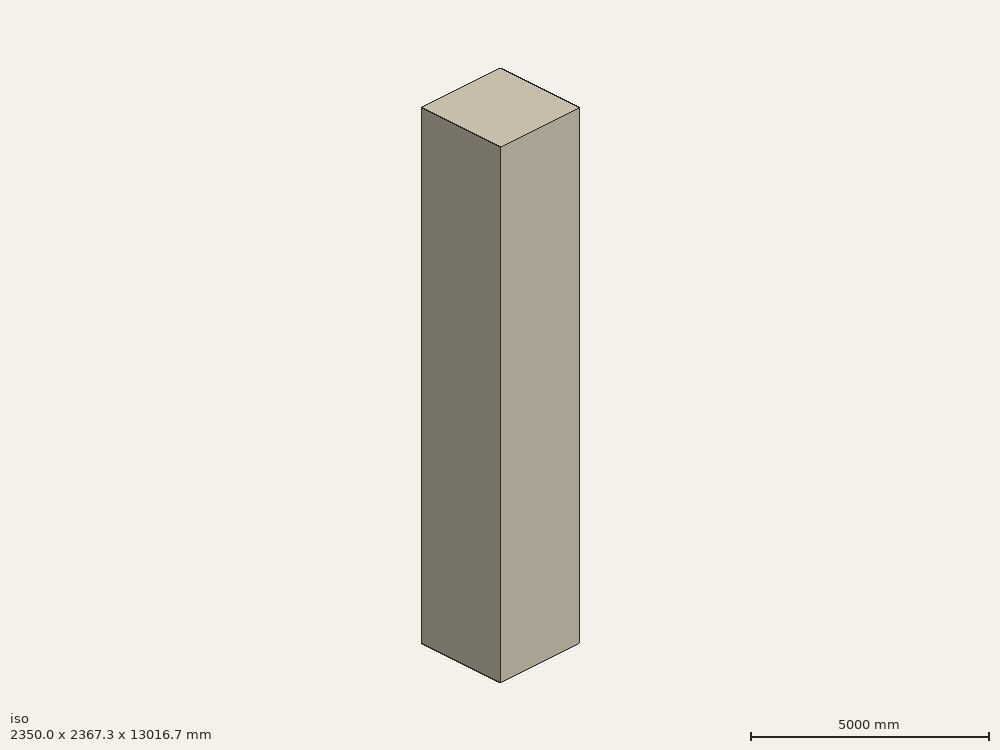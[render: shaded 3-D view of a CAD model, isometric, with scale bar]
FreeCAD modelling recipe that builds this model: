
FCSTD DOCUMENT  (FreeCAD 1.0R39109 (Git))
Label: revolveTester-7-a
License: All rights reserved
objects: App::DocumentObjectGroupPython×1252, Spreadsheet::Sheet×2, Part::FeaturePython×2, App::Part×2, Part::Cylinder×1, Sketcher::SketchObject×1, Part::Revolution×1, Part::Cut×1
note: 7 computed .brp shape members not serialized (recipe doc carries the construction recipe); baked Part::Feature solids carry a one-line shape summary decoded from their .brp

FEATURE [Spreadsheet::Sheet] defines
  cells = A1='constant; B1='HALFPI; C1(HALFPI)==pi / 2; A2='constant; B2='PI; C2(PI)==1 * pi; A3='constant; B3='TWOPI; C3(TWOPI)==2 * pi
FEATURE [Spreadsheet::Sheet] gdmlInfo
FEATURE [App::DocumentObjectGroupPython] Define  # scripted group (container) (typed FeaturePython)
  Group = -> [defines,gdmlInfo]
FEATURE [App::DocumentObjectGroupPython] HALFPI  # scripted group (container) (typed FeaturePython)
  name = HALFPI
  value = pi/2.
FEATURE [App::DocumentObjectGroupPython] PI  # scripted group (container) (typed FeaturePython)
  name = PI
  value = 1.*pi
FEATURE [App::DocumentObjectGroupPython] TWOPI  # scripted group (container) (typed FeaturePython)
  name = TWOPI
  value = 2.*pi
FEATURE [App::DocumentObjectGroupPython] Constants  # scripted group (container) (typed FeaturePython)
  Group = -> [HALFPI,PI,TWOPI]
FEATURE [App::DocumentObjectGroupPython] Quantities  # scripted group (container) (typed FeaturePython)
FEATURE [App::DocumentObjectGroupPython] Variables  # scripted group (container) (typed FeaturePython)
FEATURE [App::DocumentObjectGroupPython] Isotopes  # scripted group (container) (typed FeaturePython)
FEATURE [App::DocumentObjectGroupPython] Elements  # scripted group (container) (typed FeaturePython)
FEATURE [App::DocumentObjectGroupPython] Matrix  # scripted group (container) (typed FeaturePython)
FEATURE [App::DocumentObjectGroupPython] Surfaces  # scripted group (container) (typed FeaturePython)
FEATURE [App::DocumentObjectGroupPython] Opticals  # scripted group (container) (typed FeaturePython)
  Group = -> [Matrix,Surfaces]
FEATURE [App::DocumentObjectGroupPython] G4Isotopes  # scripted group (container) (typed FeaturePython)
FEATURE [App::DocumentObjectGroupPython] H_element  # scripted group (container) (typed FeaturePython)
  Z = 1
  atom_value = 1.008
  formula = H
  name = H_element
FEATURE [App::DocumentObjectGroupPython] He_element  # scripted group (container) (typed FeaturePython)
  Z = 2
  atom_value = 4.0026
  formula = He
  name = He_element
FEATURE [App::DocumentObjectGroupPython] Li_element  # scripted group (container) (typed FeaturePython)
  Z = 3
  atom_value = 6.94
  formula = Li
  name = Li_element
FEATURE [App::DocumentObjectGroupPython] Be_element  # scripted group (container) (typed FeaturePython)
  Z = 4
  atom_value = 9.01218
  formula = Be
  name = Be_element
FEATURE [App::DocumentObjectGroupPython] B_element  # scripted group (container) (typed FeaturePython)
  Z = 5
  atom_value = 10.81
  formula = B
  name = B_element
FEATURE [App::DocumentObjectGroupPython] C_element  # scripted group (container) (typed FeaturePython)
  Z = 6
  atom_value = 12.011
  formula = C
  name = C_element
FEATURE [App::DocumentObjectGroupPython] N_element  # scripted group (container) (typed FeaturePython)
  Z = 7
  atom_value = 14.007
  formula = N
  name = N_element
FEATURE [App::DocumentObjectGroupPython] O_element  # scripted group (container) (typed FeaturePython)
  Z = 8
  atom_value = 15.999
  formula = O
  name = O_element
FEATURE [App::DocumentObjectGroupPython] F_element  # scripted group (container) (typed FeaturePython)
  Z = 9
  atom_value = 18.9984
  formula = F
  name = F_element
FEATURE [App::DocumentObjectGroupPython] Ne_element  # scripted group (container) (typed FeaturePython)
  Z = 10
  atom_value = 20.1797
  formula = Ne
  name = Ne_element
FEATURE [App::DocumentObjectGroupPython] Na_element  # scripted group (container) (typed FeaturePython)
  Z = 11
  atom_value = 22.9898
  formula = Na
  name = Na_element
FEATURE [App::DocumentObjectGroupPython] Mg_element  # scripted group (container) (typed FeaturePython)
  Z = 12
  atom_value = 24.305
  formula = Mg
  name = Mg_element
FEATURE [App::DocumentObjectGroupPython] Al_element  # scripted group (container) (typed FeaturePython)
  Z = 13
  atom_value = 26.9815
  formula = Al
  name = Al_element
FEATURE [App::DocumentObjectGroupPython] Si_element  # scripted group (container) (typed FeaturePython)
  Z = 14
  atom_value = 28.085
  formula = Si
  name = Si_element
FEATURE [App::DocumentObjectGroupPython] P_element  # scripted group (container) (typed FeaturePython)
  Z = 15
  atom_value = 30.9738
  formula = P
  name = P_element
FEATURE [App::DocumentObjectGroupPython] S_element  # scripted group (container) (typed FeaturePython)
  Z = 16
  atom_value = 32.06
  formula = S
  name = S_element
FEATURE [App::DocumentObjectGroupPython] Cl_element  # scripted group (container) (typed FeaturePython)
  Z = 17
  atom_value = 35.45
  formula = Cl
  name = Cl_element
FEATURE [App::DocumentObjectGroupPython] Ar_element  # scripted group (container) (typed FeaturePython)
  Z = 18
  atom_value = 39.95
  formula = Ar
  name = Ar_element
FEATURE [App::DocumentObjectGroupPython] K_element  # scripted group (container) (typed FeaturePython)
  Z = 19
  atom_value = 39.0983
  formula = K
  name = K_element
FEATURE [App::DocumentObjectGroupPython] Ca_element  # scripted group (container) (typed FeaturePython)
  Z = 20
  atom_value = 40.078
  formula = Ca
  name = Ca_element
FEATURE [App::DocumentObjectGroupPython] Sc_element  # scripted group (container) (typed FeaturePython)
  Z = 21
  atom_value = 44.9559
  formula = Sc
  name = Sc_element
FEATURE [App::DocumentObjectGroupPython] Ti_element  # scripted group (container) (typed FeaturePython)
  Z = 22
  atom_value = 47.867
  formula = Ti
  name = Ti_element
FEATURE [App::DocumentObjectGroupPython] V_element  # scripted group (container) (typed FeaturePython)
  Z = 23
  atom_value = 50.9415
  formula = V
  name = V_element
FEATURE [App::DocumentObjectGroupPython] Cr_element  # scripted group (container) (typed FeaturePython)
  Z = 24
  atom_value = 51.9961
  formula = Cr
  name = Cr_element
FEATURE [App::DocumentObjectGroupPython] Mn_element  # scripted group (container) (typed FeaturePython)
  Z = 25
  atom_value = 54.938
  formula = Mn
  name = Mn_element
FEATURE [App::DocumentObjectGroupPython] Fe_element  # scripted group (container) (typed FeaturePython)
  Z = 26
  atom_value = 55.845
  formula = Fe
  name = Fe_element
FEATURE [App::DocumentObjectGroupPython] Co_element  # scripted group (container) (typed FeaturePython)
  Z = 27
  atom_value = 58.9332
  formula = Co
  name = Co_element
FEATURE [App::DocumentObjectGroupPython] Ni_element  # scripted group (container) (typed FeaturePython)
  Z = 28
  atom_value = 58.6934
  formula = Ni
  name = Ni_element
FEATURE [App::DocumentObjectGroupPython] Cu_element  # scripted group (container) (typed FeaturePython)
  Z = 29
  atom_value = 63.546
  formula = Cu
  name = Cu_element
FEATURE [App::DocumentObjectGroupPython] Zn_element  # scripted group (container) (typed FeaturePython)
  Z = 30
  atom_value = 65.38
  formula = Zn
  name = Zn_element
FEATURE [App::DocumentObjectGroupPython] Ga_element  # scripted group (container) (typed FeaturePython)
  Z = 31
  atom_value = 69.723
  formula = Ga
  name = Ga_element
FEATURE [App::DocumentObjectGroupPython] Ge_element  # scripted group (container) (typed FeaturePython)
  Z = 32
  atom_value = 72.63
  formula = Ge
  name = Ge_element
FEATURE [App::DocumentObjectGroupPython] As_element  # scripted group (container) (typed FeaturePython)
  Z = 33
  atom_value = 74.9216
  formula = As
  name = As_element
FEATURE [App::DocumentObjectGroupPython] Se_element  # scripted group (container) (typed FeaturePython)
  Z = 34
  atom_value = 78.971
  formula = Se
  name = Se_element
FEATURE [App::DocumentObjectGroupPython] Br_element  # scripted group (container) (typed FeaturePython)
  Z = 35
  atom_value = 79.904
  formula = Br
  name = Br_element
FEATURE [App::DocumentObjectGroupPython] Kr_element  # scripted group (container) (typed FeaturePython)
  Z = 36
  atom_value = 83.798
  formula = Kr
  name = Kr_element
FEATURE [App::DocumentObjectGroupPython] Rb_element  # scripted group (container) (typed FeaturePython)
  Z = 37
  atom_value = 85.4678
  formula = Rb
  name = Rb_element
FEATURE [App::DocumentObjectGroupPython] Sr_element  # scripted group (container) (typed FeaturePython)
  Z = 38
  atom_value = 87.62
  formula = Sr
  name = Sr_element
FEATURE [App::DocumentObjectGroupPython] Y_element  # scripted group (container) (typed FeaturePython)
  Z = 39
  atom_value = 88.9058
  formula = Y
  name = Y_element
FEATURE [App::DocumentObjectGroupPython] Zr_element  # scripted group (container) (typed FeaturePython)
  Z = 40
  atom_value = 91.224
  formula = Zr
  name = Zr_element
FEATURE [App::DocumentObjectGroupPython] Nb_element  # scripted group (container) (typed FeaturePython)
  Z = 41
  atom_value = 92.9064
  formula = Nb
  name = Nb_element
FEATURE [App::DocumentObjectGroupPython] Mo_element  # scripted group (container) (typed FeaturePython)
  Z = 42
  atom_value = 95.95
  formula = Mo
  name = Mo_element
FEATURE [App::DocumentObjectGroupPython] Tc_element  # scripted group (container) (typed FeaturePython)
  Z = 43
  atom_value = 97
  formula = Tc
  name = Tc_element
FEATURE [App::DocumentObjectGroupPython] Ru_element  # scripted group (container) (typed FeaturePython)
  Z = 44
  atom_value = 101.07
  formula = Ru
  name = Ru_element
FEATURE [App::DocumentObjectGroupPython] Rh_element  # scripted group (container) (typed FeaturePython)
  Z = 45
  atom_value = 102.905
  formula = Rh
  name = Rh_element
FEATURE [App::DocumentObjectGroupPython] Pd_element  # scripted group (container) (typed FeaturePython)
  Z = 46
  atom_value = 106.42
  formula = Pd
  name = Pd_element
FEATURE [App::DocumentObjectGroupPython] Ag_element  # scripted group (container) (typed FeaturePython)
  Z = 47
  atom_value = 107.868
  formula = Ag
  name = Ag_element
FEATURE [App::DocumentObjectGroupPython] Cd_element  # scripted group (container) (typed FeaturePython)
  Z = 48
  atom_value = 112.414
  formula = Cd
  name = Cd_element
FEATURE [App::DocumentObjectGroupPython] In_element  # scripted group (container) (typed FeaturePython)
  Z = 49
  atom_value = 114.818
  formula = In
  name = In_element
FEATURE [App::DocumentObjectGroupPython] Sn_element  # scripted group (container) (typed FeaturePython)
  Z = 50
  atom_value = 118.71
  formula = Sn
  name = Sn_element
FEATURE [App::DocumentObjectGroupPython] Sb_element  # scripted group (container) (typed FeaturePython)
  Z = 51
  atom_value = 121.76
  formula = Sb
  name = Sb_element
FEATURE [App::DocumentObjectGroupPython] Te_element  # scripted group (container) (typed FeaturePython)
  Z = 52
  atom_value = 127.6
  formula = Te
  name = Te_element
FEATURE [App::DocumentObjectGroupPython] I_element  # scripted group (container) (typed FeaturePython)
  Z = 53
  atom_value = 126.904
  formula = I
  name = I_element
FEATURE [App::DocumentObjectGroupPython] Xe_element  # scripted group (container) (typed FeaturePython)
  Z = 54
  atom_value = 131.293
  formula = Xe
  name = Xe_element
FEATURE [App::DocumentObjectGroupPython] Cs_element  # scripted group (container) (typed FeaturePython)
  Z = 55
  atom_value = 132.905
  formula = Cs
  name = Cs_element
FEATURE [App::DocumentObjectGroupPython] Ba_element  # scripted group (container) (typed FeaturePython)
  Z = 56
  atom_value = 137.327
  formula = Ba
  name = Ba_element
FEATURE [App::DocumentObjectGroupPython] La_element  # scripted group (container) (typed FeaturePython)
  Z = 57
  atom_value = 138.905
  formula = La
  name = La_element
FEATURE [App::DocumentObjectGroupPython] Ce_element  # scripted group (container) (typed FeaturePython)
  Z = 58
  atom_value = 140.116
  formula = Ce
  name = Ce_element
FEATURE [App::DocumentObjectGroupPython] Pr_element  # scripted group (container) (typed FeaturePython)
  Z = 59
  atom_value = 140.908
  formula = Pr
  name = Pr_element
FEATURE [App::DocumentObjectGroupPython] Nd_element  # scripted group (container) (typed FeaturePython)
  Z = 60
  atom_value = 144.242
  formula = Nd
  name = Nd_element
FEATURE [App::DocumentObjectGroupPython] Pm_element  # scripted group (container) (typed FeaturePython)
  Z = 61
  atom_value = 145
  formula = Pm
  name = Pm_element
FEATURE [App::DocumentObjectGroupPython] Sm_element  # scripted group (container) (typed FeaturePython)
  Z = 62
  atom_value = 150.36
  formula = Sm
  name = Sm_element
FEATURE [App::DocumentObjectGroupPython] Eu_element  # scripted group (container) (typed FeaturePython)
  Z = 63
  atom_value = 151.964
  formula = Eu
  name = Eu_element
FEATURE [App::DocumentObjectGroupPython] Gd_element  # scripted group (container) (typed FeaturePython)
  Z = 64
  atom_value = 157.25
  formula = Gd
  name = Gd_element
FEATURE [App::DocumentObjectGroupPython] Tb_element  # scripted group (container) (typed FeaturePython)
  Z = 65
  atom_value = 158.925
  formula = Tb
  name = Tb_element
FEATURE [App::DocumentObjectGroupPython] Dy_element  # scripted group (container) (typed FeaturePython)
  Z = 66
  atom_value = 162.5
  formula = Dy
  name = Dy_element
FEATURE [App::DocumentObjectGroupPython] Ho_element  # scripted group (container) (typed FeaturePython)
  Z = 67
  atom_value = 164.93
  formula = Ho
  name = Ho_element
FEATURE [App::DocumentObjectGroupPython] Er_element  # scripted group (container) (typed FeaturePython)
  Z = 68
  atom_value = 167.259
  formula = Er
  name = Er_element
FEATURE [App::DocumentObjectGroupPython] Tm_element  # scripted group (container) (typed FeaturePython)
  Z = 69
  atom_value = 168.934
  formula = Tm
  name = Tm_element
FEATURE [App::DocumentObjectGroupPython] Yb_element  # scripted group (container) (typed FeaturePython)
  Z = 70
  atom_value = 173.045
  formula = Yb
  name = Yb_element
FEATURE [App::DocumentObjectGroupPython] Lu_element  # scripted group (container) (typed FeaturePython)
  Z = 71
  atom_value = 174.967
  formula = Lu
  name = Lu_element
FEATURE [App::DocumentObjectGroupPython] Hf_element  # scripted group (container) (typed FeaturePython)
  Z = 72
  atom_value = 178.49
  formula = Hf
  name = Hf_element
FEATURE [App::DocumentObjectGroupPython] Ta_element  # scripted group (container) (typed FeaturePython)
  Z = 73
  atom_value = 180.948
  formula = Ta
  name = Ta_element
FEATURE [App::DocumentObjectGroupPython] W_element  # scripted group (container) (typed FeaturePython)
  Z = 74
  atom_value = 183.84
  formula = W
  name = W_element
FEATURE [App::DocumentObjectGroupPython] Re_element  # scripted group (container) (typed FeaturePython)
  Z = 75
  atom_value = 186.207
  formula = Re
  name = Re_element
FEATURE [App::DocumentObjectGroupPython] Os_element  # scripted group (container) (typed FeaturePython)
  Z = 76
  atom_value = 190.23
  formula = Os
  name = Os_element
FEATURE [App::DocumentObjectGroupPython] Ir_element  # scripted group (container) (typed FeaturePython)
  Z = 77
  atom_value = 192.217
  formula = Ir
  name = Ir_element
FEATURE [App::DocumentObjectGroupPython] Pt_element  # scripted group (container) (typed FeaturePython)
  Z = 78
  atom_value = 195.084
  formula = Pt
  name = Pt_element
FEATURE [App::DocumentObjectGroupPython] Au_element  # scripted group (container) (typed FeaturePython)
  Z = 79
  atom_value = 196.967
  formula = Au
  name = Au_element
FEATURE [App::DocumentObjectGroupPython] Hg_element  # scripted group (container) (typed FeaturePython)
  Z = 80
  atom_value = 200.592
  formula = Hg
  name = Hg_element
FEATURE [App::DocumentObjectGroupPython] Tl_element  # scripted group (container) (typed FeaturePython)
  Z = 81
  atom_value = 204.38
  formula = Tl
  name = Tl_element
FEATURE [App::DocumentObjectGroupPython] Pb_element  # scripted group (container) (typed FeaturePython)
  Z = 82
  atom_value = 207.2
  formula = Pb
  name = Pb_element
FEATURE [App::DocumentObjectGroupPython] Bi_element  # scripted group (container) (typed FeaturePython)
  Z = 83
  atom_value = 208.98
  formula = Bi
  name = Bi_element
FEATURE [App::DocumentObjectGroupPython] Po_element  # scripted group (container) (typed FeaturePython)
  Z = 84
  atom_value = 209
  formula = Po
  name = Po_element
FEATURE [App::DocumentObjectGroupPython] At_element  # scripted group (container) (typed FeaturePython)
  Z = 85
  atom_value = 210
  formula = At
  name = At_element
FEATURE [App::DocumentObjectGroupPython] Rn_element  # scripted group (container) (typed FeaturePython)
  Z = 86
  atom_value = 222
  formula = Rn
  name = Rn_element
FEATURE [App::DocumentObjectGroupPython] Fr_element  # scripted group (container) (typed FeaturePython)
  Z = 87
  atom_value = 223
  formula = Fr
  name = Fr_element
FEATURE [App::DocumentObjectGroupPython] Ra_element  # scripted group (container) (typed FeaturePython)
  Z = 88
  atom_value = 226
  formula = Ra
  name = Ra_element
FEATURE [App::DocumentObjectGroupPython] Ac_element  # scripted group (container) (typed FeaturePython)
  Z = 89
  atom_value = 227
  formula = Ac
  name = Ac_element
FEATURE [App::DocumentObjectGroupPython] Th_element  # scripted group (container) (typed FeaturePython)
  Z = 90
  atom_value = 232.038
  formula = Th
  name = Th_element
FEATURE [App::DocumentObjectGroupPython] Pa_element  # scripted group (container) (typed FeaturePython)
  Z = 91
  atom_value = 231.036
  formula = Pa
  name = Pa_element
FEATURE [App::DocumentObjectGroupPython] U_element  # scripted group (container) (typed FeaturePython)
  Z = 92
  atom_value = 238.029
  formula = U
  name = U_element
FEATURE [App::DocumentObjectGroupPython] Np_element  # scripted group (container) (typed FeaturePython)
  Z = 93
  atom_value = 237
  formula = Np
  name = Np_element
FEATURE [App::DocumentObjectGroupPython] Pu_element  # scripted group (container) (typed FeaturePython)
  Z = 94
  atom_value = 244
  formula = Pu
  name = Pu_element
FEATURE [App::DocumentObjectGroupPython] Am_element  # scripted group (container) (typed FeaturePython)
  Z = 95
  atom_value = 243
  formula = Am
  name = Am_element
FEATURE [App::DocumentObjectGroupPython] Cm_element  # scripted group (container) (typed FeaturePython)
  Z = 96
  atom_value = 247
  formula = Cm
  name = Cm_element
FEATURE [App::DocumentObjectGroupPython] Bk_element  # scripted group (container) (typed FeaturePython)
  Z = 97
  atom_value = 247
  formula = Bk
  name = Bk_element
FEATURE [App::DocumentObjectGroupPython] Cf_element  # scripted group (container) (typed FeaturePython)
  Z = 98
  atom_value = 251
  formula = Cf
  name = Cf_element
FEATURE [App::DocumentObjectGroupPython] G4Elements  # scripted group (container) (typed FeaturePython)
  Group = -> [H_element,He_element,Li_element,Be_element,B_element,C_element,N_element,O_element,F_element,Ne_element,Na_element,Mg_element,Al_element,Si_element,P_element,S_element,Cl_element,Ar_element,K_element,Ca_element,Sc_element,Ti_element,V_element,Cr_element,Mn_element,Fe_element,Co_element,Ni_element,Cu_element,Zn_element,Ga_element,Ge_element,As_element,Se_element,Br_element,Kr_element,Rb_element,+61 more]
FEATURE [App::DocumentObjectGroupPython] H_element001  label="H_element : 0.101"  # scripted group (container) (typed FeaturePython)
  n = 0.101327
FEATURE [App::DocumentObjectGroupPython] C_element001  label="C_element : 0.775"  # scripted group (container) (typed FeaturePython)
  n = 0.7755
FEATURE [App::DocumentObjectGroupPython] N_element001  label="N_element : 0.035"  # scripted group (container) (typed FeaturePython)
  n = 0.035057
FEATURE [App::DocumentObjectGroupPython] O_element001  label="O_element : 0.052"  # scripted group (container) (typed FeaturePython)
  n = 0.0523159
FEATURE [App::DocumentObjectGroupPython] F_element001  label="F_element : 0.017"  # scripted group (container) (typed FeaturePython)
  n = 0.017422
FEATURE [App::DocumentObjectGroupPython] Ca_element001  label="Ca_element : 0.018"  # scripted group (container) (typed FeaturePython)
  n = 0.018378
FEATURE [App::DocumentObjectGroupPython] G4_A_150_TISSUE  label="G4_A-150_TISSUE"  # scripted group (container) (typed FeaturePython)
  Dunit = g/cm3
  Dvalue = 1.127
  Group = -> [H_element001,C_element001,N_element001,O_element001,F_element001,Ca_element001]
  conduct = 2
  density = 1
  expand = 3
  formula = G4_A-150_TISSUE
  name = G4_A-150_TISSUE
  specific = 4
FEATURE [App::DocumentObjectGroupPython] C_element002  label="C_element : 3"  # scripted group (container) (typed FeaturePython)
  n = 3
  ref = C_element
FEATURE [App::DocumentObjectGroupPython] H_element002  label="H_element : 6"  # scripted group (container) (typed FeaturePython)
  n = 6
  ref = H_element
FEATURE [App::DocumentObjectGroupPython] O_element002  label="O_element : 1"  # scripted group (container) (typed FeaturePython)
  n = 1
  ref = O_element
FEATURE [App::DocumentObjectGroupPython] G4_ACETONE  # scripted group (container) (typed FeaturePython)
  Dunit = g/cm3
  Dvalue = 0.7899
  Group = -> [C_element002,H_element002,O_element002]
  conduct = 2
  density = 1
  expand = 3
  formula = G4_ACETONE
  name = G4_ACETONE
  specific = 4
FEATURE [App::DocumentObjectGroupPython] C_element003  label="C_element : 2"  # scripted group (container) (typed FeaturePython)
  n = 2
  ref = C_element
FEATURE [App::DocumentObjectGroupPython] H_element003  label="H_element : 2"  # scripted group (container) (typed FeaturePython)
  n = 2
  ref = H_element
FEATURE [App::DocumentObjectGroupPython] G4_ACETYLENE  # scripted group (container) (typed FeaturePython)
  Dunit = g/cm3
  Dvalue = 0.0010967
  Group = -> [C_element003,H_element003]
  conduct = 2
  density = 1
  expand = 3
  formula = G4_ACETYLENE
  name = G4_ACETYLENE
  specific = 4
FEATURE [App::DocumentObjectGroupPython] C_element004  label="C_element : 5"  # scripted group (container) (typed FeaturePython)
  n = 5
  ref = C_element
FEATURE [App::DocumentObjectGroupPython] H_element004  label="H_element : 5"  # scripted group (container) (typed FeaturePython)
  n = 5
  ref = H_element
FEATURE [App::DocumentObjectGroupPython] N_element002  label="N_element : 5"  # scripted group (container) (typed FeaturePython)
  n = 5
  ref = N_element
FEATURE [App::DocumentObjectGroupPython] G4_ADENINE  # scripted group (container) (typed FeaturePython)
  Dunit = g/cm3
  Dvalue = 1.6
  Group = -> [C_element004,H_element004,N_element002]
  conduct = 2
  density = 1
  expand = 3
  formula = G4_ADENINE
  name = G4_ADENINE
  specific = 4
FEATURE [App::DocumentObjectGroupPython] H_element005  label="H_element : 0.114"  # scripted group (container) (typed FeaturePython)
  n = 0.114
FEATURE [App::DocumentObjectGroupPython] C_element005  label="C_element : 0.598"  # scripted group (container) (typed FeaturePython)
  n = 0.598
FEATURE [App::DocumentObjectGroupPython] N_element003  label="N_element : 0.007"  # scripted group (container) (typed FeaturePython)
  n = 0.007
FEATURE [App::DocumentObjectGroupPython] O_element003  label="O_element : 0.278"  # scripted group (container) (typed FeaturePython)
  n = 0.278
FEATURE [App::DocumentObjectGroupPython] Na_element001  label="Na_element : 0.001"  # scripted group (container) (typed FeaturePython)
  n = 0.001
FEATURE [App::DocumentObjectGroupPython] S_element001  label="S_element : 0.001"  # scripted group (container) (typed FeaturePython)
  n = 0.001
FEATURE [App::DocumentObjectGroupPython] Cl_element001  label="Cl_element : 0.001"  # scripted group (container) (typed FeaturePython)
  n = 0.001
FEATURE [App::DocumentObjectGroupPython] G4_ADIPOSE_TISSUE_ICRP  # scripted group (container) (typed FeaturePython)
  Dunit = g/cm3
  Dvalue = 0.95
  Group = -> [H_element005,C_element005,N_element003,O_element003,Na_element001,S_element001,Cl_element001]
  conduct = 2
  density = 1
  expand = 3
  formula = G4_ADIPOSE_TISSUE_ICRP
  name = G4_ADIPOSE_TISSUE_ICRP
  specific = 4
FEATURE [App::DocumentObjectGroupPython] C_element006  label="C_element : 0.000"  # scripted group (container) (typed FeaturePython)
  n = 0.000124
FEATURE [App::DocumentObjectGroupPython] N_element004  label="N_element : 0.755"  # scripted group (container) (typed FeaturePython)
  n = 0.755268
FEATURE [App::DocumentObjectGroupPython] O_element004  label="O_element : 0.232"  # scripted group (container) (typed FeaturePython)
  n = 0.231781
FEATURE [App::DocumentObjectGroupPython] Ar_element001  label="Ar_element : 0.013"  # scripted group (container) (typed FeaturePython)
  n = 0.012827
FEATURE [App::DocumentObjectGroupPython] G4_AIR  # scripted group (container) (typed FeaturePython)
  Dunit = g/cm3
  Dvalue = 0.00120479
  Group = -> [C_element006,N_element004,O_element004,Ar_element001]
  conduct = 2
  density = 1
  expand = 3
  formula = G4_AIR
  name = G4_AIR
  specific = 4
FEATURE [App::DocumentObjectGroupPython] C_element007  label="C_element : 006"  # scripted group (container) (typed FeaturePython)
  n = 3
  ref = C_element
FEATURE [App::DocumentObjectGroupPython] H_element006  label="H_element : 7"  # scripted group (container) (typed FeaturePython)
  n = 7
  ref = H_element
FEATURE [App::DocumentObjectGroupPython] N_element005  label="N_element : 1"  # scripted group (container) (typed FeaturePython)
  n = 1
  ref = N_element
FEATURE [App::DocumentObjectGroupPython] O_element005  label="O_element : 2"  # scripted group (container) (typed FeaturePython)
  n = 2
  ref = O_element
FEATURE [App::DocumentObjectGroupPython] G4_ALANINE  # scripted group (container) (typed FeaturePython)
  Dunit = g/cm3
  Dvalue = 1.42
  Group = -> [C_element007,H_element006,N_element005,O_element005]
  conduct = 2
  density = 1
  expand = 3
  formula = G4_ALANINE
  name = G4_ALANINE
  specific = 4
FEATURE [App::DocumentObjectGroupPython] Al_element001  label="Al_element : 2"  # scripted group (container) (typed FeaturePython)
  n = 2
  ref = Al_element
FEATURE [App::DocumentObjectGroupPython] O_element006  label="O_element : 3"  # scripted group (container) (typed FeaturePython)
  n = 3
  ref = O_element
FEATURE [App::DocumentObjectGroupPython] G4_ALUMINUM_OXIDE  # scripted group (container) (typed FeaturePython)
  Dunit = g/cm3
  Dvalue = 3.97
  Group = -> [Al_element001,O_element006]
  conduct = 2
  density = 1
  expand = 3
  formula = G4_ALUMINUM_OXIDE
  name = G4_ALUMINUM_OXIDE
  specific = 4
FEATURE [App::DocumentObjectGroupPython] H_element007  label="H_element : 0.106"  # scripted group (container) (typed FeaturePython)
  n = 0.10593
FEATURE [App::DocumentObjectGroupPython] C_element008  label="C_element : 0.789"  # scripted group (container) (typed FeaturePython)
  n = 0.788974
FEATURE [App::DocumentObjectGroupPython] O_element007  label="O_element : 0.105"  # scripted group (container) (typed FeaturePython)
  n = 0.105096
FEATURE [App::DocumentObjectGroupPython] G4_AMBER  # scripted group (container) (typed FeaturePython)
  Dunit = g/cm3
  Dvalue = 1.1
  Group = -> [H_element007,C_element008,O_element007]
  conduct = 2
  density = 1
  expand = 3
  formula = G4_AMBER
  name = G4_AMBER
  specific = 4
FEATURE [App::DocumentObjectGroupPython] N_element006  label="N_element : 006"  # scripted group (container) (typed FeaturePython)
  n = 1
  ref = N_element
FEATURE [App::DocumentObjectGroupPython] H_element008  label="H_element : 3"  # scripted group (container) (typed FeaturePython)
  n = 3
  ref = H_element
FEATURE [App::DocumentObjectGroupPython] G4_AMMONIA  # scripted group (container) (typed FeaturePython)
  Dunit = g/cm3
  Dvalue = 0.000826019
  Group = -> [N_element006,H_element008]
  conduct = 2
  density = 1
  expand = 3
  formula = G4_AMMONIA
  name = G4_AMMONIA
  specific = 4
FEATURE [App::DocumentObjectGroupPython] C_element009  label="C_element : 6"  # scripted group (container) (typed FeaturePython)
  n = 6
  ref = C_element
FEATURE [App::DocumentObjectGroupPython] H_element009  label="H_element : 008"  # scripted group (container) (typed FeaturePython)
  n = 7
  ref = H_element
FEATURE [App::DocumentObjectGroupPython] N_element007  label="N_element : 007"  # scripted group (container) (typed FeaturePython)
  n = 1
  ref = N_element
FEATURE [App::DocumentObjectGroupPython] G4_ANILINE  # scripted group (container) (typed FeaturePython)
  Dunit = g/cm3
  Dvalue = 1.0235
  Group = -> [C_element009,H_element009,N_element007]
  conduct = 2
  density = 1
  expand = 3
  formula = G4_ANILINE
  name = G4_ANILINE
  specific = 4
FEATURE [App::DocumentObjectGroupPython] C_element010  label="C_element : 14"  # scripted group (container) (typed FeaturePython)
  n = 14
  ref = C_element
FEATURE [App::DocumentObjectGroupPython] H_element010  label="H_element : 10"  # scripted group (container) (typed FeaturePython)
  n = 10
  ref = H_element
FEATURE [App::DocumentObjectGroupPython] G4_ANTHRACENE  # scripted group (container) (typed FeaturePython)
  Dunit = g/cm3
  Dvalue = 1.283
  Group = -> [C_element010,H_element010]
  conduct = 2
  density = 1
  expand = 3
  formula = G4_ANTHRACENE
  name = G4_ANTHRACENE
  specific = 4
FEATURE [App::DocumentObjectGroupPython] H_element011  label="H_element : 0.065"  # scripted group (container) (typed FeaturePython)
  n = 0.0654709
FEATURE [App::DocumentObjectGroupPython] C_element011  label="C_element : 0.537"  # scripted group (container) (typed FeaturePython)
  n = 0.536944
FEATURE [App::DocumentObjectGroupPython] N_element008  label="N_element : 0.021"  # scripted group (container) (typed FeaturePython)
  n = 0.0215
FEATURE [App::DocumentObjectGroupPython] O_element008  label="O_element : 0.032"  # scripted group (container) (typed FeaturePython)
  n = 0.032085
FEATURE [App::DocumentObjectGroupPython] F_element002  label="F_element : 0.167"  # scripted group (container) (typed FeaturePython)
  n = 0.167411
FEATURE [App::DocumentObjectGroupPython] Ca_element002  label="Ca_element : 0.177"  # scripted group (container) (typed FeaturePython)
  n = 0.176589
FEATURE [App::DocumentObjectGroupPython] G4_B_100_BONE  label="G4_B-100_BONE"  # scripted group (container) (typed FeaturePython)
  Dunit = g/cm3
  Dvalue = 1.45
  Group = -> [H_element011,C_element011,N_element008,O_element008,F_element002,Ca_element002]
  conduct = 2
  density = 1
  expand = 3
  formula = G4_B-100_BONE
  name = G4_B-100_BONE
  specific = 4
FEATURE [App::DocumentObjectGroupPython] H_element012  label="H_element : 0.057"  # scripted group (container) (typed FeaturePython)
  n = 0.057441
FEATURE [App::DocumentObjectGroupPython] C_element012  label="C_element : 0.790"  # scripted group (container) (typed FeaturePython)
  n = 0.774591
FEATURE [App::DocumentObjectGroupPython] O_element009  label="O_element : 0.168"  # scripted group (container) (typed FeaturePython)
  n = 0.167968
FEATURE [App::DocumentObjectGroupPython] G4_BAKELITE  # scripted group (container) (typed FeaturePython)
  Dunit = g/cm3
  Dvalue = 1.25
  Group = -> [H_element012,C_element012,O_element009]
  conduct = 2
  density = 1
  expand = 3
  formula = G4_BAKELITE
  name = G4_BAKELITE
  specific = 4
FEATURE [App::DocumentObjectGroupPython] Ba_element001  label="Ba_element : 1"  # scripted group (container) (typed FeaturePython)
  n = 1
  ref = Ba_element
FEATURE [App::DocumentObjectGroupPython] F_element003  label="F_element : 2"  # scripted group (container) (typed FeaturePython)
  n = 2
  ref = F_element
FEATURE [App::DocumentObjectGroupPython] G4_BARIUM_FLUORIDE  # scripted group (container) (typed FeaturePython)
  Dunit = g/cm3
  Dvalue = 4.89
  Group = -> [Ba_element001,F_element003]
  conduct = 2
  density = 1
  expand = 3
  formula = G4_BARIUM_FLUORIDE
  name = G4_BARIUM_FLUORIDE
  specific = 4
FEATURE [App::DocumentObjectGroupPython] Ba_element002  label="Ba_element : 002"  # scripted group (container) (typed FeaturePython)
  n = 1
  ref = Ba_element
FEATURE [App::DocumentObjectGroupPython] S_element002  label="S_element : 1"  # scripted group (container) (typed FeaturePython)
  n = 1
  ref = S_element
FEATURE [App::DocumentObjectGroupPython] O_element010  label="O_element : 4"  # scripted group (container) (typed FeaturePython)
  n = 4
  ref = O_element
FEATURE [App::DocumentObjectGroupPython] G4_BARIUM_SULFATE  # scripted group (container) (typed FeaturePython)
  Dunit = g/cm3
  Dvalue = 4.5
  Group = -> [Ba_element002,S_element002,O_element010]
  conduct = 2
  density = 1
  expand = 3
  formula = G4_BARIUM_SULFATE
  name = G4_BARIUM_SULFATE
  specific = 4
FEATURE [App::DocumentObjectGroupPython] C_element013  label="C_element : 007"  # scripted group (container) (typed FeaturePython)
  n = 6
  ref = C_element
FEATURE [App::DocumentObjectGroupPython] H_element013  label="H_element : 009"  # scripted group (container) (typed FeaturePython)
  n = 6
  ref = H_element
FEATURE [App::DocumentObjectGroupPython] G4_BENZENE  # scripted group (container) (typed FeaturePython)
  Dunit = g/cm3
  Dvalue = 0.87865
  Group = -> [C_element013,H_element013]
  conduct = 2
  density = 1
  expand = 3
  formula = G4_BENZENE
  name = G4_BENZENE
  specific = 4
FEATURE [App::DocumentObjectGroupPython] Be_element001  label="Be_element : 1"  # scripted group (container) (typed FeaturePython)
  n = 1
  ref = Be_element
FEATURE [App::DocumentObjectGroupPython] O_element011  label="O_element : 005"  # scripted group (container) (typed FeaturePython)
  n = 1
  ref = O_element
FEATURE [App::DocumentObjectGroupPython] G4_BERYLLIUM_OXIDE  # scripted group (container) (typed FeaturePython)
  Dunit = g/cm3
  Dvalue = 3.01
  Group = -> [Be_element001,O_element011]
  conduct = 2
  density = 1
  expand = 3
  formula = G4_BERYLLIUM_OXIDE
  name = G4_BERYLLIUM_OXIDE
  specific = 4
FEATURE [App::DocumentObjectGroupPython] Bi_element001  label="Bi_element : 4"  # scripted group (container) (typed FeaturePython)
  n = 4
  ref = Bi_element
FEATURE [App::DocumentObjectGroupPython] Ge_element001  label="Ge_element : 3"  # scripted group (container) (typed FeaturePython)
  n = 3
  ref = Ge_element
FEATURE [App::DocumentObjectGroupPython] O_element012  label="O_element : 12"  # scripted group (container) (typed FeaturePython)
  n = 12
  ref = O_element
FEATURE [App::DocumentObjectGroupPython] G4_BGO  # scripted group (container) (typed FeaturePython)
  Dunit = g/cm3
  Dvalue = 7.13
  Group = -> [Bi_element001,Ge_element001,O_element012]
  conduct = 2
  density = 1
  expand = 3
  formula = G4_BGO
  name = G4_BGO
  specific = 4
FEATURE [App::DocumentObjectGroupPython] H_element014  label="H_element : 0.102"  # scripted group (container) (typed FeaturePython)
  n = 0.102
FEATURE [App::DocumentObjectGroupPython] C_element014  label="C_element : 0.110"  # scripted group (container) (typed FeaturePython)
  n = 0.11
FEATURE [App::DocumentObjectGroupPython] N_element009  label="N_element : 0.033"  # scripted group (container) (typed FeaturePython)
  n = 0.033
FEATURE [App::DocumentObjectGroupPython] O_element013  label="O_element : 0.745"  # scripted group (container) (typed FeaturePython)
  n = 0.745
FEATURE [App::DocumentObjectGroupPython] Na_element002  label="Na_element : 0.002"  # scripted group (container) (typed FeaturePython)
  n = 0.001
FEATURE [App::DocumentObjectGroupPython] P_element001  label="P_element : 0.001"  # scripted group (container) (typed FeaturePython)
  n = 0.001
FEATURE [App::DocumentObjectGroupPython] S_element003  label="S_element : 0.002"  # scripted group (container) (typed FeaturePython)
  n = 0.002
FEATURE [App::DocumentObjectGroupPython] Cl_element002  label="Cl_element : 0.003"  # scripted group (container) (typed FeaturePython)
  n = 0.003
FEATURE [App::DocumentObjectGroupPython] K_element001  label="K_element : 0.002"  # scripted group (container) (typed FeaturePython)
  n = 0.002
FEATURE [App::DocumentObjectGroupPython] Fe_element001  label="Fe_element : 0.001"  # scripted group (container) (typed FeaturePython)
  n = 0.001
FEATURE [App::DocumentObjectGroupPython] G4_BLOOD_ICRP  # scripted group (container) (typed FeaturePython)
  Dunit = g/cm3
  Dvalue = 1.06
  Group = -> [H_element014,C_element014,N_element009,O_element013,Na_element002,P_element001,S_element003,Cl_element002,K_element001,Fe_element001]
  conduct = 2
  density = 1
  expand = 3
  formula = G4_BLOOD_ICRP
  name = G4_BLOOD_ICRP
  specific = 4
FEATURE [App::DocumentObjectGroupPython] H_element015  label="H_element : 0.064"  # scripted group (container) (typed FeaturePython)
  n = 0.064
FEATURE [App::DocumentObjectGroupPython] C_element015  label="C_element : 0.278"  # scripted group (container) (typed FeaturePython)
  n = 0.278
FEATURE [App::DocumentObjectGroupPython] N_element010  label="N_element : 0.027"  # scripted group (container) (typed FeaturePython)
  n = 0.027
FEATURE [App::DocumentObjectGroupPython] O_element014  label="O_element : 0.410"  # scripted group (container) (typed FeaturePython)
  n = 0.41
FEATURE [App::DocumentObjectGroupPython] Mg_element001  label="Mg_element : 0.002"  # scripted group (container) (typed FeaturePython)
  n = 0.002
FEATURE [App::DocumentObjectGroupPython] P_element002  label="P_element : 0.070"  # scripted group (container) (typed FeaturePython)
  n = 0.07
FEATURE [App::DocumentObjectGroupPython] S_element004  label="S_element : 0.003"  # scripted group (container) (typed FeaturePython)
  n = 0.002
FEATURE [App::DocumentObjectGroupPython] Ca_element003  label="Ca_element : 0.147"  # scripted group (container) (typed FeaturePython)
  n = 0.147
FEATURE [App::DocumentObjectGroupPython] G4_BONE_COMPACT_ICRU  # scripted group (container) (typed FeaturePython)
  Dunit = g/cm3
  Dvalue = 1.85
  Group = -> [H_element015,C_element015,N_element010,O_element014,Mg_element001,P_element002,S_element004,Ca_element003]
  conduct = 2
  density = 1
  expand = 3
  formula = G4_BONE_COMPACT_ICRU
  name = G4_BONE_COMPACT_ICRU
  specific = 4
FEATURE [App::DocumentObjectGroupPython] H_element016  label="H_element : 0.034"  # scripted group (container) (typed FeaturePython)
  n = 0.034
FEATURE [App::DocumentObjectGroupPython] C_element016  label="C_element : 0.155"  # scripted group (container) (typed FeaturePython)
  n = 0.155
FEATURE [App::DocumentObjectGroupPython] N_element011  label="N_element : 0.042"  # scripted group (container) (typed FeaturePython)
  n = 0.042
FEATURE [App::DocumentObjectGroupPython] O_element015  label="O_element : 0.435"  # scripted group (container) (typed FeaturePython)
  n = 0.435
FEATURE [App::DocumentObjectGroupPython] Na_element003  label="Na_element : 0.003"  # scripted group (container) (typed FeaturePython)
  n = 0.001
FEATURE [App::DocumentObjectGroupPython] Mg_element002  label="Mg_element : 0.003"  # scripted group (container) (typed FeaturePython)
  n = 0.002
FEATURE [App::DocumentObjectGroupPython] P_element003  label="P_element : 0.103"  # scripted group (container) (typed FeaturePython)
  n = 0.103
FEATURE [App::DocumentObjectGroupPython] S_element005  label="S_element : 0.004"  # scripted group (container) (typed FeaturePython)
  n = 0.003
FEATURE [App::DocumentObjectGroupPython] Ca_element004  label="Ca_element : 0.225"  # scripted group (container) (typed FeaturePython)
  n = 0.225
FEATURE [App::DocumentObjectGroupPython] G4_BONE_CORTICAL_ICRP  # scripted group (container) (typed FeaturePython)
  Dunit = g/cm3
  Dvalue = 1.92
  Group = -> [H_element016,C_element016,N_element011,O_element015,Na_element003,Mg_element002,P_element003,S_element005,Ca_element004]
  conduct = 2
  density = 1
  expand = 3
  formula = G4_BONE_CORTICAL_ICRP
  name = G4_BONE_CORTICAL_ICRP
  specific = 4
FEATURE [App::DocumentObjectGroupPython] B_element001  label="B_element : 4"  # scripted group (container) (typed FeaturePython)
  n = 4
  ref = B_element
FEATURE [App::DocumentObjectGroupPython] C_element017  label="C_element : 1"  # scripted group (container) (typed FeaturePython)
  n = 1
  ref = C_element
FEATURE [App::DocumentObjectGroupPython] G4_BORON_CARBIDE  # scripted group (container) (typed FeaturePython)
  Dunit = g/cm3
  Dvalue = 2.52
  Group = -> [B_element001,C_element017]
  conduct = 2
  density = 1
  expand = 3
  formula = G4_BORON_CARBIDE
  name = G4_BORON_CARBIDE
  specific = 4
FEATURE [App::DocumentObjectGroupPython] B_element002  label="B_element : 2"  # scripted group (container) (typed FeaturePython)
  n = 2
  ref = B_element
FEATURE [App::DocumentObjectGroupPython] O_element016  label="O_element : 006"  # scripted group (container) (typed FeaturePython)
  n = 3
  ref = O_element
FEATURE [App::DocumentObjectGroupPython] G4_BORON_OXIDE  # scripted group (container) (typed FeaturePython)
  Dunit = g/cm3
  Dvalue = 1.812
  Group = -> [B_element002,O_element016]
  conduct = 2
  density = 1
  expand = 3
  formula = G4_BORON_OXIDE
  name = G4_BORON_OXIDE
  specific = 4
FEATURE [App::DocumentObjectGroupPython] H_element017  label="H_element : 0.107"  # scripted group (container) (typed FeaturePython)
  n = 0.107
FEATURE [App::DocumentObjectGroupPython] C_element018  label="C_element : 0.145"  # scripted group (container) (typed FeaturePython)
  n = 0.145
FEATURE [App::DocumentObjectGroupPython] N_element012  label="N_element : 0.022"  # scripted group (container) (typed FeaturePython)
  n = 0.022
FEATURE [App::DocumentObjectGroupPython] O_element017  label="O_element : 0.712"  # scripted group (container) (typed FeaturePython)
  n = 0.712
FEATURE [App::DocumentObjectGroupPython] Na_element004  label="Na_element : 0.004"  # scripted group (container) (typed FeaturePython)
  n = 0.002
FEATURE [App::DocumentObjectGroupPython] P_element004  label="P_element : 0.004"  # scripted group (container) (typed FeaturePython)
  n = 0.004
FEATURE [App::DocumentObjectGroupPython] S_element006  label="S_element : 0.005"  # scripted group (container) (typed FeaturePython)
  n = 0.002
FEATURE [App::DocumentObjectGroupPython] Cl_element003  label="Cl_element : 0.004"  # scripted group (container) (typed FeaturePython)
  n = 0.003
FEATURE [App::DocumentObjectGroupPython] K_element002  label="K_element : 0.003"  # scripted group (container) (typed FeaturePython)
  n = 0.003
FEATURE [App::DocumentObjectGroupPython] G4_BRAIN_ICRP  # scripted group (container) (typed FeaturePython)
  Dunit = g/cm3
  Dvalue = 1.04
  Group = -> [H_element017,C_element018,N_element012,O_element017,Na_element004,P_element004,S_element006,Cl_element003,K_element002]
  conduct = 2
  density = 1
  expand = 3
  formula = G4_BRAIN_ICRP
  name = G4_BRAIN_ICRP
  specific = 4
FEATURE [App::DocumentObjectGroupPython] C_element019  label="C_element : 4"  # scripted group (container) (typed FeaturePython)
  n = 4
  ref = C_element
FEATURE [App::DocumentObjectGroupPython] H_element018  label="H_element : 010"  # scripted group (container) (typed FeaturePython)
  n = 10
  ref = H_element
FEATURE [App::DocumentObjectGroupPython] G4_BUTANE  # scripted group (container) (typed FeaturePython)
  Dunit = g/cm3
  Dvalue = 0.00249343
  Group = -> [C_element019,H_element018]
  conduct = 2
  density = 1
  expand = 3
  formula = G4_BUTANE
  name = G4_BUTANE
  specific = 4
FEATURE [App::DocumentObjectGroupPython] C_element020  label="C_element : 008"  # scripted group (container) (typed FeaturePython)
  n = 4
  ref = C_element
FEATURE [App::DocumentObjectGroupPython] H_element019  label="H_element : 011"  # scripted group (container) (typed FeaturePython)
  n = 10
  ref = H_element
FEATURE [App::DocumentObjectGroupPython] O_element018  label="O_element : 007"  # scripted group (container) (typed FeaturePython)
  n = 1
  ref = O_element
FEATURE [App::DocumentObjectGroupPython] G4_N_BUTYL_ALCOHOL  label="G4_N-BUTYL_ALCOHOL"  # scripted group (container) (typed FeaturePython)
  Dunit = g/cm3
  Dvalue = 0.8098
  Group = -> [C_element020,H_element019,O_element018]
  conduct = 2
  density = 1
  expand = 3
  formula = G4_N-BUTYL_ALCOHOL
  name = G4_N-BUTYL_ALCOHOL
  specific = 4
FEATURE [App::DocumentObjectGroupPython] H_element020  label="H_element : 0.025"  # scripted group (container) (typed FeaturePython)
  n = 0.02468
FEATURE [App::DocumentObjectGroupPython] C_element021  label="C_element : 0.502"  # scripted group (container) (typed FeaturePython)
  n = 0.501611
FEATURE [App::DocumentObjectGroupPython] O_element019  label="O_element : 0.005"  # scripted group (container) (typed FeaturePython)
  n = 0.004527
FEATURE [App::DocumentObjectGroupPython] F_element004  label="F_element : 0.465"  # scripted group (container) (typed FeaturePython)
  n = 0.465209
FEATURE [App::DocumentObjectGroupPython] Si_element001  label="Si_element : 0.004"  # scripted group (container) (typed FeaturePython)
  n = 0.003973
FEATURE [App::DocumentObjectGroupPython] G4_C_552  label="G4_C-552"  # scripted group (container) (typed FeaturePython)
  Dunit = g/cm3
  Dvalue = 1.76
  Group = -> [H_element020,C_element021,O_element019,F_element004,Si_element001]
  conduct = 2
  density = 1
  expand = 3
  formula = G4_C-552
  name = G4_C-552
  specific = 4
FEATURE [App::DocumentObjectGroupPython] Cd_element001  label="Cd_element : 1"  # scripted group (container) (typed FeaturePython)
  n = 1
  ref = Cd_element
FEATURE [App::DocumentObjectGroupPython] Te_element001  label="Te_element : 1"  # scripted group (container) (typed FeaturePython)
  n = 1
  ref = Te_element
FEATURE [App::DocumentObjectGroupPython] G4_CADMIUM_TELLURIDE  # scripted group (container) (typed FeaturePython)
  Dunit = g/cm3
  Dvalue = 6.2
  Group = -> [Cd_element001,Te_element001]
  conduct = 2
  density = 1
  expand = 3
  formula = G4_CADMIUM_TELLURIDE
  name = G4_CADMIUM_TELLURIDE
  specific = 4
FEATURE [App::DocumentObjectGroupPython] Cd_element002  label="Cd_element : 002"  # scripted group (container) (typed FeaturePython)
  n = 1
  ref = Cd_element
FEATURE [App::DocumentObjectGroupPython] W_element001  label="W_element : 1"  # scripted group (container) (typed FeaturePython)
  n = 1
  ref = W_element
FEATURE [App::DocumentObjectGroupPython] O_element020  label="O_element : 008"  # scripted group (container) (typed FeaturePython)
  n = 4
  ref = O_element
FEATURE [App::DocumentObjectGroupPython] G4_CADMIUM_TUNGSTATE  # scripted group (container) (typed FeaturePython)
  Dunit = g/cm3
  Dvalue = 7.9
  Group = -> [Cd_element002,W_element001,O_element020]
  conduct = 2
  density = 1
  expand = 3
  formula = G4_CADMIUM_TUNGSTATE
  name = G4_CADMIUM_TUNGSTATE
  specific = 4
FEATURE [App::DocumentObjectGroupPython] Ca_element005  label="Ca_element : 1"  # scripted group (container) (typed FeaturePython)
  n = 1
  ref = Ca_element
FEATURE [App::DocumentObjectGroupPython] C_element022  label="C_element : 009"  # scripted group (container) (typed FeaturePython)
  n = 1
  ref = C_element
FEATURE [App::DocumentObjectGroupPython] O_element021  label="O_element : 009"  # scripted group (container) (typed FeaturePython)
  n = 3
  ref = O_element
FEATURE [App::DocumentObjectGroupPython] G4_CALCIUM_CARBONATE  # scripted group (container) (typed FeaturePython)
  Dunit = g/cm3
  Dvalue = 2.8
  Group = -> [Ca_element005,C_element022,O_element021]
  conduct = 2
  density = 1
  expand = 3
  formula = G4_CALCIUM_CARBONATE
  name = G4_CALCIUM_CARBONATE
  specific = 4
FEATURE [App::DocumentObjectGroupPython] Ca_element006  label="Ca_element : 002"  # scripted group (container) (typed FeaturePython)
  n = 1
  ref = Ca_element
FEATURE [App::DocumentObjectGroupPython] F_element005  label="F_element : 003"  # scripted group (container) (typed FeaturePython)
  n = 2
  ref = F_element
FEATURE [App::DocumentObjectGroupPython] G4_CALCIUM_FLUORIDE  # scripted group (container) (typed FeaturePython)
  Dunit = g/cm3
  Dvalue = 3.18
  Group = -> [Ca_element006,F_element005]
  conduct = 2
  density = 1
  expand = 3
  formula = G4_CALCIUM_FLUORIDE
  name = G4_CALCIUM_FLUORIDE
  specific = 4
FEATURE [App::DocumentObjectGroupPython] Ca_element007  label="Ca_element : 003"  # scripted group (container) (typed FeaturePython)
  n = 1
  ref = Ca_element
FEATURE [App::DocumentObjectGroupPython] O_element022  label="O_element : 010"  # scripted group (container) (typed FeaturePython)
  n = 1
  ref = O_element
FEATURE [App::DocumentObjectGroupPython] G4_CALCIUM_OXIDE  # scripted group (container) (typed FeaturePython)
  Dunit = g/cm3
  Dvalue = 3.3
  Group = -> [Ca_element007,O_element022]
  conduct = 2
  density = 1
  expand = 3
  formula = G4_CALCIUM_OXIDE
  name = G4_CALCIUM_OXIDE
  specific = 4
FEATURE [App::DocumentObjectGroupPython] Ca_element008  label="Ca_element : 004"  # scripted group (container) (typed FeaturePython)
  n = 1
  ref = Ca_element
FEATURE [App::DocumentObjectGroupPython] S_element007  label="S_element : 002"  # scripted group (container) (typed FeaturePython)
  n = 1
  ref = S_element
FEATURE [App::DocumentObjectGroupPython] O_element023  label="O_element : 011"  # scripted group (container) (typed FeaturePython)
  n = 4
  ref = O_element
FEATURE [App::DocumentObjectGroupPython] G4_CALCIUM_SULFATE  # scripted group (container) (typed FeaturePython)
  Dunit = g/cm3
  Dvalue = 2.96
  Group = -> [Ca_element008,S_element007,O_element023]
  conduct = 2
  density = 1
  expand = 3
  formula = G4_CALCIUM_SULFATE
  name = G4_CALCIUM_SULFATE
  specific = 4
FEATURE [App::DocumentObjectGroupPython] Ca_element009  label="Ca_element : 005"  # scripted group (container) (typed FeaturePython)
  n = 1
  ref = Ca_element
FEATURE [App::DocumentObjectGroupPython] W_element002  label="W_element : 002"  # scripted group (container) (typed FeaturePython)
  n = 1
  ref = W_element
FEATURE [App::DocumentObjectGroupPython] O_element024  label="O_element : 012"  # scripted group (container) (typed FeaturePython)
  n = 4
  ref = O_element
FEATURE [App::DocumentObjectGroupPython] G4_CALCIUM_TUNGSTATE  # scripted group (container) (typed FeaturePython)
  Dunit = g/cm3
  Dvalue = 6.062
  Group = -> [Ca_element009,W_element002,O_element024]
  conduct = 2
  density = 1
  expand = 3
  formula = G4_CALCIUM_TUNGSTATE
  name = G4_CALCIUM_TUNGSTATE
  specific = 4
FEATURE [App::DocumentObjectGroupPython] C_element023  label="C_element : 010"  # scripted group (container) (typed FeaturePython)
  n = 1
  ref = C_element
FEATURE [App::DocumentObjectGroupPython] O_element025  label="O_element : 013"  # scripted group (container) (typed FeaturePython)
  n = 2
  ref = O_element
FEATURE [App::DocumentObjectGroupPython] G4_CARBON_DIOXIDE  # scripted group (container) (typed FeaturePython)
  Dunit = g/cm3
  Dvalue = 0.00184212
  Group = -> [C_element023,O_element025]
  conduct = 2
  density = 1
  expand = 3
  formula = G4_CARBON_DIOXIDE
  name = G4_CARBON_DIOXIDE
  specific = 4
FEATURE [App::DocumentObjectGroupPython] C_element024  label="C_element : 011"  # scripted group (container) (typed FeaturePython)
  n = 1
  ref = C_element
FEATURE [App::DocumentObjectGroupPython] Cl_element004  label="Cl_element : 4"  # scripted group (container) (typed FeaturePython)
  n = 4
  ref = Cl_element
FEATURE [App::DocumentObjectGroupPython] G4_CARBON_TETRACHLORIDE  # scripted group (container) (typed FeaturePython)
  Dunit = g/cm3
  Dvalue = 1.594
  Group = -> [C_element024,Cl_element004]
  conduct = 2
  density = 1
  expand = 3
  formula = G4_CARBON_TETRACHLORIDE
  name = G4_CARBON_TETRACHLORIDE
  specific = 4
FEATURE [App::DocumentObjectGroupPython] C_element025  label="C_element : 012"  # scripted group (container) (typed FeaturePython)
  n = 6
  ref = C_element
FEATURE [App::DocumentObjectGroupPython] H_element021  label="H_element : 012"  # scripted group (container) (typed FeaturePython)
  n = 10
  ref = H_element
FEATURE [App::DocumentObjectGroupPython] O_element026  label="O_element : 5"  # scripted group (container) (typed FeaturePython)
  n = 5
  ref = O_element
FEATURE [App::DocumentObjectGroupPython] G4_CELLULOSE_CELLOPHANE  # scripted group (container) (typed FeaturePython)
  Dunit = g/cm3
  Dvalue = 1.42
  Group = -> [C_element025,H_element021,O_element026]
  conduct = 2
  density = 1
  expand = 3
  formula = G4_CELLULOSE_CELLOPHANE
  name = G4_CELLULOSE_CELLOPHANE
  specific = 4
FEATURE [App::DocumentObjectGroupPython] H_element022  label="H_element : 0.067"  # scripted group (container) (typed FeaturePython)
  n = 0.067125
FEATURE [App::DocumentObjectGroupPython] C_element026  label="C_element : 0.545"  # scripted group (container) (typed FeaturePython)
  n = 0.545403
FEATURE [App::DocumentObjectGroupPython] O_element027  label="O_element : 0.387"  # scripted group (container) (typed FeaturePython)
  n = 0.387472
FEATURE [App::DocumentObjectGroupPython] G4_CELLULOSE_BUTYRATE  # scripted group (container) (typed FeaturePython)
  Dunit = g/cm3
  Dvalue = 1.2
  Group = -> [H_element022,C_element026,O_element027]
  conduct = 2
  density = 1
  expand = 3
  formula = G4_CELLULOSE_BUTYRATE
  name = G4_CELLULOSE_BUTYRATE
  specific = 4
FEATURE [App::DocumentObjectGroupPython] H_element023  label="H_element : 0.029"  # scripted group (container) (typed FeaturePython)
  n = 0.029216
FEATURE [App::DocumentObjectGroupPython] C_element027  label="C_element : 0.271"  # scripted group (container) (typed FeaturePython)
  n = 0.271296
FEATURE [App::DocumentObjectGroupPython] N_element013  label="N_element : 0.121"  # scripted group (container) (typed FeaturePython)
  n = 0.121276
FEATURE [App::DocumentObjectGroupPython] O_element028  label="O_element : 0.578"  # scripted group (container) (typed FeaturePython)
  n = 0.578212
FEATURE [App::DocumentObjectGroupPython] G4_CELLULOSE_NITRATE  # scripted group (container) (typed FeaturePython)
  Dunit = g/cm3
  Dvalue = 1.49
  Group = -> [H_element023,C_element027,N_element013,O_element028]
  conduct = 2
  density = 1
  expand = 3
  formula = G4_CELLULOSE_NITRATE
  name = G4_CELLULOSE_NITRATE
  specific = 4
FEATURE [App::DocumentObjectGroupPython] H_element024  label="H_element : 0.108"  # scripted group (container) (typed FeaturePython)
  n = 0.107596
FEATURE [App::DocumentObjectGroupPython] N_element014  label="N_element : 0.001"  # scripted group (container) (typed FeaturePython)
  n = 0.0008
FEATURE [App::DocumentObjectGroupPython] O_element029  label="O_element : 0.875"  # scripted group (container) (typed FeaturePython)
  n = 0.874976
FEATURE [App::DocumentObjectGroupPython] S_element008  label="S_element : 0.015"  # scripted group (container) (typed FeaturePython)
  n = 0.014627
FEATURE [App::DocumentObjectGroupPython] Ce_element001  label="Ce_element : 0.002"  # scripted group (container) (typed FeaturePython)
  n = 0.002001
FEATURE [App::DocumentObjectGroupPython] G4_CERIC_SULFATE  # scripted group (container) (typed FeaturePython)
  Dunit = g/cm3
  Dvalue = 1.03
  Group = -> [H_element024,N_element014,O_element029,S_element008,Ce_element001]
  conduct = 2
  density = 1
  expand = 3
  formula = G4_CERIC_SULFATE
  name = G4_CERIC_SULFATE
  specific = 4
FEATURE [App::DocumentObjectGroupPython] Cs_element001  label="Cs_element : 1"  # scripted group (container) (typed FeaturePython)
  n = 1
  ref = Cs_element
FEATURE [App::DocumentObjectGroupPython] F_element006  label="F_element : 1"  # scripted group (container) (typed FeaturePython)
  n = 1
  ref = F_element
FEATURE [App::DocumentObjectGroupPython] G4_CESIUM_FLUORIDE  # scripted group (container) (typed FeaturePython)
  Dunit = g/cm3
  Dvalue = 4.115
  Group = -> [Cs_element001,F_element006]
  conduct = 2
  density = 1
  expand = 3
  formula = G4_CESIUM_FLUORIDE
  name = G4_CESIUM_FLUORIDE
  specific = 4
FEATURE [App::DocumentObjectGroupPython] Cs_element002  label="Cs_element : 002"  # scripted group (container) (typed FeaturePython)
  n = 1
  ref = Cs_element
FEATURE [App::DocumentObjectGroupPython] I_element001  label="I_element : 1"  # scripted group (container) (typed FeaturePython)
  n = 1
  ref = I_element
FEATURE [App::DocumentObjectGroupPython] G4_CESIUM_IODIDE  # scripted group (container) (typed FeaturePython)
  Dunit = g/cm3
  Dvalue = 4.51
  Group = -> [Cs_element002,I_element001]
  conduct = 2
  density = 1
  expand = 3
  formula = G4_CESIUM_IODIDE
  name = G4_CESIUM_IODIDE
  specific = 4
FEATURE [App::DocumentObjectGroupPython] C_element028  label="C_element : 013"  # scripted group (container) (typed FeaturePython)
  n = 6
  ref = C_element
FEATURE [App::DocumentObjectGroupPython] H_element025  label="H_element : 013"  # scripted group (container) (typed FeaturePython)
  n = 5
  ref = H_element
FEATURE [App::DocumentObjectGroupPython] Cl_element005  label="Cl_element : 1"  # scripted group (container) (typed FeaturePython)
  n = 1
  ref = Cl_element
FEATURE [App::DocumentObjectGroupPython] G4_CHLOROBENZENE  # scripted group (container) (typed FeaturePython)
  Dunit = g/cm3
  Dvalue = 1.1058
  Group = -> [C_element028,H_element025,Cl_element005]
  conduct = 2
  density = 1
  expand = 3
  formula = G4_CHLOROBENZENE
  name = G4_CHLOROBENZENE
  specific = 4
FEATURE [App::DocumentObjectGroupPython] C_element029  label="C_element : 014"  # scripted group (container) (typed FeaturePython)
  n = 1
  ref = C_element
FEATURE [App::DocumentObjectGroupPython] H_element026  label="H_element : 1"  # scripted group (container) (typed FeaturePython)
  n = 1
  ref = H_element
FEATURE [App::DocumentObjectGroupPython] Cl_element006  label="Cl_element : 3"  # scripted group (container) (typed FeaturePython)
  n = 3
  ref = Cl_element
FEATURE [App::DocumentObjectGroupPython] G4_CHLOROFORM  # scripted group (container) (typed FeaturePython)
  Dunit = g/cm3
  Dvalue = 1.4832
  Group = -> [C_element029,H_element026,Cl_element006]
  conduct = 2
  density = 1
  expand = 3
  formula = G4_CHLOROFORM
  name = G4_CHLOROFORM
  specific = 4
FEATURE [App::DocumentObjectGroupPython] H_element027  label="H_element : 0.010"  # scripted group (container) (typed FeaturePython)
  n = 0.01
FEATURE [App::DocumentObjectGroupPython] C_element030  label="C_element : 0.001"  # scripted group (container) (typed FeaturePython)
  n = 0.001
FEATURE [App::DocumentObjectGroupPython] O_element030  label="O_element : 0.529"  # scripted group (container) (typed FeaturePython)
  n = 0.529107
FEATURE [App::DocumentObjectGroupPython] Na_element005  label="Na_element : 0.016"  # scripted group (container) (typed FeaturePython)
  n = 0.016
FEATURE [App::DocumentObjectGroupPython] Mg_element003  label="Mg_element : 0.004"  # scripted group (container) (typed FeaturePython)
  n = 0.002
FEATURE [App::DocumentObjectGroupPython] Al_element002  label="Al_element : 0.034"  # scripted group (container) (typed FeaturePython)
  n = 0.033872
FEATURE [App::DocumentObjectGroupPython] Si_element002  label="Si_element : 0.337"  # scripted group (container) (typed FeaturePython)
  n = 0.337021
FEATURE [App::DocumentObjectGroupPython] K_element003  label="K_element : 0.013"  # scripted group (container) (typed FeaturePython)
  n = 0.013
FEATURE [App::DocumentObjectGroupPython] Ca_element010  label="Ca_element : 0.044"  # scripted group (container) (typed FeaturePython)
  n = 0.044
FEATURE [App::DocumentObjectGroupPython] Fe_element002  label="Fe_element : 0.014"  # scripted group (container) (typed FeaturePython)
  n = 0.014
FEATURE [App::DocumentObjectGroupPython] G4_CONCRETE  # scripted group (container) (typed FeaturePython)
  Dunit = g/cm3
  Dvalue = 2.3
  Group = -> [H_element027,C_element030,O_element030,Na_element005,Mg_element003,Al_element002,Si_element002,K_element003,Ca_element010,Fe_element002]
  conduct = 2
  density = 1
  expand = 3
  formula = G4_CONCRETE
  name = G4_CONCRETE
  specific = 4
FEATURE [App::DocumentObjectGroupPython] C_element031  label="C_element : 015"  # scripted group (container) (typed FeaturePython)
  n = 6
  ref = C_element
FEATURE [App::DocumentObjectGroupPython] H_element028  label="H_element : 12"  # scripted group (container) (typed FeaturePython)
  n = 12
  ref = H_element
FEATURE [App::DocumentObjectGroupPython] G4_CYCLOHEXANE  # scripted group (container) (typed FeaturePython)
  Dunit = g/cm3
  Dvalue = 0.779
  Group = -> [C_element031,H_element028]
  conduct = 2
  density = 1
  expand = 3
  formula = G4_CYCLOHEXANE
  name = G4_CYCLOHEXANE
  specific = 4
FEATURE [App::DocumentObjectGroupPython] C_element032  label="C_element : 016"  # scripted group (container) (typed FeaturePython)
  n = 6
  ref = C_element
FEATURE [App::DocumentObjectGroupPython] H_element029  label="H_element : 4"  # scripted group (container) (typed FeaturePython)
  n = 4
  ref = H_element
FEATURE [App::DocumentObjectGroupPython] Cl_element007  label="Cl_element : 2"  # scripted group (container) (typed FeaturePython)
  n = 2
  ref = Cl_element
FEATURE [App::DocumentObjectGroupPython] G4_1_2_DICHLOROBENZENE  label="G4_1.2-DICHLOROBENZENE"  # scripted group (container) (typed FeaturePython)
  Dunit = g/cm3
  Dvalue = 1.3048
  Group = -> [C_element032,H_element029,Cl_element007]
  conduct = 2
  density = 1
  expand = 3
  formula = G4_1.2-DICHLOROBENZENE
  name = G4_1.2-DICHLOROBENZENE
  specific = 4
FEATURE [App::DocumentObjectGroupPython] C_element033  label="C_element : 017"  # scripted group (container) (typed FeaturePython)
  n = 4
  ref = C_element
FEATURE [App::DocumentObjectGroupPython] H_element030  label="H_element : 8"  # scripted group (container) (typed FeaturePython)
  n = 8
  ref = H_element
FEATURE [App::DocumentObjectGroupPython] O_element031  label="O_element : 014"  # scripted group (container) (typed FeaturePython)
  n = 1
  ref = O_element
FEATURE [App::DocumentObjectGroupPython] Cl_element008  label="Cl_element : 005"  # scripted group (container) (typed FeaturePython)
  n = 2
  ref = Cl_element
FEATURE [App::DocumentObjectGroupPython] G4_DICHLORODIETHYL_ETHER  # scripted group (container) (typed FeaturePython)
  Dunit = g/cm3
  Dvalue = 1.2199
  Group = -> [C_element033,H_element030,O_element031,Cl_element008]
  conduct = 2
  density = 1
  expand = 3
  formula = G4_DICHLORODIETHYL_ETHER
  name = G4_DICHLORODIETHYL_ETHER
  specific = 4
FEATURE [App::DocumentObjectGroupPython] C_element034  label="C_element : 018"  # scripted group (container) (typed FeaturePython)
  n = 2
  ref = C_element
FEATURE [App::DocumentObjectGroupPython] H_element031  label="H_element : 014"  # scripted group (container) (typed FeaturePython)
  n = 4
  ref = H_element
FEATURE [App::DocumentObjectGroupPython] Cl_element009  label="Cl_element : 006"  # scripted group (container) (typed FeaturePython)
  n = 2
  ref = Cl_element
FEATURE [App::DocumentObjectGroupPython] G4_1_2_DICHLOROETHANE  label="G4_1.2-DICHLOROETHANE"  # scripted group (container) (typed FeaturePython)
  Dunit = g/cm3
  Dvalue = 1.2351
  Group = -> [C_element034,H_element031,Cl_element009]
  conduct = 2
  density = 1
  expand = 3
  formula = G4_1.2-DICHLOROETHANE
  name = G4_1.2-DICHLOROETHANE
  specific = 4
FEATURE [App::DocumentObjectGroupPython] C_element035  label="C_element : 019"  # scripted group (container) (typed FeaturePython)
  n = 4
  ref = C_element
FEATURE [App::DocumentObjectGroupPython] H_element032  label="H_element : 015"  # scripted group (container) (typed FeaturePython)
  n = 10
  ref = H_element
FEATURE [App::DocumentObjectGroupPython] O_element032  label="O_element : 015"  # scripted group (container) (typed FeaturePython)
  n = 1
  ref = O_element
FEATURE [App::DocumentObjectGroupPython] G4_DIETHYL_ETHER  # scripted group (container) (typed FeaturePython)
  Dunit = g/cm3
  Dvalue = 0.71378
  Group = -> [C_element035,H_element032,O_element032]
  conduct = 2
  density = 1
  expand = 3
  formula = G4_DIETHYL_ETHER
  name = G4_DIETHYL_ETHER
  specific = 4
FEATURE [App::DocumentObjectGroupPython] C_element036  label="C_element : 020"  # scripted group (container) (typed FeaturePython)
  n = 3
  ref = C_element
FEATURE [App::DocumentObjectGroupPython] H_element033  label="H_element : 016"  # scripted group (container) (typed FeaturePython)
  n = 7
  ref = H_element
FEATURE [App::DocumentObjectGroupPython] N_element015  label="N_element : 008"  # scripted group (container) (typed FeaturePython)
  n = 1
  ref = N_element
FEATURE [App::DocumentObjectGroupPython] O_element033  label="O_element : 016"  # scripted group (container) (typed FeaturePython)
  n = 1
  ref = O_element
FEATURE [App::DocumentObjectGroupPython] G4_N_N_DIMETHYL_FORMAMIDE  label="G4_N.N-DIMETHYL_FORMAMIDE"  # scripted group (container) (typed FeaturePython)
  Dunit = g/cm3
  Dvalue = 0.9487
  Group = -> [C_element036,H_element033,N_element015,O_element033]
  conduct = 2
  density = 1
  expand = 3
  formula = G4_N.N-DIMETHYL_FORMAMIDE
  name = G4_N.N-DIMETHYL_FORMAMIDE
  specific = 4
FEATURE [App::DocumentObjectGroupPython] C_element037  label="C_element : 021"  # scripted group (container) (typed FeaturePython)
  n = 2
  ref = C_element
FEATURE [App::DocumentObjectGroupPython] H_element034  label="H_element : 017"  # scripted group (container) (typed FeaturePython)
  n = 6
  ref = H_element
FEATURE [App::DocumentObjectGroupPython] O_element034  label="O_element : 017"  # scripted group (container) (typed FeaturePython)
  n = 1
  ref = O_element
FEATURE [App::DocumentObjectGroupPython] S_element009  label="S_element : 003"  # scripted group (container) (typed FeaturePython)
  n = 1
  ref = S_element
FEATURE [App::DocumentObjectGroupPython] G4_DIMETHYL_SULFOXIDE  # scripted group (container) (typed FeaturePython)
  Dunit = g/cm3
  Dvalue = 1.1014
  Group = -> [C_element037,H_element034,O_element034,S_element009]
  conduct = 2
  density = 1
  expand = 3
  formula = G4_DIMETHYL_SULFOXIDE
  name = G4_DIMETHYL_SULFOXIDE
  specific = 4
FEATURE [App::DocumentObjectGroupPython] C_element038  label="C_element : 022"  # scripted group (container) (typed FeaturePython)
  n = 2
  ref = C_element
FEATURE [App::DocumentObjectGroupPython] H_element035  label="H_element : 018"  # scripted group (container) (typed FeaturePython)
  n = 6
  ref = H_element
FEATURE [App::DocumentObjectGroupPython] G4_ETHANE  # scripted group (container) (typed FeaturePython)
  Dunit = g/cm3
  Dvalue = 0.00125324
  Group = -> [C_element038,H_element035]
  conduct = 2
  density = 1
  expand = 3
  formula = G4_ETHANE
  name = G4_ETHANE
  specific = 4
FEATURE [App::DocumentObjectGroupPython] C_element039  label="C_element : 023"  # scripted group (container) (typed FeaturePython)
  n = 2
  ref = C_element
FEATURE [App::DocumentObjectGroupPython] H_element036  label="H_element : 019"  # scripted group (container) (typed FeaturePython)
  n = 6
  ref = H_element
FEATURE [App::DocumentObjectGroupPython] O_element035  label="O_element : 018"  # scripted group (container) (typed FeaturePython)
  n = 1
  ref = O_element
FEATURE [App::DocumentObjectGroupPython] G4_ETHYL_ALCOHOL  # scripted group (container) (typed FeaturePython)
  Dunit = g/cm3
  Dvalue = 0.7893
  Group = -> [C_element039,H_element036,O_element035]
  conduct = 2
  density = 1
  expand = 3
  formula = G4_ETHYL_ALCOHOL
  name = G4_ETHYL_ALCOHOL
  specific = 4
FEATURE [App::DocumentObjectGroupPython] H_element037  label="H_element : 0.090"  # scripted group (container) (typed FeaturePython)
  n = 0.090027
FEATURE [App::DocumentObjectGroupPython] C_element040  label="C_element : 0.585"  # scripted group (container) (typed FeaturePython)
  n = 0.585182
FEATURE [App::DocumentObjectGroupPython] O_element036  label="O_element : 0.325"  # scripted group (container) (typed FeaturePython)
  n = 0.324791
FEATURE [App::DocumentObjectGroupPython] G4_ETHYL_CELLULOSE  # scripted group (container) (typed FeaturePython)
  Dunit = g/cm3
  Dvalue = 1.13
  Group = -> [H_element037,C_element040,O_element036]
  conduct = 2
  density = 1
  expand = 3
  formula = G4_ETHYL_CELLULOSE
  name = G4_ETHYL_CELLULOSE
  specific = 4
FEATURE [App::DocumentObjectGroupPython] C_element041  label="C_element : 024"  # scripted group (container) (typed FeaturePython)
  n = 2
  ref = C_element
FEATURE [App::DocumentObjectGroupPython] H_element038  label="H_element : 020"  # scripted group (container) (typed FeaturePython)
  n = 4
  ref = H_element
FEATURE [App::DocumentObjectGroupPython] G4_ETHYLENE  # scripted group (container) (typed FeaturePython)
  Dunit = g/cm3
  Dvalue = 0.00117497
  Group = -> [C_element041,H_element038]
  conduct = 2
  density = 1
  expand = 3
  formula = G4_ETHYLENE
  name = G4_ETHYLENE
  specific = 4
FEATURE [App::DocumentObjectGroupPython] H_element039  label="H_element : 0.096"  # scripted group (container) (typed FeaturePython)
  n = 0.096
FEATURE [App::DocumentObjectGroupPython] C_element042  label="C_element : 0.195"  # scripted group (container) (typed FeaturePython)
  n = 0.195
FEATURE [App::DocumentObjectGroupPython] N_element016  label="N_element : 0.057"  # scripted group (container) (typed FeaturePython)
  n = 0.057
FEATURE [App::DocumentObjectGroupPython] O_element037  label="O_element : 0.646"  # scripted group (container) (typed FeaturePython)
  n = 0.646
FEATURE [App::DocumentObjectGroupPython] Na_element006  label="Na_element : 0.017"  # scripted group (container) (typed FeaturePython)
  n = 0.001
FEATURE [App::DocumentObjectGroupPython] P_element005  label="P_element : 0.104"  # scripted group (container) (typed FeaturePython)
  n = 0.001
FEATURE [App::DocumentObjectGroupPython] S_element010  label="S_element : 0.016"  # scripted group (container) (typed FeaturePython)
  n = 0.003
FEATURE [App::DocumentObjectGroupPython] Cl_element010  label="Cl_element : 0.005"  # scripted group (container) (typed FeaturePython)
  n = 0.001
FEATURE [App::DocumentObjectGroupPython] G4_EYE_LENS_ICRP  # scripted group (container) (typed FeaturePython)
  Dunit = g/cm3
  Dvalue = 1.07
  Group = -> [H_element039,C_element042,N_element016,O_element037,Na_element006,P_element005,S_element010,Cl_element010]
  conduct = 2
  density = 1
  expand = 3
  formula = G4_EYE_LENS_ICRP
  name = G4_EYE_LENS_ICRP
  specific = 4
FEATURE [App::DocumentObjectGroupPython] Fe_element003  label="Fe_element : 2"  # scripted group (container) (typed FeaturePython)
  n = 2
  ref = Fe_element
FEATURE [App::DocumentObjectGroupPython] O_element038  label="O_element : 019"  # scripted group (container) (typed FeaturePython)
  n = 3
  ref = O_element
FEATURE [App::DocumentObjectGroupPython] G4_FERRIC_OXIDE  # scripted group (container) (typed FeaturePython)
  Dunit = g/cm3
  Dvalue = 5.2
  Group = -> [Fe_element003,O_element038]
  conduct = 2
  density = 1
  expand = 3
  formula = G4_FERRIC_OXIDE
  name = G4_FERRIC_OXIDE
  specific = 4
FEATURE [App::DocumentObjectGroupPython] Fe_element004  label="Fe_element : 1"  # scripted group (container) (typed FeaturePython)
  n = 1
  ref = Fe_element
FEATURE [App::DocumentObjectGroupPython] B_element003  label="B_element : 1"  # scripted group (container) (typed FeaturePython)
  n = 1
  ref = B_element
FEATURE [App::DocumentObjectGroupPython] G4_FERROBORIDE  # scripted group (container) (typed FeaturePython)
  Dunit = g/cm3
  Dvalue = 7.15
  Group = -> [Fe_element004,B_element003]
  conduct = 2
  density = 1
  expand = 3
  formula = G4_FERROBORIDE
  name = G4_FERROBORIDE
  specific = 4
FEATURE [App::DocumentObjectGroupPython] Fe_element005  label="Fe_element : 003"  # scripted group (container) (typed FeaturePython)
  n = 1
  ref = Fe_element
FEATURE [App::DocumentObjectGroupPython] O_element039  label="O_element : 020"  # scripted group (container) (typed FeaturePython)
  n = 1
  ref = O_element
FEATURE [App::DocumentObjectGroupPython] G4_FERROUS_OXIDE  # scripted group (container) (typed FeaturePython)
  Dunit = g/cm3
  Dvalue = 5.7
  Group = -> [Fe_element005,O_element039]
  conduct = 2
  density = 1
  expand = 3
  formula = G4_FERROUS_OXIDE
  name = G4_FERROUS_OXIDE
  specific = 4
FEATURE [App::DocumentObjectGroupPython] H_element040  label="H_element : 0.115"  # scripted group (container) (typed FeaturePython)
  n = 0.108259
FEATURE [App::DocumentObjectGroupPython] N_element017  label="N_element : 0.000"  # scripted group (container) (typed FeaturePython)
  n = 2.7e-05
FEATURE [App::DocumentObjectGroupPython] O_element040  label="O_element : 0.879"  # scripted group (container) (typed FeaturePython)
  n = 0.878636
FEATURE [App::DocumentObjectGroupPython] Na_element007  label="Na_element : 0.000"  # scripted group (container) (typed FeaturePython)
  n = 2.2e-05
FEATURE [App::DocumentObjectGroupPython] S_element011  label="S_element : 0.013"  # scripted group (container) (typed FeaturePython)
  n = 0.012968
FEATURE [App::DocumentObjectGroupPython] Cl_element011  label="Cl_element : 0.000"  # scripted group (container) (typed FeaturePython)
  n = 3.4e-05
FEATURE [App::DocumentObjectGroupPython] Fe_element006  label="Fe_element : 0.000"  # scripted group (container) (typed FeaturePython)
  n = 5.4e-05
FEATURE [App::DocumentObjectGroupPython] G4_FERROUS_SULFATE  # scripted group (container) (typed FeaturePython)
  Dunit = g/cm3
  Dvalue = 1.024
  Group = -> [H_element040,N_element017,O_element040,Na_element007,S_element011,Cl_element011,Fe_element006]
  conduct = 2
  density = 1
  expand = 3
  formula = G4_FERROUS_SULFATE
  name = G4_FERROUS_SULFATE
  specific = 4
FEATURE [App::DocumentObjectGroupPython] C_element043  label="C_element : 0.099"  # scripted group (container) (typed FeaturePython)
  n = 0.099335
FEATURE [App::DocumentObjectGroupPython] F_element007  label="F_element : 0.314"  # scripted group (container) (typed FeaturePython)
  n = 0.314247
FEATURE [App::DocumentObjectGroupPython] Cl_element012  label="Cl_element : 0.586"  # scripted group (container) (typed FeaturePython)
  n = 0.586418
FEATURE [App::DocumentObjectGroupPython] G4_FREON_12  label="G4_FREON-12"  # scripted group (container) (typed FeaturePython)
  Dunit = g/cm3
  Dvalue = 1.12
  Group = -> [C_element043,F_element007,Cl_element012]
  conduct = 2
  density = 1
  expand = 3
  formula = G4_FREON-12
  name = G4_FREON-12
  specific = 4
FEATURE [App::DocumentObjectGroupPython] C_element044  label="C_element : 0.057"  # scripted group (container) (typed FeaturePython)
  n = 0.057245
FEATURE [App::DocumentObjectGroupPython] F_element008  label="F_element : 0.181"  # scripted group (container) (typed FeaturePython)
  n = 0.181096
FEATURE [App::DocumentObjectGroupPython] Br_element001  label="Br_element : 0.762"  # scripted group (container) (typed FeaturePython)
  n = 0.761659
FEATURE [App::DocumentObjectGroupPython] G4_FREON_12B2  label="G4_FREON-12B2"  # scripted group (container) (typed FeaturePython)
  Dunit = g/cm3
  Dvalue = 1.8
  Group = -> [C_element044,F_element008,Br_element001]
  conduct = 2
  density = 1
  expand = 3
  formula = G4_FREON-12B2
  name = G4_FREON-12B2
  specific = 4
FEATURE [App::DocumentObjectGroupPython] C_element045  label="C_element : 0.115"  # scripted group (container) (typed FeaturePython)
  n = 0.114983
FEATURE [App::DocumentObjectGroupPython] F_element009  label="F_element : 0.546"  # scripted group (container) (typed FeaturePython)
  n = 0.545621
FEATURE [App::DocumentObjectGroupPython] Cl_element013  label="Cl_element : 0.339"  # scripted group (container) (typed FeaturePython)
  n = 0.339396
FEATURE [App::DocumentObjectGroupPython] G4_FREON_13  label="G4_FREON-13"  # scripted group (container) (typed FeaturePython)
  Dunit = g/cm3
  Dvalue = 0.95
  Group = -> [C_element045,F_element009,Cl_element013]
  conduct = 2
  density = 1
  expand = 3
  formula = G4_FREON-13
  name = G4_FREON-13
  specific = 4
FEATURE [App::DocumentObjectGroupPython] C_element046  label="C_element : 025"  # scripted group (container) (typed FeaturePython)
  n = 1
  ref = C_element
FEATURE [App::DocumentObjectGroupPython] F_element010  label="F_element : 3"  # scripted group (container) (typed FeaturePython)
  n = 3
  ref = F_element
FEATURE [App::DocumentObjectGroupPython] Br_element002  label="Br_element : 1"  # scripted group (container) (typed FeaturePython)
  n = 1
  ref = Br_element
FEATURE [App::DocumentObjectGroupPython] G4_FREON_13B1  label="G4_FREON-13B1"  # scripted group (container) (typed FeaturePython)
  Dunit = g/cm3
  Dvalue = 1.5
  Group = -> [C_element046,F_element010,Br_element002]
  conduct = 2
  density = 1
  expand = 3
  formula = G4_FREON-13B1
  name = G4_FREON-13B1
  specific = 4
FEATURE [App::DocumentObjectGroupPython] C_element047  label="C_element : 0.061"  # scripted group (container) (typed FeaturePython)
  n = 0.061309
FEATURE [App::DocumentObjectGroupPython] F_element011  label="F_element : 0.291"  # scripted group (container) (typed FeaturePython)
  n = 0.290924
FEATURE [App::DocumentObjectGroupPython] I_element002  label="I_element : 0.648"  # scripted group (container) (typed FeaturePython)
  n = 0.647767
FEATURE [App::DocumentObjectGroupPython] G4_FREON_13I1  label="G4_FREON-13I1"  # scripted group (container) (typed FeaturePython)
  Dunit = g/cm3
  Dvalue = 1.8
  Group = -> [C_element047,F_element011,I_element002]
  conduct = 2
  density = 1
  expand = 3
  formula = G4_FREON-13I1
  name = G4_FREON-13I1
  specific = 4
FEATURE [App::DocumentObjectGroupPython] Gd_element001  label="Gd_element : 2"  # scripted group (container) (typed FeaturePython)
  n = 2
  ref = Gd_element
FEATURE [App::DocumentObjectGroupPython] O_element041  label="O_element : 021"  # scripted group (container) (typed FeaturePython)
  n = 2
  ref = O_element
FEATURE [App::DocumentObjectGroupPython] S_element012  label="S_element : 004"  # scripted group (container) (typed FeaturePython)
  n = 1
  ref = S_element
FEATURE [App::DocumentObjectGroupPython] G4_GADOLINIUM_OXYSULFIDE  # scripted group (container) (typed FeaturePython)
  Dunit = g/cm3
  Dvalue = 7.44
  Group = -> [Gd_element001,O_element041,S_element012]
  conduct = 2
  density = 1
  expand = 3
  formula = G4_GADOLINIUM_OXYSULFIDE
  name = G4_GADOLINIUM_OXYSULFIDE
  specific = 4
FEATURE [App::DocumentObjectGroupPython] Ga_element001  label="Ga_element : 1"  # scripted group (container) (typed FeaturePython)
  n = 1
  ref = Ga_element
FEATURE [App::DocumentObjectGroupPython] As_element001  label="As_element : 1"  # scripted group (container) (typed FeaturePython)
  n = 1
  ref = As_element
FEATURE [App::DocumentObjectGroupPython] G4_GALLIUM_ARSENIDE  # scripted group (container) (typed FeaturePython)
  Dunit = g/cm3
  Dvalue = 5.31
  Group = -> [Ga_element001,As_element001]
  conduct = 2
  density = 1
  expand = 3
  formula = G4_GALLIUM_ARSENIDE
  name = G4_GALLIUM_ARSENIDE
  specific = 4
FEATURE [App::DocumentObjectGroupPython] H_element041  label="H_element : 0.081"  # scripted group (container) (typed FeaturePython)
  n = 0.08118
FEATURE [App::DocumentObjectGroupPython] C_element048  label="C_element : 0.416"  # scripted group (container) (typed FeaturePython)
  n = 0.41606
FEATURE [App::DocumentObjectGroupPython] N_element018  label="N_element : 0.111"  # scripted group (container) (typed FeaturePython)
  n = 0.11124
FEATURE [App::DocumentObjectGroupPython] O_element042  label="O_element : 0.381"  # scripted group (container) (typed FeaturePython)
  n = 0.38064
FEATURE [App::DocumentObjectGroupPython] S_element013  label="S_element : 0.011"  # scripted group (container) (typed FeaturePython)
  n = 0.01088
FEATURE [App::DocumentObjectGroupPython] G4_GEL_PHOTO_EMULSION  # scripted group (container) (typed FeaturePython)
  Dunit = g/cm3
  Dvalue = 1.2914
  Group = -> [H_element041,C_element048,N_element018,O_element042,S_element013]
  conduct = 2
  density = 1
  expand = 3
  formula = G4_GEL_PHOTO_EMULSION
  name = G4_GEL_PHOTO_EMULSION
  specific = 4
FEATURE [App::DocumentObjectGroupPython] B_element004  label="B_element : 0.040"  # scripted group (container) (typed FeaturePython)
  n = 0.0400639
FEATURE [App::DocumentObjectGroupPython] O_element043  label="O_element : 0.540"  # scripted group (container) (typed FeaturePython)
  n = 0.539561
FEATURE [App::DocumentObjectGroupPython] Na_element008  label="Na_element : 0.028"  # scripted group (container) (typed FeaturePython)
  n = 0.0281909
FEATURE [App::DocumentObjectGroupPython] Al_element003  label="Al_element : 0.012"  # scripted group (container) (typed FeaturePython)
  n = 0.011644
FEATURE [App::DocumentObjectGroupPython] Si_element003  label="Si_element : 0.377"  # scripted group (container) (typed FeaturePython)
  n = 0.377219
FEATURE [App::DocumentObjectGroupPython] K_element004  label="K_element : 0.014"  # scripted group (container) (typed FeaturePython)
  n = 0.00332099
FEATURE [App::DocumentObjectGroupPython] G4_Pyrex_Glass  # scripted group (container) (typed FeaturePython)
  Dunit = g/cm3
  Dvalue = 2.23
  Group = -> [B_element004,O_element043,Na_element008,Al_element003,Si_element003,K_element004]
  conduct = 2
  density = 1
  expand = 3
  formula = G4_Pyrex_Glass
  name = G4_Pyrex_Glass
  specific = 4
FEATURE [App::DocumentObjectGroupPython] O_element044  label="O_element : 0.156"  # scripted group (container) (typed FeaturePython)
  n = 0.156453
FEATURE [App::DocumentObjectGroupPython] Si_element004  label="Si_element : 0.081"  # scripted group (container) (typed FeaturePython)
  n = 0.080866
FEATURE [App::DocumentObjectGroupPython] Ti_element001  label="Ti_element : 0.008"  # scripted group (container) (typed FeaturePython)
  n = 0.008092
FEATURE [App::DocumentObjectGroupPython] As_element002  label="As_element : 0.003"  # scripted group (container) (typed FeaturePython)
  n = 0.002651
FEATURE [App::DocumentObjectGroupPython] Pb_element001  label="Pb_element : 0.752"  # scripted group (container) (typed FeaturePython)
  n = 0.751938
FEATURE [App::DocumentObjectGroupPython] G4_GLASS_LEAD  # scripted group (container) (typed FeaturePython)
  Dunit = g/cm3
  Dvalue = 6.22
  Group = -> [O_element044,Si_element004,Ti_element001,As_element002,Pb_element001]
  conduct = 2
  density = 1
  expand = 3
  formula = G4_GLASS_LEAD
  name = G4_GLASS_LEAD
  specific = 4
FEATURE [App::DocumentObjectGroupPython] O_element045  label="O_element : 0.460"  # scripted group (container) (typed FeaturePython)
  n = 0.4598
FEATURE [App::DocumentObjectGroupPython] Na_element009  label="Na_element : 0.096"  # scripted group (container) (typed FeaturePython)
  n = 0.0964411
FEATURE [App::DocumentObjectGroupPython] Si_element005  label="Si_element : 0.378"  # scripted group (container) (typed FeaturePython)
  n = 0.336553
FEATURE [App::DocumentObjectGroupPython] Ca_element011  label="Ca_element : 0.107"  # scripted group (container) (typed FeaturePython)
  n = 0.107205
FEATURE [App::DocumentObjectGroupPython] G4_GLASS_PLATE  # scripted group (container) (typed FeaturePython)
  Dunit = g/cm3
  Dvalue = 2.4
  Group = -> [O_element045,Na_element009,Si_element005,Ca_element011]
  conduct = 2
  density = 1
  expand = 3
  formula = G4_GLASS_PLATE
  name = G4_GLASS_PLATE
  specific = 4
FEATURE [App::DocumentObjectGroupPython] C_element049  label="C_element : 026"  # scripted group (container) (typed FeaturePython)
  n = 5
  ref = C_element
FEATURE [App::DocumentObjectGroupPython] H_element042  label="H_element : 021"  # scripted group (container) (typed FeaturePython)
  n = 10
  ref = H_element
FEATURE [App::DocumentObjectGroupPython] N_element019  label="N_element : 2"  # scripted group (container) (typed FeaturePython)
  n = 2
  ref = N_element
FEATURE [App::DocumentObjectGroupPython] O_element046  label="O_element : 022"  # scripted group (container) (typed FeaturePython)
  n = 3
  ref = O_element
FEATURE [App::DocumentObjectGroupPython] G4_GLUTAMINE  # scripted group (container) (typed FeaturePython)
  Dunit = g/cm3
  Dvalue = 1.46
  Group = -> [C_element049,H_element042,N_element019,O_element046]
  conduct = 2
  density = 1
  expand = 3
  formula = G4_GLUTAMINE
  name = G4_GLUTAMINE
  specific = 4
FEATURE [App::DocumentObjectGroupPython] C_element050  label="C_element : 027"  # scripted group (container) (typed FeaturePython)
  n = 3
  ref = C_element
FEATURE [App::DocumentObjectGroupPython] H_element043  label="H_element : 022"  # scripted group (container) (typed FeaturePython)
  n = 8
  ref = H_element
FEATURE [App::DocumentObjectGroupPython] O_element047  label="O_element : 023"  # scripted group (container) (typed FeaturePython)
  n = 3
  ref = O_element
FEATURE [App::DocumentObjectGroupPython] G4_GLYCEROL  # scripted group (container) (typed FeaturePython)
  Dunit = g/cm3
  Dvalue = 1.2613
  Group = -> [C_element050,H_element043,O_element047]
  conduct = 2
  density = 1
  expand = 3
  formula = G4_GLYCEROL
  name = G4_GLYCEROL
  specific = 4
FEATURE [App::DocumentObjectGroupPython] C_element051  label="C_element : 028"  # scripted group (container) (typed FeaturePython)
  n = 5
  ref = C_element
FEATURE [App::DocumentObjectGroupPython] H_element044  label="H_element : 023"  # scripted group (container) (typed FeaturePython)
  n = 5
  ref = H_element
FEATURE [App::DocumentObjectGroupPython] N_element020  label="N_element : 009"  # scripted group (container) (typed FeaturePython)
  n = 5
  ref = N_element
FEATURE [App::DocumentObjectGroupPython] O_element048  label="O_element : 024"  # scripted group (container) (typed FeaturePython)
  n = 1
  ref = O_element
FEATURE [App::DocumentObjectGroupPython] G4_GUANINE  # scripted group (container) (typed FeaturePython)
  Dunit = g/cm3
  Dvalue = 2.2
  Group = -> [C_element051,H_element044,N_element020,O_element048]
  conduct = 2
  density = 1
  expand = 3
  formula = G4_GUANINE
  name = G4_GUANINE
  specific = 4
FEATURE [App::DocumentObjectGroupPython] Ca_element012  label="Ca_element : 006"  # scripted group (container) (typed FeaturePython)
  n = 1
  ref = Ca_element
FEATURE [App::DocumentObjectGroupPython] S_element014  label="S_element : 005"  # scripted group (container) (typed FeaturePython)
  n = 1
  ref = S_element
FEATURE [App::DocumentObjectGroupPython] O_element049  label="O_element : 6"  # scripted group (container) (typed FeaturePython)
  n = 6
  ref = O_element
FEATURE [App::DocumentObjectGroupPython] H_element045  label="H_element : 024"  # scripted group (container) (typed FeaturePython)
  n = 4
  ref = H_element
FEATURE [App::DocumentObjectGroupPython] G4_GYPSUM  # scripted group (container) (typed FeaturePython)
  Dunit = g/cm3
  Dvalue = 2.32
  Group = -> [Ca_element012,S_element014,O_element049,H_element045]
  conduct = 2
  density = 1
  expand = 3
  formula = G4_GYPSUM
  name = G4_GYPSUM
  specific = 4
FEATURE [App::DocumentObjectGroupPython] C_element052  label="C_element : 7"  # scripted group (container) (typed FeaturePython)
  n = 7
  ref = C_element
FEATURE [App::DocumentObjectGroupPython] H_element046  label="H_element : 16"  # scripted group (container) (typed FeaturePython)
  n = 16
  ref = H_element
FEATURE [App::DocumentObjectGroupPython] G4_N_HEPTANE  label="G4_N-HEPTANE"  # scripted group (container) (typed FeaturePython)
  Dunit = g/cm3
  Dvalue = 0.68376
  Group = -> [C_element052,H_element046]
  conduct = 2
  density = 1
  expand = 3
  formula = G4_N-HEPTANE
  name = G4_N-HEPTANE
  specific = 4
FEATURE [App::DocumentObjectGroupPython] C_element053  label="C_element : 029"  # scripted group (container) (typed FeaturePython)
  n = 6
  ref = C_element
FEATURE [App::DocumentObjectGroupPython] H_element047  label="H_element : 14"  # scripted group (container) (typed FeaturePython)
  n = 14
  ref = H_element
FEATURE [App::DocumentObjectGroupPython] G4_N_HEXANE  label="G4_N-HEXANE"  # scripted group (container) (typed FeaturePython)
  Dunit = g/cm3
  Dvalue = 0.6603
  Group = -> [C_element053,H_element047]
  conduct = 2
  density = 1
  expand = 3
  formula = G4_N-HEXANE
  name = G4_N-HEXANE
  specific = 4
FEATURE [App::DocumentObjectGroupPython] C_element054  label="C_element : 22"  # scripted group (container) (typed FeaturePython)
  n = 22
  ref = C_element
FEATURE [App::DocumentObjectGroupPython] H_element048  label="H_element : 025"  # scripted group (container) (typed FeaturePython)
  n = 10
  ref = H_element
FEATURE [App::DocumentObjectGroupPython] N_element021  label="N_element : 010"  # scripted group (container) (typed FeaturePython)
  n = 2
  ref = N_element
FEATURE [App::DocumentObjectGroupPython] O_element050  label="O_element : 025"  # scripted group (container) (typed FeaturePython)
  n = 5
  ref = O_element
FEATURE [App::DocumentObjectGroupPython] G4_KAPTON  # scripted group (container) (typed FeaturePython)
  Dunit = g/cm3
  Dvalue = 1.42
  Group = -> [C_element054,H_element048,N_element021,O_element050]
  conduct = 2
  density = 1
  expand = 3
  formula = G4_KAPTON
  name = G4_KAPTON
  specific = 4
FEATURE [App::DocumentObjectGroupPython] La_element001  label="La_element : 1"  # scripted group (container) (typed FeaturePython)
  n = 1
  ref = La_element
FEATURE [App::DocumentObjectGroupPython] Br_element003  label="Br_element : 002"  # scripted group (container) (typed FeaturePython)
  n = 1
  ref = Br_element
FEATURE [App::DocumentObjectGroupPython] O_element051  label="O_element : 026"  # scripted group (container) (typed FeaturePython)
  n = 1
  ref = O_element
FEATURE [App::DocumentObjectGroupPython] G4_LANTHANUM_OXYBROMIDE  # scripted group (container) (typed FeaturePython)
  Dunit = g/cm3
  Dvalue = 6.28
  Group = -> [La_element001,Br_element003,O_element051]
  conduct = 2
  density = 1
  expand = 3
  formula = G4_LANTHANUM_OXYBROMIDE
  name = G4_LANTHANUM_OXYBROMIDE
  specific = 4
FEATURE [App::DocumentObjectGroupPython] La_element002  label="La_element : 2"  # scripted group (container) (typed FeaturePython)
  n = 2
  ref = La_element
FEATURE [App::DocumentObjectGroupPython] O_element052  label="O_element : 027"  # scripted group (container) (typed FeaturePython)
  n = 2
  ref = O_element
FEATURE [App::DocumentObjectGroupPython] S_element015  label="S_element : 006"  # scripted group (container) (typed FeaturePython)
  n = 1
  ref = S_element
FEATURE [App::DocumentObjectGroupPython] G4_LANTHANUM_OXYSULFIDE  # scripted group (container) (typed FeaturePython)
  Dunit = g/cm3
  Dvalue = 5.86
  Group = -> [La_element002,O_element052,S_element015]
  conduct = 2
  density = 1
  expand = 3
  formula = G4_LANTHANUM_OXYSULFIDE
  name = G4_LANTHANUM_OXYSULFIDE
  specific = 4
FEATURE [App::DocumentObjectGroupPython] O_element053  label="O_element : 0.072"  # scripted group (container) (typed FeaturePython)
  n = 0.071682
FEATURE [App::DocumentObjectGroupPython] Pb_element002  label="Pb_element : 0.928"  # scripted group (container) (typed FeaturePython)
  n = 0.928318
FEATURE [App::DocumentObjectGroupPython] G4_LEAD_OXIDE  # scripted group (container) (typed FeaturePython)
  Dunit = g/cm3
  Dvalue = 9.53
  Group = -> [O_element053,Pb_element002]
  conduct = 2
  density = 1
  expand = 3
  formula = G4_LEAD_OXIDE
  name = G4_LEAD_OXIDE
  specific = 4
FEATURE [App::DocumentObjectGroupPython] Li_element001  label="Li_element : 1"  # scripted group (container) (typed FeaturePython)
  n = 1
  ref = Li_element
FEATURE [App::DocumentObjectGroupPython] N_element022  label="N_element : 011"  # scripted group (container) (typed FeaturePython)
  n = 1
  ref = N_element
FEATURE [App::DocumentObjectGroupPython] H_element049  label="H_element : 026"  # scripted group (container) (typed FeaturePython)
  n = 2
  ref = H_element
FEATURE [App::DocumentObjectGroupPython] G4_LITHIUM_AMIDE  # scripted group (container) (typed FeaturePython)
  Dunit = g/cm3
  Dvalue = 1.178
  Group = -> [Li_element001,N_element022,H_element049]
  conduct = 2
  density = 1
  expand = 3
  formula = G4_LITHIUM_AMIDE
  name = G4_LITHIUM_AMIDE
  specific = 4
FEATURE [App::DocumentObjectGroupPython] Li_element002  label="Li_element : 2"  # scripted group (container) (typed FeaturePython)
  n = 2
  ref = Li_element
FEATURE [App::DocumentObjectGroupPython] C_element055  label="C_element : 030"  # scripted group (container) (typed FeaturePython)
  n = 1
  ref = C_element
FEATURE [App::DocumentObjectGroupPython] O_element054  label="O_element : 028"  # scripted group (container) (typed FeaturePython)
  n = 3
  ref = O_element
FEATURE [App::DocumentObjectGroupPython] G4_LITHIUM_CARBONATE  # scripted group (container) (typed FeaturePython)
  Dunit = g/cm3
  Dvalue = 2.11
  Group = -> [Li_element002,C_element055,O_element054]
  conduct = 2
  density = 1
  expand = 3
  formula = G4_LITHIUM_CARBONATE
  name = G4_LITHIUM_CARBONATE
  specific = 4
FEATURE [App::DocumentObjectGroupPython] Li_element003  label="Li_element : 003"  # scripted group (container) (typed FeaturePython)
  n = 1
  ref = Li_element
FEATURE [App::DocumentObjectGroupPython] F_element012  label="F_element : 004"  # scripted group (container) (typed FeaturePython)
  n = 1
  ref = F_element
FEATURE [App::DocumentObjectGroupPython] G4_LITHIUM_FLUORIDE  # scripted group (container) (typed FeaturePython)
  Dunit = g/cm3
  Dvalue = 2.635
  Group = -> [Li_element003,F_element012]
  conduct = 2
  density = 1
  expand = 3
  formula = G4_LITHIUM_FLUORIDE
  name = G4_LITHIUM_FLUORIDE
  specific = 4
FEATURE [App::DocumentObjectGroupPython] Li_element004  label="Li_element : 004"  # scripted group (container) (typed FeaturePython)
  n = 1
  ref = Li_element
FEATURE [App::DocumentObjectGroupPython] H_element050  label="H_element : 027"  # scripted group (container) (typed FeaturePython)
  n = 1
  ref = H_element
FEATURE [App::DocumentObjectGroupPython] G4_LITHIUM_HYDRIDE  # scripted group (container) (typed FeaturePython)
  Dunit = g/cm3
  Dvalue = 0.82
  Group = -> [Li_element004,H_element050]
  conduct = 2
  density = 1
  expand = 3
  formula = G4_LITHIUM_HYDRIDE
  name = G4_LITHIUM_HYDRIDE
  specific = 4
FEATURE [App::DocumentObjectGroupPython] Li_element005  label="Li_element : 005"  # scripted group (container) (typed FeaturePython)
  n = 1
  ref = Li_element
FEATURE [App::DocumentObjectGroupPython] I_element003  label="I_element : 002"  # scripted group (container) (typed FeaturePython)
  n = 1
  ref = I_element
FEATURE [App::DocumentObjectGroupPython] G4_LITHIUM_IODIDE  # scripted group (container) (typed FeaturePython)
  Dunit = g/cm3
  Dvalue = 3.494
  Group = -> [Li_element005,I_element003]
  conduct = 2
  density = 1
  expand = 3
  formula = G4_LITHIUM_IODIDE
  name = G4_LITHIUM_IODIDE
  specific = 4
FEATURE [App::DocumentObjectGroupPython] Li_element006  label="Li_element : 006"  # scripted group (container) (typed FeaturePython)
  n = 2
  ref = Li_element
FEATURE [App::DocumentObjectGroupPython] O_element055  label="O_element : 029"  # scripted group (container) (typed FeaturePython)
  n = 1
  ref = O_element
FEATURE [App::DocumentObjectGroupPython] G4_LITHIUM_OXIDE  # scripted group (container) (typed FeaturePython)
  Dunit = g/cm3
  Dvalue = 2.013
  Group = -> [Li_element006,O_element055]
  conduct = 2
  density = 1
  expand = 3
  formula = G4_LITHIUM_OXIDE
  name = G4_LITHIUM_OXIDE
  specific = 4
FEATURE [App::DocumentObjectGroupPython] Li_element007  label="Li_element : 007"  # scripted group (container) (typed FeaturePython)
  n = 2
  ref = Li_element
FEATURE [App::DocumentObjectGroupPython] B_element005  label="B_element : 005"  # scripted group (container) (typed FeaturePython)
  n = 4
  ref = B_element
FEATURE [App::DocumentObjectGroupPython] O_element056  label="O_element : 7"  # scripted group (container) (typed FeaturePython)
  n = 7
  ref = O_element
FEATURE [App::DocumentObjectGroupPython] G4_LITHIUM_TETRABORATE  # scripted group (container) (typed FeaturePython)
  Dunit = g/cm3
  Dvalue = 2.44
  Group = -> [Li_element007,B_element005,O_element056]
  conduct = 2
  density = 1
  expand = 3
  formula = G4_LITHIUM_TETRABORATE
  name = G4_LITHIUM_TETRABORATE
  specific = 4
FEATURE [App::DocumentObjectGroupPython] H_element051  label="H_element : 0.105"  # scripted group (container) (typed FeaturePython)
  n = 0.105
FEATURE [App::DocumentObjectGroupPython] C_element056  label="C_element : 0.083"  # scripted group (container) (typed FeaturePython)
  n = 0.083
FEATURE [App::DocumentObjectGroupPython] N_element023  label="N_element : 0.023"  # scripted group (container) (typed FeaturePython)
  n = 0.023
FEATURE [App::DocumentObjectGroupPython] O_element057  label="O_element : 0.779"  # scripted group (container) (typed FeaturePython)
  n = 0.779
FEATURE [App::DocumentObjectGroupPython] Na_element010  label="Na_element : 0.097"  # scripted group (container) (typed FeaturePython)
  n = 0.002
FEATURE [App::DocumentObjectGroupPython] P_element006  label="P_element : 0.105"  # scripted group (container) (typed FeaturePython)
  n = 0.001
FEATURE [App::DocumentObjectGroupPython] S_element016  label="S_element : 0.017"  # scripted group (container) (typed FeaturePython)
  n = 0.002
FEATURE [App::DocumentObjectGroupPython] Cl_element014  label="Cl_element : 0.587"  # scripted group (container) (typed FeaturePython)
  n = 0.003
FEATURE [App::DocumentObjectGroupPython] K_element005  label="K_element : 0.015"  # scripted group (container) (typed FeaturePython)
  n = 0.002
FEATURE [App::DocumentObjectGroupPython] G4_LUNG_ICRP  # scripted group (container) (typed FeaturePython)
  Dunit = g/cm3
  Dvalue = 1.04
  Group = -> [H_element051,C_element056,N_element023,O_element057,Na_element010,P_element006,S_element016,Cl_element014,K_element005]
  conduct = 2
  density = 1
  expand = 3
  formula = G4_LUNG_ICRP
  name = G4_LUNG_ICRP
  specific = 4
FEATURE [App::DocumentObjectGroupPython] H_element052  label="H_element : 0.116"  # scripted group (container) (typed FeaturePython)
  n = 0.114318
FEATURE [App::DocumentObjectGroupPython] C_element057  label="C_element : 0.656"  # scripted group (container) (typed FeaturePython)
  n = 0.655824
FEATURE [App::DocumentObjectGroupPython] O_element058  label="O_element : 0.092"  # scripted group (container) (typed FeaturePython)
  n = 0.0921831
FEATURE [App::DocumentObjectGroupPython] Mg_element004  label="Mg_element : 0.135"  # scripted group (container) (typed FeaturePython)
  n = 0.134792
FEATURE [App::DocumentObjectGroupPython] Ca_element013  label="Ca_element : 0.003"  # scripted group (container) (typed FeaturePython)
  n = 0.002883
FEATURE [App::DocumentObjectGroupPython] G4_M3_WAX  # scripted group (container) (typed FeaturePython)
  Dunit = g/cm3
  Dvalue = 1.05
  Group = -> [H_element052,C_element057,O_element058,Mg_element004,Ca_element013]
  conduct = 2
  density = 1
  expand = 3
  formula = G4_M3_WAX
  name = G4_M3_WAX
  specific = 4
FEATURE [App::DocumentObjectGroupPython] Mg_element005  label="Mg_element : 1"  # scripted group (container) (typed FeaturePython)
  n = 1
  ref = Mg_element
FEATURE [App::DocumentObjectGroupPython] C_element058  label="C_element : 031"  # scripted group (container) (typed FeaturePython)
  n = 1
  ref = C_element
FEATURE [App::DocumentObjectGroupPython] O_element059  label="O_element : 030"  # scripted group (container) (typed FeaturePython)
  n = 3
  ref = O_element
FEATURE [App::DocumentObjectGroupPython] G4_MAGNESIUM_CARBONATE  # scripted group (container) (typed FeaturePython)
  Dunit = g/cm3
  Dvalue = 2.958
  Group = -> [Mg_element005,C_element058,O_element059]
  conduct = 2
  density = 1
  expand = 3
  formula = G4_MAGNESIUM_CARBONATE
  name = G4_MAGNESIUM_CARBONATE
  specific = 4
FEATURE [App::DocumentObjectGroupPython] Mg_element006  label="Mg_element : 002"  # scripted group (container) (typed FeaturePython)
  n = 1
  ref = Mg_element
FEATURE [App::DocumentObjectGroupPython] F_element013  label="F_element : 005"  # scripted group (container) (typed FeaturePython)
  n = 2
  ref = F_element
FEATURE [App::DocumentObjectGroupPython] G4_MAGNESIUM_FLUORIDE  # scripted group (container) (typed FeaturePython)
  Dunit = g/cm3
  Dvalue = 3
  Group = -> [Mg_element006,F_element013]
  conduct = 2
  density = 1
  expand = 3
  formula = G4_MAGNESIUM_FLUORIDE
  name = G4_MAGNESIUM_FLUORIDE
  specific = 4
FEATURE [App::DocumentObjectGroupPython] Mg_element007  label="Mg_element : 003"  # scripted group (container) (typed FeaturePython)
  n = 1
  ref = Mg_element
FEATURE [App::DocumentObjectGroupPython] O_element060  label="O_element : 031"  # scripted group (container) (typed FeaturePython)
  n = 1
  ref = O_element
FEATURE [App::DocumentObjectGroupPython] G4_MAGNESIUM_OXIDE  # scripted group (container) (typed FeaturePython)
  Dunit = g/cm3
  Dvalue = 3.58
  Group = -> [Mg_element007,O_element060]
  conduct = 2
  density = 1
  expand = 3
  formula = G4_MAGNESIUM_OXIDE
  name = G4_MAGNESIUM_OXIDE
  specific = 4
FEATURE [App::DocumentObjectGroupPython] Mg_element008  label="Mg_element : 004"  # scripted group (container) (typed FeaturePython)
  n = 1
  ref = Mg_element
FEATURE [App::DocumentObjectGroupPython] B_element006  label="B_element : 006"  # scripted group (container) (typed FeaturePython)
  n = 4
  ref = B_element
FEATURE [App::DocumentObjectGroupPython] O_element061  label="O_element : 032"  # scripted group (container) (typed FeaturePython)
  n = 7
  ref = O_element
FEATURE [App::DocumentObjectGroupPython] G4_MAGNESIUM_TETRABORATE  # scripted group (container) (typed FeaturePython)
  Dunit = g/cm3
  Dvalue = 2.53
  Group = -> [Mg_element008,B_element006,O_element061]
  conduct = 2
  density = 1
  expand = 3
  formula = G4_MAGNESIUM_TETRABORATE
  name = G4_MAGNESIUM_TETRABORATE
  specific = 4
FEATURE [App::DocumentObjectGroupPython] Hg_element001  label="Hg_element : 1"  # scripted group (container) (typed FeaturePython)
  n = 1
  ref = Hg_element
FEATURE [App::DocumentObjectGroupPython] I_element004  label="I_element : 2"  # scripted group (container) (typed FeaturePython)
  n = 2
  ref = I_element
FEATURE [App::DocumentObjectGroupPython] G4_MERCURIC_IODIDE  # scripted group (container) (typed FeaturePython)
  Dunit = g/cm3
  Dvalue = 6.36
  Group = -> [Hg_element001,I_element004]
  conduct = 2
  density = 1
  expand = 3
  formula = G4_MERCURIC_IODIDE
  name = G4_MERCURIC_IODIDE
  specific = 4
FEATURE [App::DocumentObjectGroupPython] C_element059  label="C_element : 032"  # scripted group (container) (typed FeaturePython)
  n = 1
  ref = C_element
FEATURE [App::DocumentObjectGroupPython] H_element053  label="H_element : 028"  # scripted group (container) (typed FeaturePython)
  n = 4
  ref = H_element
FEATURE [App::DocumentObjectGroupPython] G4_METHANE  # scripted group (container) (typed FeaturePython)
  Dunit = g/cm3
  Dvalue = 0.000667151
  Group = -> [C_element059,H_element053]
  conduct = 2
  density = 1
  expand = 3
  formula = G4_METHANE
  name = G4_METHANE
  specific = 4
FEATURE [App::DocumentObjectGroupPython] C_element060  label="C_element : 033"  # scripted group (container) (typed FeaturePython)
  n = 1
  ref = C_element
FEATURE [App::DocumentObjectGroupPython] H_element054  label="H_element : 029"  # scripted group (container) (typed FeaturePython)
  n = 4
  ref = H_element
FEATURE [App::DocumentObjectGroupPython] O_element062  label="O_element : 033"  # scripted group (container) (typed FeaturePython)
  n = 1
  ref = O_element
FEATURE [App::DocumentObjectGroupPython] G4_METHANOL  # scripted group (container) (typed FeaturePython)
  Dunit = g/cm3
  Dvalue = 0.7914
  Group = -> [C_element060,H_element054,O_element062]
  conduct = 2
  density = 1
  expand = 3
  formula = G4_METHANOL
  name = G4_METHANOL
  specific = 4
FEATURE [App::DocumentObjectGroupPython] H_element055  label="H_element : 0.134"  # scripted group (container) (typed FeaturePython)
  n = 0.13404
FEATURE [App::DocumentObjectGroupPython] C_element061  label="C_element : 0.778"  # scripted group (container) (typed FeaturePython)
  n = 0.77796
FEATURE [App::DocumentObjectGroupPython] O_element063  label="O_element : 0.035"  # scripted group (container) (typed FeaturePython)
  n = 0.03502
FEATURE [App::DocumentObjectGroupPython] Mg_element009  label="Mg_element : 0.039"  # scripted group (container) (typed FeaturePython)
  n = 0.038594
FEATURE [App::DocumentObjectGroupPython] Ti_element002  label="Ti_element : 0.014"  # scripted group (container) (typed FeaturePython)
  n = 0.014386
FEATURE [App::DocumentObjectGroupPython] G4_MIX_D_WAX  # scripted group (container) (typed FeaturePython)
  Dunit = g/cm3
  Dvalue = 0.99
  Group = -> [H_element055,C_element061,O_element063,Mg_element009,Ti_element002]
  conduct = 2
  density = 1
  expand = 3
  formula = G4_MIX_D_WAX
  name = G4_MIX_D_WAX
  specific = 4
FEATURE [App::DocumentObjectGroupPython] H_element056  label="H_element : 0.135"  # scripted group (container) (typed FeaturePython)
  n = 0.081192
FEATURE [App::DocumentObjectGroupPython] C_element062  label="C_element : 0.583"  # scripted group (container) (typed FeaturePython)
  n = 0.583442
FEATURE [App::DocumentObjectGroupPython] N_element024  label="N_element : 0.018"  # scripted group (container) (typed FeaturePython)
  n = 0.017798
FEATURE [App::DocumentObjectGroupPython] O_element064  label="O_element : 0.186"  # scripted group (container) (typed FeaturePython)
  n = 0.186381
FEATURE [App::DocumentObjectGroupPython] Mg_element010  label="Mg_element : 0.130"  # scripted group (container) (typed FeaturePython)
  n = 0.130287
FEATURE [App::DocumentObjectGroupPython] Cl_element015  label="Cl_element : 0.588"  # scripted group (container) (typed FeaturePython)
  n = 0.0009
FEATURE [App::DocumentObjectGroupPython] G4_MS20_TISSUE  # scripted group (container) (typed FeaturePython)
  Dunit = g/cm3
  Dvalue = 1
  Group = -> [H_element056,C_element062,N_element024,O_element064,Mg_element010,Cl_element015]
  conduct = 2
  density = 1
  expand = 3
  formula = G4_MS20_TISSUE
  name = G4_MS20_TISSUE
  specific = 4
FEATURE [App::DocumentObjectGroupPython] H_element057  label="H_element : 0.136"  # scripted group (container) (typed FeaturePython)
  n = 0.102
FEATURE [App::DocumentObjectGroupPython] C_element063  label="C_element : 0.143"  # scripted group (container) (typed FeaturePython)
  n = 0.143
FEATURE [App::DocumentObjectGroupPython] N_element025  label="N_element : 0.034"  # scripted group (container) (typed FeaturePython)
  n = 0.034
FEATURE [App::DocumentObjectGroupPython] O_element065  label="O_element : 0.710"  # scripted group (container) (typed FeaturePython)
  n = 0.71
FEATURE [App::DocumentObjectGroupPython] Na_element011  label="Na_element : 0.098"  # scripted group (container) (typed FeaturePython)
  n = 0.001
FEATURE [App::DocumentObjectGroupPython] P_element007  label="P_element : 0.002"  # scripted group (container) (typed FeaturePython)
  n = 0.002
FEATURE [App::DocumentObjectGroupPython] S_element017  label="S_element : 0.018"  # scripted group (container) (typed FeaturePython)
  n = 0.003
FEATURE [App::DocumentObjectGroupPython] Cl_element016  label="Cl_element : 0.589"  # scripted group (container) (typed FeaturePython)
  n = 0.001
FEATURE [App::DocumentObjectGroupPython] K_element006  label="K_element : 0.004"  # scripted group (container) (typed FeaturePython)
  n = 0.004
FEATURE [App::DocumentObjectGroupPython] G4_MUSCLE_SKELETAL_ICRP  # scripted group (container) (typed FeaturePython)
  Dunit = g/cm3
  Dvalue = 1.05
  Group = -> [H_element057,C_element063,N_element025,O_element065,Na_element011,P_element007,S_element017,Cl_element016,K_element006]
  conduct = 2
  density = 1
  expand = 3
  formula = G4_MUSCLE_SKELETAL_ICRP
  name = G4_MUSCLE_SKELETAL_ICRP
  specific = 4
FEATURE [App::DocumentObjectGroupPython] H_element058  label="H_element : 0.137"  # scripted group (container) (typed FeaturePython)
  n = 0.102102
FEATURE [App::DocumentObjectGroupPython] C_element064  label="C_element : 0.123"  # scripted group (container) (typed FeaturePython)
  n = 0.123123
FEATURE [App::DocumentObjectGroupPython] N_element026  label="N_element : 0.756"  # scripted group (container) (typed FeaturePython)
  n = 0.035035
FEATURE [App::DocumentObjectGroupPython] O_element066  label="O_element : 0.730"  # scripted group (container) (typed FeaturePython)
  n = 0.72973
FEATURE [App::DocumentObjectGroupPython] Na_element012  label="Na_element : 0.099"  # scripted group (container) (typed FeaturePython)
  n = 0.001001
FEATURE [App::DocumentObjectGroupPython] P_element008  label="P_element : 0.106"  # scripted group (container) (typed FeaturePython)
  n = 0.002002
FEATURE [App::DocumentObjectGroupPython] S_element018  label="S_element : 0.019"  # scripted group (container) (typed FeaturePython)
  n = 0.004004
FEATURE [App::DocumentObjectGroupPython] K_element007  label="K_element : 0.016"  # scripted group (container) (typed FeaturePython)
  n = 0.003003
FEATURE [App::DocumentObjectGroupPython] G4_MUSCLE_STRIATED_ICRU  # scripted group (container) (typed FeaturePython)
  Dunit = g/cm3
  Dvalue = 1.04
  Group = -> [H_element058,C_element064,N_element026,O_element066,Na_element012,P_element008,S_element018,K_element007]
  conduct = 2
  density = 1
  expand = 3
  formula = G4_MUSCLE_STRIATED_ICRU
  name = G4_MUSCLE_STRIATED_ICRU
  specific = 4
FEATURE [App::DocumentObjectGroupPython] H_element059  label="H_element : 0.098"  # scripted group (container) (typed FeaturePython)
  n = 0.0982341
FEATURE [App::DocumentObjectGroupPython] C_element065  label="C_element : 0.156"  # scripted group (container) (typed FeaturePython)
  n = 0.156214
FEATURE [App::DocumentObjectGroupPython] N_element027  label="N_element : 0.757"  # scripted group (container) (typed FeaturePython)
  n = 0.035451
FEATURE [App::DocumentObjectGroupPython] O_element067  label="O_element : 0.880"  # scripted group (container) (typed FeaturePython)
  n = 0.710101
FEATURE [App::DocumentObjectGroupPython] G4_MUSCLE_WITH_SUCROSE  # scripted group (container) (typed FeaturePython)
  Dunit = g/cm3
  Dvalue = 1.11
  Group = -> [H_element059,C_element065,N_element027,O_element067]
  conduct = 2
  density = 1
  expand = 3
  formula = G4_MUSCLE_WITH_SUCROSE
  name = G4_MUSCLE_WITH_SUCROSE
  specific = 4
FEATURE [App::DocumentObjectGroupPython] H_element060  label="H_element : 0.138"  # scripted group (container) (typed FeaturePython)
  n = 0.101969
FEATURE [App::DocumentObjectGroupPython] C_element066  label="C_element : 0.120"  # scripted group (container) (typed FeaturePython)
  n = 0.120058
FEATURE [App::DocumentObjectGroupPython] N_element028  label="N_element : 0.758"  # scripted group (container) (typed FeaturePython)
  n = 0.035451
FEATURE [App::DocumentObjectGroupPython] O_element068  label="O_element : 0.743"  # scripted group (container) (typed FeaturePython)
  n = 0.742522
FEATURE [App::DocumentObjectGroupPython] G4_MUSCLE_WITHOUT_SUCROSE  # scripted group (container) (typed FeaturePython)
  Dunit = g/cm3
  Dvalue = 1.07
  Group = -> [H_element060,C_element066,N_element028,O_element068]
  conduct = 2
  density = 1
  expand = 3
  formula = G4_MUSCLE_WITHOUT_SUCROSE
  name = G4_MUSCLE_WITHOUT_SUCROSE
  specific = 4
FEATURE [App::DocumentObjectGroupPython] C_element067  label="C_element : 10"  # scripted group (container) (typed FeaturePython)
  n = 10
  ref = C_element
FEATURE [App::DocumentObjectGroupPython] H_element061  label="H_element : 030"  # scripted group (container) (typed FeaturePython)
  n = 8
  ref = H_element
FEATURE [App::DocumentObjectGroupPython] G4_NAPHTHALENE  # scripted group (container) (typed FeaturePython)
  Dunit = g/cm3
  Dvalue = 1.145
  Group = -> [C_element067,H_element061]
  conduct = 2
  density = 1
  expand = 3
  formula = G4_NAPHTHALENE
  name = G4_NAPHTHALENE
  specific = 4
FEATURE [App::DocumentObjectGroupPython] C_element068  label="C_element : 034"  # scripted group (container) (typed FeaturePython)
  n = 6
  ref = C_element
FEATURE [App::DocumentObjectGroupPython] H_element062  label="H_element : 031"  # scripted group (container) (typed FeaturePython)
  n = 5
  ref = H_element
FEATURE [App::DocumentObjectGroupPython] N_element029  label="N_element : 012"  # scripted group (container) (typed FeaturePython)
  n = 1
  ref = N_element
FEATURE [App::DocumentObjectGroupPython] O_element069  label="O_element : 034"  # scripted group (container) (typed FeaturePython)
  n = 2
  ref = O_element
FEATURE [App::DocumentObjectGroupPython] G4_NITROBENZENE  # scripted group (container) (typed FeaturePython)
  Dunit = g/cm3
  Dvalue = 1.19867
  Group = -> [C_element068,H_element062,N_element029,O_element069]
  conduct = 2
  density = 1
  expand = 3
  formula = G4_NITROBENZENE
  name = G4_NITROBENZENE
  specific = 4
FEATURE [App::DocumentObjectGroupPython] N_element030  label="N_element : 013"  # scripted group (container) (typed FeaturePython)
  n = 2
  ref = N_element
FEATURE [App::DocumentObjectGroupPython] O_element070  label="O_element : 035"  # scripted group (container) (typed FeaturePython)
  n = 1
  ref = O_element
FEATURE [App::DocumentObjectGroupPython] G4_NITROUS_OXIDE  # scripted group (container) (typed FeaturePython)
  Dunit = g/cm3
  Dvalue = 0.00183094
  Group = -> [N_element030,O_element070]
  conduct = 2
  density = 1
  expand = 3
  formula = G4_NITROUS_OXIDE
  name = G4_NITROUS_OXIDE
  specific = 4
FEATURE [App::DocumentObjectGroupPython] H_element063  label="H_element : 0.104"  # scripted group (container) (typed FeaturePython)
  n = 0.103509
FEATURE [App::DocumentObjectGroupPython] C_element069  label="C_element : 0.648"  # scripted group (container) (typed FeaturePython)
  n = 0.648416
FEATURE [App::DocumentObjectGroupPython] N_element031  label="N_element : 0.100"  # scripted group (container) (typed FeaturePython)
  n = 0.0995361
FEATURE [App::DocumentObjectGroupPython] O_element071  label="O_element : 0.149"  # scripted group (container) (typed FeaturePython)
  n = 0.148539
FEATURE [App::DocumentObjectGroupPython] G4_NYLON_8062  label="G4_NYLON-8062"  # scripted group (container) (typed FeaturePython)
  Dunit = g/cm3
  Dvalue = 1.08
  Group = -> [H_element063,C_element069,N_element031,O_element071]
  conduct = 2
  density = 1
  expand = 3
  formula = G4_NYLON-8062
  name = G4_NYLON-8062
  specific = 4
FEATURE [App::DocumentObjectGroupPython] C_element070  label="C_element : 035"  # scripted group (container) (typed FeaturePython)
  n = 6
  ref = C_element
FEATURE [App::DocumentObjectGroupPython] H_element064  label="H_element : 11"  # scripted group (container) (typed FeaturePython)
  n = 11
  ref = H_element
FEATURE [App::DocumentObjectGroupPython] N_element032  label="N_element : 014"  # scripted group (container) (typed FeaturePython)
  n = 1
  ref = N_element
FEATURE [App::DocumentObjectGroupPython] O_element072  label="O_element : 036"  # scripted group (container) (typed FeaturePython)
  n = 1
  ref = O_element
FEATURE [App::DocumentObjectGroupPython] G4_NYLON_6_6  label="G4_NYLON-6-6"  # scripted group (container) (typed FeaturePython)
  Dunit = g/cm3
  Dvalue = 1.14
  Group = -> [C_element070,H_element064,N_element032,O_element072]
  conduct = 2
  density = 1
  expand = 3
  formula = G4_NYLON-6-6
  name = G4_NYLON-6-6
  specific = 4
FEATURE [App::DocumentObjectGroupPython] H_element065  label="H_element : 0.139"  # scripted group (container) (typed FeaturePython)
  n = 0.107062
FEATURE [App::DocumentObjectGroupPython] C_element071  label="C_element : 0.680"  # scripted group (container) (typed FeaturePython)
  n = 0.680449
FEATURE [App::DocumentObjectGroupPython] N_element033  label="N_element : 0.099"  # scripted group (container) (typed FeaturePython)
  n = 0.099189
FEATURE [App::DocumentObjectGroupPython] O_element073  label="O_element : 0.113"  # scripted group (container) (typed FeaturePython)
  n = 0.1133
FEATURE [App::DocumentObjectGroupPython] G4_NYLON_6_10  label="G4_NYLON-6-10"  # scripted group (container) (typed FeaturePython)
  Dunit = g/cm3
  Dvalue = 1.14
  Group = -> [H_element065,C_element071,N_element033,O_element073]
  conduct = 2
  density = 1
  expand = 3
  formula = G4_NYLON-6-10
  name = G4_NYLON-6-10
  specific = 4
FEATURE [App::DocumentObjectGroupPython] H_element066  label="H_element : 0.140"  # scripted group (container) (typed FeaturePython)
  n = 0.115476
FEATURE [App::DocumentObjectGroupPython] C_element072  label="C_element : 0.721"  # scripted group (container) (typed FeaturePython)
  n = 0.720818
FEATURE [App::DocumentObjectGroupPython] N_element034  label="N_element : 0.076"  # scripted group (container) (typed FeaturePython)
  n = 0.0764169
FEATURE [App::DocumentObjectGroupPython] O_element074  label="O_element : 0.087"  # scripted group (container) (typed FeaturePython)
  n = 0.0872889
FEATURE [App::DocumentObjectGroupPython] G4_NYLON_11_RILSAN  label="G4_NYLON-11_RILSAN"  # scripted group (container) (typed FeaturePython)
  Dunit = g/cm3
  Dvalue = 1.425
  Group = -> [H_element066,C_element072,N_element034,O_element074]
  conduct = 2
  density = 1
  expand = 3
  formula = G4_NYLON-11_RILSAN
  name = G4_NYLON-11_RILSAN
  specific = 4
FEATURE [App::DocumentObjectGroupPython] C_element073  label="C_element : 8"  # scripted group (container) (typed FeaturePython)
  n = 8
  ref = C_element
FEATURE [App::DocumentObjectGroupPython] H_element067  label="H_element : 18"  # scripted group (container) (typed FeaturePython)
  n = 18
  ref = H_element
FEATURE [App::DocumentObjectGroupPython] G4_OCTANE  # scripted group (container) (typed FeaturePython)
  Dunit = g/cm3
  Dvalue = 0.7026
  Group = -> [C_element073,H_element067]
  conduct = 2
  density = 1
  expand = 3
  formula = G4_OCTANE
  name = G4_OCTANE
  specific = 4
FEATURE [App::DocumentObjectGroupPython] C_element074  label="C_element : 25"  # scripted group (container) (typed FeaturePython)
  n = 25
  ref = C_element
FEATURE [App::DocumentObjectGroupPython] H_element068  label="H_element : 52"  # scripted group (container) (typed FeaturePython)
  n = 52
  ref = H_element
FEATURE [App::DocumentObjectGroupPython] G4_PARAFFIN  # scripted group (container) (typed FeaturePython)
  Dunit = g/cm3
  Dvalue = 0.93
  Group = -> [C_element074,H_element068]
  conduct = 2
  density = 1
  expand = 3
  formula = G4_PARAFFIN
  name = G4_PARAFFIN
  specific = 4
FEATURE [App::DocumentObjectGroupPython] C_element075  label="C_element : 036"  # scripted group (container) (typed FeaturePython)
  n = 5
  ref = C_element
FEATURE [App::DocumentObjectGroupPython] H_element069  label="H_element : 032"  # scripted group (container) (typed FeaturePython)
  n = 12
  ref = H_element
FEATURE [App::DocumentObjectGroupPython] G4_N_PENTANE  label="G4_N-PENTANE"  # scripted group (container) (typed FeaturePython)
  Dunit = g/cm3
  Dvalue = 0.6262
  Group = -> [C_element075,H_element069]
  conduct = 2
  density = 1
  expand = 3
  formula = G4_N-PENTANE
  name = G4_N-PENTANE
  specific = 4
FEATURE [App::DocumentObjectGroupPython] H_element070  label="H_element : 0.014"  # scripted group (container) (typed FeaturePython)
  n = 0.0141
FEATURE [App::DocumentObjectGroupPython] C_element076  label="C_element : 0.072"  # scripted group (container) (typed FeaturePython)
  n = 0.072261
FEATURE [App::DocumentObjectGroupPython] N_element035  label="N_element : 0.019"  # scripted group (container) (typed FeaturePython)
  n = 0.01932
FEATURE [App::DocumentObjectGroupPython] O_element075  label="O_element : 0.066"  # scripted group (container) (typed FeaturePython)
  n = 0.066101
FEATURE [App::DocumentObjectGroupPython] S_element019  label="S_element : 0.020"  # scripted group (container) (typed FeaturePython)
  n = 0.00189
FEATURE [App::DocumentObjectGroupPython] Br_element004  label="Br_element : 0.349"  # scripted group (container) (typed FeaturePython)
  n = 0.349103
FEATURE [App::DocumentObjectGroupPython] Ag_element001  label="Ag_element : 0.474"  # scripted group (container) (typed FeaturePython)
  n = 0.474105
FEATURE [App::DocumentObjectGroupPython] I_element005  label="I_element : 0.003"  # scripted group (container) (typed FeaturePython)
  n = 0.00312
FEATURE [App::DocumentObjectGroupPython] G4_PHOTO_EMULSION  # scripted group (container) (typed FeaturePython)
  Dunit = g/cm3
  Dvalue = 3.815
  Group = -> [H_element070,C_element076,N_element035,O_element075,S_element019,Br_element004,Ag_element001,I_element005]
  conduct = 2
  density = 1
  expand = 3
  formula = G4_PHOTO_EMULSION
  name = G4_PHOTO_EMULSION
  specific = 4
FEATURE [App::DocumentObjectGroupPython] C_element077  label="C_element : 9"  # scripted group (container) (typed FeaturePython)
  n = 9
  ref = C_element
FEATURE [App::DocumentObjectGroupPython] H_element071  label="H_element : 033"  # scripted group (container) (typed FeaturePython)
  n = 10
  ref = H_element
FEATURE [App::DocumentObjectGroupPython] G4_PLASTIC_SC_VINYLTOLUENE  # scripted group (container) (typed FeaturePython)
  Dunit = g/cm3
  Dvalue = 1.032
  Group = -> [C_element077,H_element071]
  conduct = 2
  density = 1
  expand = 3
  formula = G4_PLASTIC_SC_VINYLTOLUENE
  name = G4_PLASTIC_SC_VINYLTOLUENE
  specific = 4
FEATURE [App::DocumentObjectGroupPython] Pu_element001  label="Pu_element : 1"  # scripted group (container) (typed FeaturePython)
  n = 1
  ref = Pu_element
FEATURE [App::DocumentObjectGroupPython] O_element076  label="O_element : 037"  # scripted group (container) (typed FeaturePython)
  n = 2
  ref = O_element
FEATURE [App::DocumentObjectGroupPython] G4_PLUTONIUM_DIOXIDE  # scripted group (container) (typed FeaturePython)
  Dunit = g/cm3
  Dvalue = 11.46
  Group = -> [Pu_element001,O_element076]
  conduct = 2
  density = 1
  expand = 3
  formula = G4_PLUTONIUM_DIOXIDE
  name = G4_PLUTONIUM_DIOXIDE
  specific = 4
FEATURE [App::DocumentObjectGroupPython] C_element078  label="C_element : 037"  # scripted group (container) (typed FeaturePython)
  n = 3
  ref = C_element
FEATURE [App::DocumentObjectGroupPython] H_element072  label="H_element : 034"  # scripted group (container) (typed FeaturePython)
  n = 3
  ref = H_element
FEATURE [App::DocumentObjectGroupPython] N_element036  label="N_element : 015"  # scripted group (container) (typed FeaturePython)
  n = 1
  ref = N_element
FEATURE [App::DocumentObjectGroupPython] G4_POLYACRYLONITRILE  # scripted group (container) (typed FeaturePython)
  Dunit = g/cm3
  Dvalue = 1.17
  Group = -> [C_element078,H_element072,N_element036]
  conduct = 2
  density = 1
  expand = 3
  formula = G4_POLYACRYLONITRILE
  name = G4_POLYACRYLONITRILE
  specific = 4
FEATURE [App::DocumentObjectGroupPython] C_element079  label="C_element : 16"  # scripted group (container) (typed FeaturePython)
  n = 16
  ref = C_element
FEATURE [App::DocumentObjectGroupPython] H_element073  label="H_element : 035"  # scripted group (container) (typed FeaturePython)
  n = 14
  ref = H_element
FEATURE [App::DocumentObjectGroupPython] O_element077  label="O_element : 038"  # scripted group (container) (typed FeaturePython)
  n = 3
  ref = O_element
FEATURE [App::DocumentObjectGroupPython] G4_POLYCARBONATE  # scripted group (container) (typed FeaturePython)
  Dunit = g/cm3
  Dvalue = 1.2
  Group = -> [C_element079,H_element073,O_element077]
  conduct = 2
  density = 1
  expand = 3
  formula = G4_POLYCARBONATE
  name = G4_POLYCARBONATE
  specific = 4
FEATURE [App::DocumentObjectGroupPython] C_element080  label="C_element : 038"  # scripted group (container) (typed FeaturePython)
  n = 8
  ref = C_element
FEATURE [App::DocumentObjectGroupPython] H_element074  label="H_element : 036"  # scripted group (container) (typed FeaturePython)
  n = 7
  ref = H_element
FEATURE [App::DocumentObjectGroupPython] Cl_element017  label="Cl_element : 007"  # scripted group (container) (typed FeaturePython)
  n = 1
  ref = Cl_element
FEATURE [App::DocumentObjectGroupPython] G4_POLYCHLOROSTYRENE  # scripted group (container) (typed FeaturePython)
  Dunit = g/cm3
  Dvalue = 1.3
  Group = -> [C_element080,H_element074,Cl_element017]
  conduct = 2
  density = 1
  expand = 3
  formula = G4_POLYCHLOROSTYRENE
  name = G4_POLYCHLOROSTYRENE
  specific = 4
FEATURE [App::DocumentObjectGroupPython] C_element081  label="C_element : 039"  # scripted group (container) (typed FeaturePython)
  n = 1
  ref = C_element
FEATURE [App::DocumentObjectGroupPython] H_element075  label="H_element : 037"  # scripted group (container) (typed FeaturePython)
  n = 2
  ref = H_element
FEATURE [App::DocumentObjectGroupPython] G4_POLYETHYLENE  # scripted group (container) (typed FeaturePython)
  Dunit = g/cm3
  Dvalue = 0.94
  Group = -> [C_element081,H_element075]
  conduct = 2
  density = 1
  expand = 3
  formula = G4_POLYETHYLENE
  name = G4_POLYETHYLENE
  specific = 4
FEATURE [App::DocumentObjectGroupPython] C_element082  label="C_element : 040"  # scripted group (container) (typed FeaturePython)
  n = 10
  ref = C_element
FEATURE [App::DocumentObjectGroupPython] H_element076  label="H_element : 038"  # scripted group (container) (typed FeaturePython)
  n = 8
  ref = H_element
FEATURE [App::DocumentObjectGroupPython] O_element078  label="O_element : 039"  # scripted group (container) (typed FeaturePython)
  n = 4
  ref = O_element
FEATURE [App::DocumentObjectGroupPython] G4_MYLAR  # scripted group (container) (typed FeaturePython)
  Dunit = g/cm3
  Dvalue = 1.4
  Group = -> [C_element082,H_element076,O_element078]
  conduct = 2
  density = 1
  expand = 3
  formula = G4_MYLAR
  name = G4_MYLAR
  specific = 4
FEATURE [App::DocumentObjectGroupPython] C_element083  label="C_element : 041"  # scripted group (container) (typed FeaturePython)
  n = 5
  ref = C_element
FEATURE [App::DocumentObjectGroupPython] H_element077  label="H_element : 039"  # scripted group (container) (typed FeaturePython)
  n = 8
  ref = H_element
FEATURE [App::DocumentObjectGroupPython] O_element079  label="O_element : 040"  # scripted group (container) (typed FeaturePython)
  n = 2
  ref = O_element
FEATURE [App::DocumentObjectGroupPython] G4_PLEXIGLASS  # scripted group (container) (typed FeaturePython)
  Dunit = g/cm3
  Dvalue = 1.19
  Group = -> [C_element083,H_element077,O_element079]
  conduct = 2
  density = 1
  expand = 3
  formula = G4_PLEXIGLASS
  name = G4_PLEXIGLASS
  specific = 4
FEATURE [App::DocumentObjectGroupPython] C_element084  label="C_element : 042"  # scripted group (container) (typed FeaturePython)
  n = 1
  ref = C_element
FEATURE [App::DocumentObjectGroupPython] H_element078  label="H_element : 040"  # scripted group (container) (typed FeaturePython)
  n = 2
  ref = H_element
FEATURE [App::DocumentObjectGroupPython] O_element080  label="O_element : 041"  # scripted group (container) (typed FeaturePython)
  n = 1
  ref = O_element
FEATURE [App::DocumentObjectGroupPython] G4_POLYOXYMETHYLENE  # scripted group (container) (typed FeaturePython)
  Dunit = g/cm3
  Dvalue = 1.425
  Group = -> [C_element084,H_element078,O_element080]
  conduct = 2
  density = 1
  expand = 3
  formula = G4_POLYOXYMETHYLENE
  name = G4_POLYOXYMETHYLENE
  specific = 4
FEATURE [App::DocumentObjectGroupPython] C_element085  label="C_element : 043"  # scripted group (container) (typed FeaturePython)
  n = 2
  ref = C_element
FEATURE [App::DocumentObjectGroupPython] H_element079  label="H_element : 041"  # scripted group (container) (typed FeaturePython)
  n = 4
  ref = H_element
FEATURE [App::DocumentObjectGroupPython] G4_POLYPROPYLENE  # scripted group (container) (typed FeaturePython)
  Dunit = g/cm3
  Dvalue = 0.9
  Group = -> [C_element085,H_element079]
  conduct = 2
  density = 1
  expand = 3
  formula = G4_POLYPROPYLENE
  name = G4_POLYPROPYLENE
  specific = 4
FEATURE [App::DocumentObjectGroupPython] C_element086  label="C_element : 044"  # scripted group (container) (typed FeaturePython)
  n = 8
  ref = C_element
FEATURE [App::DocumentObjectGroupPython] H_element080  label="H_element : 042"  # scripted group (container) (typed FeaturePython)
  n = 8
  ref = H_element
FEATURE [App::DocumentObjectGroupPython] G4_POLYSTYRENE  # scripted group (container) (typed FeaturePython)
  Dunit = g/cm3
  Dvalue = 1.06
  Group = -> [C_element086,H_element080]
  conduct = 2
  density = 1
  expand = 3
  formula = G4_POLYSTYRENE
  name = G4_POLYSTYRENE
  specific = 4
FEATURE [App::DocumentObjectGroupPython] C_element087  label="C_element : 045"  # scripted group (container) (typed FeaturePython)
  n = 2
  ref = C_element
FEATURE [App::DocumentObjectGroupPython] F_element014  label="F_element : 4"  # scripted group (container) (typed FeaturePython)
  n = 4
  ref = F_element
FEATURE [App::DocumentObjectGroupPython] G4_TEFLON  # scripted group (container) (typed FeaturePython)
  Dunit = g/cm3
  Dvalue = 2.2
  Group = -> [C_element087,F_element014]
  conduct = 2
  density = 1
  expand = 3
  formula = G4_TEFLON
  name = G4_TEFLON
  specific = 4
FEATURE [App::DocumentObjectGroupPython] C_element088  label="C_element : 046"  # scripted group (container) (typed FeaturePython)
  n = 2
  ref = C_element
FEATURE [App::DocumentObjectGroupPython] F_element015  label="F_element : 006"  # scripted group (container) (typed FeaturePython)
  n = 3
  ref = F_element
FEATURE [App::DocumentObjectGroupPython] Cl_element018  label="Cl_element : 008"  # scripted group (container) (typed FeaturePython)
  n = 1
  ref = Cl_element
FEATURE [App::DocumentObjectGroupPython] G4_POLYTRIFLUOROCHLOROETHYLENE  # scripted group (container) (typed FeaturePython)
  Dunit = g/cm3
  Dvalue = 2.1
  Group = -> [C_element088,F_element015,Cl_element018]
  conduct = 2
  density = 1
  expand = 3
  formula = G4_POLYTRIFLUOROCHLOROETHYLENE
  name = G4_POLYTRIFLUOROCHLOROETHYLENE
  specific = 4
FEATURE [App::DocumentObjectGroupPython] C_element089  label="C_element : 047"  # scripted group (container) (typed FeaturePython)
  n = 4
  ref = C_element
FEATURE [App::DocumentObjectGroupPython] H_element081  label="H_element : 043"  # scripted group (container) (typed FeaturePython)
  n = 6
  ref = H_element
FEATURE [App::DocumentObjectGroupPython] O_element081  label="O_element : 042"  # scripted group (container) (typed FeaturePython)
  n = 2
  ref = O_element
FEATURE [App::DocumentObjectGroupPython] G4_POLYVINYL_ACETATE  # scripted group (container) (typed FeaturePython)
  Dunit = g/cm3
  Dvalue = 1.19
  Group = -> [C_element089,H_element081,O_element081]
  conduct = 2
  density = 1
  expand = 3
  formula = G4_POLYVINYL_ACETATE
  name = G4_POLYVINYL_ACETATE
  specific = 4
FEATURE [App::DocumentObjectGroupPython] C_element090  label="C_element : 048"  # scripted group (container) (typed FeaturePython)
  n = 2
  ref = C_element
FEATURE [App::DocumentObjectGroupPython] H_element082  label="H_element : 044"  # scripted group (container) (typed FeaturePython)
  n = 4
  ref = H_element
FEATURE [App::DocumentObjectGroupPython] O_element082  label="O_element : 043"  # scripted group (container) (typed FeaturePython)
  n = 1
  ref = O_element
FEATURE [App::DocumentObjectGroupPython] G4_POLYVINYL_ALCOHOL  # scripted group (container) (typed FeaturePython)
  Dunit = g/cm3
  Dvalue = 1.3
  Group = -> [C_element090,H_element082,O_element082]
  conduct = 2
  density = 1
  expand = 3
  formula = G4_POLYVINYL_ALCOHOL
  name = G4_POLYVINYL_ALCOHOL
  specific = 4
FEATURE [App::DocumentObjectGroupPython] C_element091  label="C_element : 049"  # scripted group (container) (typed FeaturePython)
  n = 8
  ref = C_element
FEATURE [App::DocumentObjectGroupPython] H_element083  label="H_element : 045"  # scripted group (container) (typed FeaturePython)
  n = 14
  ref = H_element
FEATURE [App::DocumentObjectGroupPython] O_element083  label="O_element : 044"  # scripted group (container) (typed FeaturePython)
  n = 2
  ref = O_element
FEATURE [App::DocumentObjectGroupPython] G4_POLYVINYL_BUTYRAL  # scripted group (container) (typed FeaturePython)
  Dunit = g/cm3
  Dvalue = 1.12
  Group = -> [C_element091,H_element083,O_element083]
  conduct = 2
  density = 1
  expand = 3
  formula = G4_POLYVINYL_BUTYRAL
  name = G4_POLYVINYL_BUTYRAL
  specific = 4
FEATURE [App::DocumentObjectGroupPython] C_element092  label="C_element : 050"  # scripted group (container) (typed FeaturePython)
  n = 2
  ref = C_element
FEATURE [App::DocumentObjectGroupPython] H_element084  label="H_element : 046"  # scripted group (container) (typed FeaturePython)
  n = 3
  ref = H_element
FEATURE [App::DocumentObjectGroupPython] Cl_element019  label="Cl_element : 009"  # scripted group (container) (typed FeaturePython)
  n = 1
  ref = Cl_element
FEATURE [App::DocumentObjectGroupPython] G4_POLYVINYL_CHLORIDE  # scripted group (container) (typed FeaturePython)
  Dunit = g/cm3
  Dvalue = 1.3
  Group = -> [C_element092,H_element084,Cl_element019]
  conduct = 2
  density = 1
  expand = 3
  formula = G4_POLYVINYL_CHLORIDE
  name = G4_POLYVINYL_CHLORIDE
  specific = 4
FEATURE [App::DocumentObjectGroupPython] C_element093  label="C_element : 051"  # scripted group (container) (typed FeaturePython)
  n = 2
  ref = C_element
FEATURE [App::DocumentObjectGroupPython] H_element085  label="H_element : 047"  # scripted group (container) (typed FeaturePython)
  n = 2
  ref = H_element
FEATURE [App::DocumentObjectGroupPython] Cl_element020  label="Cl_element : 010"  # scripted group (container) (typed FeaturePython)
  n = 2
  ref = Cl_element
FEATURE [App::DocumentObjectGroupPython] G4_POLYVINYLIDENE_CHLORIDE  # scripted group (container) (typed FeaturePython)
  Dunit = g/cm3
  Dvalue = 1.7
  Group = -> [C_element093,H_element085,Cl_element020]
  conduct = 2
  density = 1
  expand = 3
  formula = G4_POLYVINYLIDENE_CHLORIDE
  name = G4_POLYVINYLIDENE_CHLORIDE
  specific = 4
FEATURE [App::DocumentObjectGroupPython] C_element094  label="C_element : 052"  # scripted group (container) (typed FeaturePython)
  n = 2
  ref = C_element
FEATURE [App::DocumentObjectGroupPython] H_element086  label="H_element : 048"  # scripted group (container) (typed FeaturePython)
  n = 2
  ref = H_element
FEATURE [App::DocumentObjectGroupPython] F_element016  label="F_element : 007"  # scripted group (container) (typed FeaturePython)
  n = 2
  ref = F_element
FEATURE [App::DocumentObjectGroupPython] G4_POLYVINYLIDENE_FLUORIDE  # scripted group (container) (typed FeaturePython)
  Dunit = g/cm3
  Dvalue = 1.76
  Group = -> [C_element094,H_element086,F_element016]
  conduct = 2
  density = 1
  expand = 3
  formula = G4_POLYVINYLIDENE_FLUORIDE
  name = G4_POLYVINYLIDENE_FLUORIDE
  specific = 4
FEATURE [App::DocumentObjectGroupPython] C_element095  label="C_element : 053"  # scripted group (container) (typed FeaturePython)
  n = 6
  ref = C_element
FEATURE [App::DocumentObjectGroupPython] H_element087  label="H_element : 9"  # scripted group (container) (typed FeaturePython)
  n = 9
  ref = H_element
FEATURE [App::DocumentObjectGroupPython] N_element037  label="N_element : 016"  # scripted group (container) (typed FeaturePython)
  n = 1
  ref = N_element
FEATURE [App::DocumentObjectGroupPython] O_element084  label="O_element : 045"  # scripted group (container) (typed FeaturePython)
  n = 1
  ref = O_element
FEATURE [App::DocumentObjectGroupPython] G4_POLYVINYL_PYRROLIDONE  # scripted group (container) (typed FeaturePython)
  Dunit = g/cm3
  Dvalue = 1.25
  Group = -> [C_element095,H_element087,N_element037,O_element084]
  conduct = 2
  density = 1
  expand = 3
  formula = G4_POLYVINYL_PYRROLIDONE
  name = G4_POLYVINYL_PYRROLIDONE
  specific = 4
FEATURE [App::DocumentObjectGroupPython] K_element008  label="K_element : 1"  # scripted group (container) (typed FeaturePython)
  n = 1
  ref = K_element
FEATURE [App::DocumentObjectGroupPython] I_element006  label="I_element : 003"  # scripted group (container) (typed FeaturePython)
  n = 1
  ref = I_element
FEATURE [App::DocumentObjectGroupPython] G4_POTASSIUM_IODIDE  # scripted group (container) (typed FeaturePython)
  Dunit = g/cm3
  Dvalue = 3.13
  Group = -> [K_element008,I_element006]
  conduct = 2
  density = 1
  expand = 3
  formula = G4_POTASSIUM_IODIDE
  name = G4_POTASSIUM_IODIDE
  specific = 4
FEATURE [App::DocumentObjectGroupPython] K_element009  label="K_element : 2"  # scripted group (container) (typed FeaturePython)
  n = 2
  ref = K_element
FEATURE [App::DocumentObjectGroupPython] O_element085  label="O_element : 046"  # scripted group (container) (typed FeaturePython)
  n = 1
  ref = O_element
FEATURE [App::DocumentObjectGroupPython] G4_POTASSIUM_OXIDE  # scripted group (container) (typed FeaturePython)
  Dunit = g/cm3
  Dvalue = 2.32
  Group = -> [K_element009,O_element085]
  conduct = 2
  density = 1
  expand = 3
  formula = G4_POTASSIUM_OXIDE
  name = G4_POTASSIUM_OXIDE
  specific = 4
FEATURE [App::DocumentObjectGroupPython] C_element096  label="C_element : 054"  # scripted group (container) (typed FeaturePython)
  n = 3
  ref = C_element
FEATURE [App::DocumentObjectGroupPython] H_element088  label="H_element : 049"  # scripted group (container) (typed FeaturePython)
  n = 8
  ref = H_element
FEATURE [App::DocumentObjectGroupPython] G4_PROPANE  # scripted group (container) (typed FeaturePython)
  Dunit = g/cm3
  Dvalue = 0.00187939
  Group = -> [C_element096,H_element088]
  conduct = 2
  density = 1
  expand = 3
  formula = G4_PROPANE
  name = G4_PROPANE
  specific = 4
FEATURE [App::DocumentObjectGroupPython] C_element097  label="C_element : 055"  # scripted group (container) (typed FeaturePython)
  n = 3
  ref = C_element
FEATURE [App::DocumentObjectGroupPython] H_element089  label="H_element : 050"  # scripted group (container) (typed FeaturePython)
  n = 8
  ref = H_element
FEATURE [App::DocumentObjectGroupPython] G4_lPROPANE  # scripted group (container) (typed FeaturePython)
  Dunit = g/cm3
  Dvalue = 0.43
  Group = -> [C_element097,H_element089]
  conduct = 2
  density = 1
  expand = 3
  formula = G4_lPROPANE
  name = G4_lPROPANE
  specific = 4
FEATURE [App::DocumentObjectGroupPython] C_element098  label="C_element : 056"  # scripted group (container) (typed FeaturePython)
  n = 3
  ref = C_element
FEATURE [App::DocumentObjectGroupPython] H_element090  label="H_element : 051"  # scripted group (container) (typed FeaturePython)
  n = 8
  ref = H_element
FEATURE [App::DocumentObjectGroupPython] O_element086  label="O_element : 047"  # scripted group (container) (typed FeaturePython)
  n = 1
  ref = O_element
FEATURE [App::DocumentObjectGroupPython] G4_N_PROPYL_ALCOHOL  label="G4_N-PROPYL_ALCOHOL"  # scripted group (container) (typed FeaturePython)
  Dunit = g/cm3
  Dvalue = 0.8035
  Group = -> [C_element098,H_element090,O_element086]
  conduct = 2
  density = 1
  expand = 3
  formula = G4_N-PROPYL_ALCOHOL
  name = G4_N-PROPYL_ALCOHOL
  specific = 4
FEATURE [App::DocumentObjectGroupPython] C_element099  label="C_element : 057"  # scripted group (container) (typed FeaturePython)
  n = 5
  ref = C_element
FEATURE [App::DocumentObjectGroupPython] H_element091  label="H_element : 052"  # scripted group (container) (typed FeaturePython)
  n = 5
  ref = H_element
FEATURE [App::DocumentObjectGroupPython] N_element038  label="N_element : 017"  # scripted group (container) (typed FeaturePython)
  n = 1
  ref = N_element
FEATURE [App::DocumentObjectGroupPython] G4_PYRIDINE  # scripted group (container) (typed FeaturePython)
  Dunit = g/cm3
  Dvalue = 0.9819
  Group = -> [C_element099,H_element091,N_element038]
  conduct = 2
  density = 1
  expand = 3
  formula = G4_PYRIDINE
  name = G4_PYRIDINE
  specific = 4
FEATURE [App::DocumentObjectGroupPython] H_element092  label="H_element : 0.144"  # scripted group (container) (typed FeaturePython)
  n = 0.143711
FEATURE [App::DocumentObjectGroupPython] C_element100  label="C_element : 0.856"  # scripted group (container) (typed FeaturePython)
  n = 0.856289
FEATURE [App::DocumentObjectGroupPython] G4_RUBBER_BUTYL  # scripted group (container) (typed FeaturePython)
  Dunit = g/cm3
  Dvalue = 0.92
  Group = -> [H_element092,C_element100]
  conduct = 2
  density = 1
  expand = 3
  formula = G4_RUBBER_BUTYL
  name = G4_RUBBER_BUTYL
  specific = 4
FEATURE [App::DocumentObjectGroupPython] H_element093  label="H_element : 0.118"  # scripted group (container) (typed FeaturePython)
  n = 0.118371
FEATURE [App::DocumentObjectGroupPython] C_element101  label="C_element : 0.882"  # scripted group (container) (typed FeaturePython)
  n = 0.881629
FEATURE [App::DocumentObjectGroupPython] G4_RUBBER_NATURAL  # scripted group (container) (typed FeaturePython)
  Dunit = g/cm3
  Dvalue = 0.92
  Group = -> [H_element093,C_element101]
  conduct = 2
  density = 1
  expand = 3
  formula = G4_RUBBER_NATURAL
  name = G4_RUBBER_NATURAL
  specific = 4
FEATURE [App::DocumentObjectGroupPython] H_element094  label="H_element : 0.145"  # scripted group (container) (typed FeaturePython)
  n = 0.05692
FEATURE [App::DocumentObjectGroupPython] C_element102  label="C_element : 0.543"  # scripted group (container) (typed FeaturePython)
  n = 0.542646
FEATURE [App::DocumentObjectGroupPython] Cl_element021  label="Cl_element : 0.400"  # scripted group (container) (typed FeaturePython)
  n = 0.400434
FEATURE [App::DocumentObjectGroupPython] G4_RUBBER_NEOPRENE  # scripted group (container) (typed FeaturePython)
  Dunit = g/cm3
  Dvalue = 1.23
  Group = -> [H_element094,C_element102,Cl_element021]
  conduct = 2
  density = 1
  expand = 3
  formula = G4_RUBBER_NEOPRENE
  name = G4_RUBBER_NEOPRENE
  specific = 4
FEATURE [App::DocumentObjectGroupPython] Si_element006  label="Si_element : 1"  # scripted group (container) (typed FeaturePython)
  n = 1
  ref = Si_element
FEATURE [App::DocumentObjectGroupPython] O_element087  label="O_element : 048"  # scripted group (container) (typed FeaturePython)
  n = 2
  ref = O_element
FEATURE [App::DocumentObjectGroupPython] G4_SILICON_DIOXIDE  # scripted group (container) (typed FeaturePython)
  Dunit = g/cm3
  Dvalue = 2.32
  Group = -> [Si_element006,O_element087]
  conduct = 2
  density = 1
  expand = 3
  formula = G4_SILICON_DIOXIDE
  name = G4_SILICON_DIOXIDE
  specific = 4
FEATURE [App::DocumentObjectGroupPython] Ag_element002  label="Ag_element : 1"  # scripted group (container) (typed FeaturePython)
  n = 1
  ref = Ag_element
FEATURE [App::DocumentObjectGroupPython] Br_element005  label="Br_element : 003"  # scripted group (container) (typed FeaturePython)
  n = 1
  ref = Br_element
FEATURE [App::DocumentObjectGroupPython] G4_SILVER_BROMIDE  # scripted group (container) (typed FeaturePython)
  Dunit = g/cm3
  Dvalue = 6.473
  Group = -> [Ag_element002,Br_element005]
  conduct = 2
  density = 1
  expand = 3
  formula = G4_SILVER_BROMIDE
  name = G4_SILVER_BROMIDE
  specific = 4
FEATURE [App::DocumentObjectGroupPython] Ag_element003  label="Ag_element : 002"  # scripted group (container) (typed FeaturePython)
  n = 1
  ref = Ag_element
FEATURE [App::DocumentObjectGroupPython] Cl_element022  label="Cl_element : 011"  # scripted group (container) (typed FeaturePython)
  n = 1
  ref = Cl_element
FEATURE [App::DocumentObjectGroupPython] G4_SILVER_CHLORIDE  # scripted group (container) (typed FeaturePython)
  Dunit = g/cm3
  Dvalue = 5.56
  Group = -> [Ag_element003,Cl_element022]
  conduct = 2
  density = 1
  expand = 3
  formula = G4_SILVER_CHLORIDE
  name = G4_SILVER_CHLORIDE
  specific = 4
FEATURE [App::DocumentObjectGroupPython] Br_element006  label="Br_element : 0.423"  # scripted group (container) (typed FeaturePython)
  n = 0.422895
FEATURE [App::DocumentObjectGroupPython] Ag_element004  label="Ag_element : 0.574"  # scripted group (container) (typed FeaturePython)
  n = 0.573748
FEATURE [App::DocumentObjectGroupPython] I_element007  label="I_element : 0.649"  # scripted group (container) (typed FeaturePython)
  n = 0.003357
FEATURE [App::DocumentObjectGroupPython] G4_SILVER_HALIDES  # scripted group (container) (typed FeaturePython)
  Dunit = g/cm3
  Dvalue = 6.47
  Group = -> [Br_element006,Ag_element004,I_element007]
  conduct = 2
  density = 1
  expand = 3
  formula = G4_SILVER_HALIDES
  name = G4_SILVER_HALIDES
  specific = 4
FEATURE [App::DocumentObjectGroupPython] Ag_element005  label="Ag_element : 003"  # scripted group (container) (typed FeaturePython)
  n = 1
  ref = Ag_element
FEATURE [App::DocumentObjectGroupPython] I_element008  label="I_element : 004"  # scripted group (container) (typed FeaturePython)
  n = 1
  ref = I_element
FEATURE [App::DocumentObjectGroupPython] G4_SILVER_IODIDE  # scripted group (container) (typed FeaturePython)
  Dunit = g/cm3
  Dvalue = 6.01
  Group = -> [Ag_element005,I_element008]
  conduct = 2
  density = 1
  expand = 3
  formula = G4_SILVER_IODIDE
  name = G4_SILVER_IODIDE
  specific = 4
FEATURE [App::DocumentObjectGroupPython] H_element095  label="H_element : 0.100"  # scripted group (container) (typed FeaturePython)
  n = 0.1
FEATURE [App::DocumentObjectGroupPython] C_element103  label="C_element : 0.204"  # scripted group (container) (typed FeaturePython)
  n = 0.204
FEATURE [App::DocumentObjectGroupPython] N_element039  label="N_element : 0.759"  # scripted group (container) (typed FeaturePython)
  n = 0.042
FEATURE [App::DocumentObjectGroupPython] O_element088  label="O_element : 0.645"  # scripted group (container) (typed FeaturePython)
  n = 0.645
FEATURE [App::DocumentObjectGroupPython] Na_element013  label="Na_element : 0.100"  # scripted group (container) (typed FeaturePython)
  n = 0.002
FEATURE [App::DocumentObjectGroupPython] P_element009  label="P_element : 0.107"  # scripted group (container) (typed FeaturePython)
  n = 0.001
FEATURE [App::DocumentObjectGroupPython] S_element020  label="S_element : 0.021"  # scripted group (container) (typed FeaturePython)
  n = 0.002
FEATURE [App::DocumentObjectGroupPython] Cl_element023  label="Cl_element : 0.590"  # scripted group (container) (typed FeaturePython)
  n = 0.003
FEATURE [App::DocumentObjectGroupPython] K_element010  label="K_element : 0.001"  # scripted group (container) (typed FeaturePython)
  n = 0.001
FEATURE [App::DocumentObjectGroupPython] G4_SKIN_ICRP  # scripted group (container) (typed FeaturePython)
  Dunit = g/cm3
  Dvalue = 1.09
  Group = -> [H_element095,C_element103,N_element039,O_element088,Na_element013,P_element009,S_element020,Cl_element023,K_element010]
  conduct = 2
  density = 1
  expand = 3
  formula = G4_SKIN_ICRP
  name = G4_SKIN_ICRP
  specific = 4
FEATURE [App::DocumentObjectGroupPython] Na_element014  label="Na_element : 2"  # scripted group (container) (typed FeaturePython)
  n = 2
  ref = Na_element
FEATURE [App::DocumentObjectGroupPython] C_element104  label="C_element : 058"  # scripted group (container) (typed FeaturePython)
  n = 1
  ref = C_element
FEATURE [App::DocumentObjectGroupPython] O_element089  label="O_element : 049"  # scripted group (container) (typed FeaturePython)
  n = 3
  ref = O_element
FEATURE [App::DocumentObjectGroupPython] G4_SODIUM_CARBONATE  # scripted group (container) (typed FeaturePython)
  Dunit = g/cm3
  Dvalue = 2.532
  Group = -> [Na_element014,C_element104,O_element089]
  conduct = 2
  density = 1
  expand = 3
  formula = G4_SODIUM_CARBONATE
  name = G4_SODIUM_CARBONATE
  specific = 4
FEATURE [App::DocumentObjectGroupPython] Na_element015  label="Na_element : 1"  # scripted group (container) (typed FeaturePython)
  n = 1
  ref = Na_element
FEATURE [App::DocumentObjectGroupPython] I_element009  label="I_element : 005"  # scripted group (container) (typed FeaturePython)
  n = 1
  ref = I_element
FEATURE [App::DocumentObjectGroupPython] G4_SODIUM_IODIDE  # scripted group (container) (typed FeaturePython)
  Dunit = g/cm3
  Dvalue = 3.667
  Group = -> [Na_element015,I_element009]
  conduct = 2
  density = 1
  expand = 3
  formula = G4_SODIUM_IODIDE
  name = G4_SODIUM_IODIDE
  specific = 4
FEATURE [App::DocumentObjectGroupPython] Na_element016  label="Na_element : 003"  # scripted group (container) (typed FeaturePython)
  n = 2
  ref = Na_element
FEATURE [App::DocumentObjectGroupPython] O_element090  label="O_element : 050"  # scripted group (container) (typed FeaturePython)
  n = 1
  ref = O_element
FEATURE [App::DocumentObjectGroupPython] G4_SODIUM_MONOXIDE  # scripted group (container) (typed FeaturePython)
  Dunit = g/cm3
  Dvalue = 2.27
  Group = -> [Na_element016,O_element090]
  conduct = 2
  density = 1
  expand = 3
  formula = G4_SODIUM_MONOXIDE
  name = G4_SODIUM_MONOXIDE
  specific = 4
FEATURE [App::DocumentObjectGroupPython] Na_element017  label="Na_element : 004"  # scripted group (container) (typed FeaturePython)
  n = 1
  ref = Na_element
FEATURE [App::DocumentObjectGroupPython] N_element040  label="N_element : 018"  # scripted group (container) (typed FeaturePython)
  n = 1
  ref = N_element
FEATURE [App::DocumentObjectGroupPython] O_element091  label="O_element : 051"  # scripted group (container) (typed FeaturePython)
  n = 3
  ref = O_element
FEATURE [App::DocumentObjectGroupPython] G4_SODIUM_NITRATE  # scripted group (container) (typed FeaturePython)
  Dunit = g/cm3
  Dvalue = 2.261
  Group = -> [Na_element017,N_element040,O_element091]
  conduct = 2
  density = 1
  expand = 3
  formula = G4_SODIUM_NITRATE
  name = G4_SODIUM_NITRATE
  specific = 4
FEATURE [App::DocumentObjectGroupPython] C_element105  label="C_element : 059"  # scripted group (container) (typed FeaturePython)
  n = 14
  ref = C_element
FEATURE [App::DocumentObjectGroupPython] H_element096  label="H_element : 053"  # scripted group (container) (typed FeaturePython)
  n = 12
  ref = H_element
FEATURE [App::DocumentObjectGroupPython] G4_STILBENE  # scripted group (container) (typed FeaturePython)
  Dunit = g/cm3
  Dvalue = 0.9707
  Group = -> [C_element105,H_element096]
  conduct = 2
  density = 1
  expand = 3
  formula = G4_STILBENE
  name = G4_STILBENE
  specific = 4
FEATURE [App::DocumentObjectGroupPython] C_element106  label="C_element : 12"  # scripted group (container) (typed FeaturePython)
  n = 12
  ref = C_element
FEATURE [App::DocumentObjectGroupPython] H_element097  label="H_element : 22"  # scripted group (container) (typed FeaturePython)
  n = 22
  ref = H_element
FEATURE [App::DocumentObjectGroupPython] O_element092  label="O_element : 11"  # scripted group (container) (typed FeaturePython)
  n = 11
  ref = O_element
FEATURE [App::DocumentObjectGroupPython] G4_SUCROSE  # scripted group (container) (typed FeaturePython)
  Dunit = g/cm3
  Dvalue = 1.5805
  Group = -> [C_element106,H_element097,O_element092]
  conduct = 2
  density = 1
  expand = 3
  formula = G4_SUCROSE
  name = G4_SUCROSE
  specific = 4
FEATURE [App::DocumentObjectGroupPython] C_element107  label="C_element : 18"  # scripted group (container) (typed FeaturePython)
  n = 18
  ref = C_element
FEATURE [App::DocumentObjectGroupPython] H_element098  label="H_element : 054"  # scripted group (container) (typed FeaturePython)
  n = 14
  ref = H_element
FEATURE [App::DocumentObjectGroupPython] G4_TERPHENYL  # scripted group (container) (typed FeaturePython)
  Dunit = g/cm3
  Dvalue = 1.24
  Group = -> [C_element107,H_element098]
  conduct = 2
  density = 1
  expand = 3
  formula = G4_TERPHENYL
  name = G4_TERPHENYL
  specific = 4
FEATURE [App::DocumentObjectGroupPython] H_element099  label="H_element : 0.146"  # scripted group (container) (typed FeaturePython)
  n = 0.106
FEATURE [App::DocumentObjectGroupPython] C_element108  label="C_element : 0.883"  # scripted group (container) (typed FeaturePython)
  n = 0.099
FEATURE [App::DocumentObjectGroupPython] N_element041  label="N_element : 0.020"  # scripted group (container) (typed FeaturePython)
  n = 0.02
FEATURE [App::DocumentObjectGroupPython] O_element093  label="O_element : 0.766"  # scripted group (container) (typed FeaturePython)
  n = 0.766
FEATURE [App::DocumentObjectGroupPython] Na_element018  label="Na_element : 0.101"  # scripted group (container) (typed FeaturePython)
  n = 0.002
FEATURE [App::DocumentObjectGroupPython] P_element010  label="P_element : 0.108"  # scripted group (container) (typed FeaturePython)
  n = 0.001
FEATURE [App::DocumentObjectGroupPython] S_element021  label="S_element : 0.022"  # scripted group (container) (typed FeaturePython)
  n = 0.002
FEATURE [App::DocumentObjectGroupPython] Cl_element024  label="Cl_element : 0.002"  # scripted group (container) (typed FeaturePython)
  n = 0.002
FEATURE [App::DocumentObjectGroupPython] K_element011  label="K_element : 0.017"  # scripted group (container) (typed FeaturePython)
  n = 0.002
FEATURE [App::DocumentObjectGroupPython] G4_TESTIS_ICRP  # scripted group (container) (typed FeaturePython)
  Dunit = g/cm3
  Dvalue = 1.04
  Group = -> [H_element099,C_element108,N_element041,O_element093,Na_element018,P_element010,S_element021,Cl_element024,K_element011]
  conduct = 2
  density = 1
  expand = 3
  formula = G4_TESTIS_ICRP
  name = G4_TESTIS_ICRP
  specific = 4
FEATURE [App::DocumentObjectGroupPython] C_element109  label="C_element : 060"  # scripted group (container) (typed FeaturePython)
  n = 2
  ref = C_element
FEATURE [App::DocumentObjectGroupPython] Cl_element025  label="Cl_element : 012"  # scripted group (container) (typed FeaturePython)
  n = 4
  ref = Cl_element
FEATURE [App::DocumentObjectGroupPython] G4_TETRACHLOROETHYLENE  # scripted group (container) (typed FeaturePython)
  Dunit = g/cm3
  Dvalue = 1.625
  Group = -> [C_element109,Cl_element025]
  conduct = 2
  density = 1
  expand = 3
  formula = G4_TETRACHLOROETHYLENE
  name = G4_TETRACHLOROETHYLENE
  specific = 4
FEATURE [App::DocumentObjectGroupPython] Tl_element001  label="Tl_element : 1"  # scripted group (container) (typed FeaturePython)
  n = 1
  ref = Tl_element
FEATURE [App::DocumentObjectGroupPython] Cl_element026  label="Cl_element : 013"  # scripted group (container) (typed FeaturePython)
  n = 1
  ref = Cl_element
FEATURE [App::DocumentObjectGroupPython] G4_THALLIUM_CHLORIDE  # scripted group (container) (typed FeaturePython)
  Dunit = g/cm3
  Dvalue = 7.004
  Group = -> [Tl_element001,Cl_element026]
  conduct = 2
  density = 1
  expand = 3
  formula = G4_THALLIUM_CHLORIDE
  name = G4_THALLIUM_CHLORIDE
  specific = 4
FEATURE [App::DocumentObjectGroupPython] H_element100  label="H_element : 0.147"  # scripted group (container) (typed FeaturePython)
  n = 0.105
FEATURE [App::DocumentObjectGroupPython] C_element110  label="C_element : 0.256"  # scripted group (container) (typed FeaturePython)
  n = 0.256
FEATURE [App::DocumentObjectGroupPython] N_element042  label="N_element : 0.760"  # scripted group (container) (typed FeaturePython)
  n = 0.027
FEATURE [App::DocumentObjectGroupPython] O_element094  label="O_element : 0.602"  # scripted group (container) (typed FeaturePython)
  n = 0.602
FEATURE [App::DocumentObjectGroupPython] Na_element019  label="Na_element : 0.102"  # scripted group (container) (typed FeaturePython)
  n = 0.001
FEATURE [App::DocumentObjectGroupPython] P_element011  label="P_element : 0.109"  # scripted group (container) (typed FeaturePython)
  n = 0.002
FEATURE [App::DocumentObjectGroupPython] S_element022  label="S_element : 0.023"  # scripted group (container) (typed FeaturePython)
  n = 0.003
FEATURE [App::DocumentObjectGroupPython] Cl_element027  label="Cl_element : 0.591"  # scripted group (container) (typed FeaturePython)
  n = 0.002
FEATURE [App::DocumentObjectGroupPython] K_element012  label="K_element : 0.018"  # scripted group (container) (typed FeaturePython)
  n = 0.002
FEATURE [App::DocumentObjectGroupPython] G4_TISSUE_SOFT_ICRP  # scripted group (container) (typed FeaturePython)
  Dunit = g/cm3
  Dvalue = 1.03
  Group = -> [H_element100,C_element110,N_element042,O_element094,Na_element019,P_element011,S_element022,Cl_element027,K_element012]
  conduct = 2
  density = 1
  expand = 3
  formula = G4_TISSUE_SOFT_ICRP
  name = G4_TISSUE_SOFT_ICRP
  specific = 4
FEATURE [App::DocumentObjectGroupPython] H_element101  label="H_element : 0.148"  # scripted group (container) (typed FeaturePython)
  n = 0.101
FEATURE [App::DocumentObjectGroupPython] C_element111  label="C_element : 0.111"  # scripted group (container) (typed FeaturePython)
  n = 0.111
FEATURE [App::DocumentObjectGroupPython] N_element043  label="N_element : 0.026"  # scripted group (container) (typed FeaturePython)
  n = 0.026
FEATURE [App::DocumentObjectGroupPython] O_element095  label="O_element : 0.762"  # scripted group (container) (typed FeaturePython)
  n = 0.762
FEATURE [App::DocumentObjectGroupPython] G4_TISSUE_SOFT_ICRU_4  label="G4_TISSUE_SOFT_ICRU-4"  # scripted group (container) (typed FeaturePython)
  Dunit = g/cm3
  Dvalue = 1
  Group = -> [H_element101,C_element111,N_element043,O_element095]
  conduct = 2
  density = 1
  expand = 3
  formula = G4_TISSUE_SOFT_ICRU-4
  name = G4_TISSUE_SOFT_ICRU-4
  specific = 4
FEATURE [App::DocumentObjectGroupPython] H_element102  label="H_element : 0.149"  # scripted group (container) (typed FeaturePython)
  n = 0.101869
FEATURE [App::DocumentObjectGroupPython] C_element112  label="C_element : 0.456"  # scripted group (container) (typed FeaturePython)
  n = 0.456179
FEATURE [App::DocumentObjectGroupPython] N_element044  label="N_element : 0.761"  # scripted group (container) (typed FeaturePython)
  n = 0.035172
FEATURE [App::DocumentObjectGroupPython] O_element096  label="O_element : 0.407"  # scripted group (container) (typed FeaturePython)
  n = 0.40678
FEATURE [App::DocumentObjectGroupPython] G4_TISSUE_METHANE  label="G4_TISSUE-METHANE"  # scripted group (container) (typed FeaturePython)
  Dunit = g/cm3
  Dvalue = 0.00106409
  Group = -> [H_element102,C_element112,N_element044,O_element096]
  conduct = 2
  density = 1
  expand = 3
  formula = G4_TISSUE-METHANE
  name = G4_TISSUE-METHANE
  specific = 4
FEATURE [App::DocumentObjectGroupPython] H_element103  label="H_element : 0.103"  # scripted group (container) (typed FeaturePython)
  n = 0.102672
FEATURE [App::DocumentObjectGroupPython] C_element113  label="C_element : 0.569"  # scripted group (container) (typed FeaturePython)
  n = 0.56894
FEATURE [App::DocumentObjectGroupPython] N_element045  label="N_element : 0.762"  # scripted group (container) (typed FeaturePython)
  n = 0.035022
FEATURE [App::DocumentObjectGroupPython] O_element097  label="O_element : 0.293"  # scripted group (container) (typed FeaturePython)
  n = 0.293366
FEATURE [App::DocumentObjectGroupPython] G4_TISSUE_PROPANE  label="G4_TISSUE-PROPANE"  # scripted group (container) (typed FeaturePython)
  Dunit = g/cm3
  Dvalue = 0.00182628
  Group = -> [H_element103,C_element113,N_element045,O_element097]
  conduct = 2
  density = 1
  expand = 3
  formula = G4_TISSUE-PROPANE
  name = G4_TISSUE-PROPANE
  specific = 4
FEATURE [App::DocumentObjectGroupPython] Ti_element003  label="Ti_element : 1"  # scripted group (container) (typed FeaturePython)
  n = 1
  ref = Ti_element
FEATURE [App::DocumentObjectGroupPython] O_element098  label="O_element : 052"  # scripted group (container) (typed FeaturePython)
  n = 2
  ref = O_element
FEATURE [App::DocumentObjectGroupPython] G4_TITANIUM_DIOXIDE  # scripted group (container) (typed FeaturePython)
  Dunit = g/cm3
  Dvalue = 4.26
  Group = -> [Ti_element003,O_element098]
  conduct = 2
  density = 1
  expand = 3
  formula = G4_TITANIUM_DIOXIDE
  name = G4_TITANIUM_DIOXIDE
  specific = 4
FEATURE [App::DocumentObjectGroupPython] C_element114  label="C_element : 061"  # scripted group (container) (typed FeaturePython)
  n = 7
  ref = C_element
FEATURE [App::DocumentObjectGroupPython] H_element104  label="H_element : 055"  # scripted group (container) (typed FeaturePython)
  n = 8
  ref = H_element
FEATURE [App::DocumentObjectGroupPython] G4_TOLUENE  # scripted group (container) (typed FeaturePython)
  Dunit = g/cm3
  Dvalue = 0.8669
  Group = -> [C_element114,H_element104]
  conduct = 2
  density = 1
  expand = 3
  formula = G4_TOLUENE
  name = G4_TOLUENE
  specific = 4
FEATURE [App::DocumentObjectGroupPython] C_element115  label="C_element : 062"  # scripted group (container) (typed FeaturePython)
  n = 2
  ref = C_element
FEATURE [App::DocumentObjectGroupPython] H_element105  label="H_element : 056"  # scripted group (container) (typed FeaturePython)
  n = 1
  ref = H_element
FEATURE [App::DocumentObjectGroupPython] Cl_element028  label="Cl_element : 014"  # scripted group (container) (typed FeaturePython)
  n = 3
  ref = Cl_element
FEATURE [App::DocumentObjectGroupPython] G4_TRICHLOROETHYLENE  # scripted group (container) (typed FeaturePython)
  Dunit = g/cm3
  Dvalue = 1.46
  Group = -> [C_element115,H_element105,Cl_element028]
  conduct = 2
  density = 1
  expand = 3
  formula = G4_TRICHLOROETHYLENE
  name = G4_TRICHLOROETHYLENE
  specific = 4
FEATURE [App::DocumentObjectGroupPython] C_element116  label="C_element : 063"  # scripted group (container) (typed FeaturePython)
  n = 6
  ref = C_element
FEATURE [App::DocumentObjectGroupPython] H_element106  label="H_element : 15"  # scripted group (container) (typed FeaturePython)
  n = 15
  ref = H_element
FEATURE [App::DocumentObjectGroupPython] O_element099  label="O_element : 053"  # scripted group (container) (typed FeaturePython)
  n = 4
  ref = O_element
FEATURE [App::DocumentObjectGroupPython] P_element012  label="P_element : 1"  # scripted group (container) (typed FeaturePython)
  n = 1
  ref = P_element
FEATURE [App::DocumentObjectGroupPython] G4_TRIETHYL_PHOSPHATE  # scripted group (container) (typed FeaturePython)
  Dunit = g/cm3
  Dvalue = 1.07
  Group = -> [C_element116,H_element106,O_element099,P_element012]
  conduct = 2
  density = 1
  expand = 3
  formula = G4_TRIETHYL_PHOSPHATE
  name = G4_TRIETHYL_PHOSPHATE
  specific = 4
FEATURE [App::DocumentObjectGroupPython] W_element003  label="W_element : 003"  # scripted group (container) (typed FeaturePython)
  n = 1
  ref = W_element
FEATURE [App::DocumentObjectGroupPython] F_element017  label="F_element : 6"  # scripted group (container) (typed FeaturePython)
  n = 6
  ref = F_element
FEATURE [App::DocumentObjectGroupPython] G4_TUNGSTEN_HEXAFLUORIDE  # scripted group (container) (typed FeaturePython)
  Dunit = g/cm3
  Dvalue = 2.4
  Group = -> [W_element003,F_element017]
  conduct = 2
  density = 1
  expand = 3
  formula = G4_TUNGSTEN_HEXAFLUORIDE
  name = G4_TUNGSTEN_HEXAFLUORIDE
  specific = 4
FEATURE [App::DocumentObjectGroupPython] U_element001  label="U_element : 1"  # scripted group (container) (typed FeaturePython)
  n = 1
  ref = U_element
FEATURE [App::DocumentObjectGroupPython] C_element117  label="C_element : 064"  # scripted group (container) (typed FeaturePython)
  n = 2
  ref = C_element
FEATURE [App::DocumentObjectGroupPython] G4_URANIUM_DICARBIDE  # scripted group (container) (typed FeaturePython)
  Dunit = g/cm3
  Dvalue = 11.28
  Group = -> [U_element001,C_element117]
  conduct = 2
  density = 1
  expand = 3
  formula = G4_URANIUM_DICARBIDE
  name = G4_URANIUM_DICARBIDE
  specific = 4
FEATURE [App::DocumentObjectGroupPython] U_element002  label="U_element : 002"  # scripted group (container) (typed FeaturePython)
  n = 1
  ref = U_element
FEATURE [App::DocumentObjectGroupPython] C_element118  label="C_element : 065"  # scripted group (container) (typed FeaturePython)
  n = 1
  ref = C_element
FEATURE [App::DocumentObjectGroupPython] G4_URANIUM_MONOCARBIDE  # scripted group (container) (typed FeaturePython)
  Dunit = g/cm3
  Dvalue = 13.63
  Group = -> [U_element002,C_element118]
  conduct = 2
  density = 1
  expand = 3
  formula = G4_URANIUM_MONOCARBIDE
  name = G4_URANIUM_MONOCARBIDE
  specific = 4
FEATURE [App::DocumentObjectGroupPython] U_element003  label="U_element : 003"  # scripted group (container) (typed FeaturePython)
  n = 1
  ref = U_element
FEATURE [App::DocumentObjectGroupPython] O_element100  label="O_element : 054"  # scripted group (container) (typed FeaturePython)
  n = 2
  ref = O_element
FEATURE [App::DocumentObjectGroupPython] G4_URANIUM_OXIDE  # scripted group (container) (typed FeaturePython)
  Dunit = g/cm3
  Dvalue = 10.96
  Group = -> [U_element003,O_element100]
  conduct = 2
  density = 1
  expand = 3
  formula = G4_URANIUM_OXIDE
  name = G4_URANIUM_OXIDE
  specific = 4
FEATURE [App::DocumentObjectGroupPython] C_element119  label="C_element : 066"  # scripted group (container) (typed FeaturePython)
  n = 1
  ref = C_element
FEATURE [App::DocumentObjectGroupPython] H_element107  label="H_element : 057"  # scripted group (container) (typed FeaturePython)
  n = 4
  ref = H_element
FEATURE [App::DocumentObjectGroupPython] N_element046  label="N_element : 019"  # scripted group (container) (typed FeaturePython)
  n = 2
  ref = N_element
FEATURE [App::DocumentObjectGroupPython] O_element101  label="O_element : 055"  # scripted group (container) (typed FeaturePython)
  n = 1
  ref = O_element
FEATURE [App::DocumentObjectGroupPython] G4_UREA  # scripted group (container) (typed FeaturePython)
  Dunit = g/cm3
  Dvalue = 1.323
  Group = -> [C_element119,H_element107,N_element046,O_element101]
  conduct = 2
  density = 1
  expand = 3
  formula = G4_UREA
  name = G4_UREA
  specific = 4
FEATURE [App::DocumentObjectGroupPython] C_element120  label="C_element : 067"  # scripted group (container) (typed FeaturePython)
  n = 5
  ref = C_element
FEATURE [App::DocumentObjectGroupPython] H_element108  label="H_element : 058"  # scripted group (container) (typed FeaturePython)
  n = 11
  ref = H_element
FEATURE [App::DocumentObjectGroupPython] N_element047  label="N_element : 020"  # scripted group (container) (typed FeaturePython)
  n = 1
  ref = N_element
FEATURE [App::DocumentObjectGroupPython] O_element102  label="O_element : 056"  # scripted group (container) (typed FeaturePython)
  n = 2
  ref = O_element
FEATURE [App::DocumentObjectGroupPython] G4_VALINE  # scripted group (container) (typed FeaturePython)
  Dunit = g/cm3
  Dvalue = 1.23
  Group = -> [C_element120,H_element108,N_element047,O_element102]
  conduct = 2
  density = 1
  expand = 3
  formula = G4_VALINE
  name = G4_VALINE
  specific = 4
FEATURE [App::DocumentObjectGroupPython] H_element109  label="H_element : 0.009"  # scripted group (container) (typed FeaturePython)
  n = 0.009417
FEATURE [App::DocumentObjectGroupPython] C_element121  label="C_element : 0.281"  # scripted group (container) (typed FeaturePython)
  n = 0.280555
FEATURE [App::DocumentObjectGroupPython] F_element018  label="F_element : 0.710"  # scripted group (container) (typed FeaturePython)
  n = 0.710028
FEATURE [App::DocumentObjectGroupPython] G4_VITON  # scripted group (container) (typed FeaturePython)
  Dunit = g/cm3
  Dvalue = 1.8
  Group = -> [H_element109,C_element121,F_element018]
  conduct = 2
  density = 1
  expand = 3
  formula = G4_VITON
  name = G4_VITON
  specific = 4
FEATURE [App::DocumentObjectGroupPython] H_element110  label="H_element : 059"  # scripted group (container) (typed FeaturePython)
  n = 2
  ref = H_element
FEATURE [App::DocumentObjectGroupPython] O_element103  label="O_element : 057"  # scripted group (container) (typed FeaturePython)
  n = 1
  ref = O_element
FEATURE [App::DocumentObjectGroupPython] G4_WATER  # scripted group (container) (typed FeaturePython)
  Dunit = g/cm3
  Dvalue = 1
  Group = -> [H_element110,O_element103]
  conduct = 2
  density = 1
  expand = 3
  formula = G4_WATER
  name = G4_WATER
  specific = 4
FEATURE [App::DocumentObjectGroupPython] H_element111  label="H_element : 060"  # scripted group (container) (typed FeaturePython)
  n = 2
  ref = H_element
FEATURE [App::DocumentObjectGroupPython] O_element104  label="O_element : 058"  # scripted group (container) (typed FeaturePython)
  n = 1
  ref = O_element
FEATURE [App::DocumentObjectGroupPython] G4_WATER_VAPOR  # scripted group (container) (typed FeaturePython)
  Dunit = g/cm3
  Dvalue = 0.000756182
  Group = -> [H_element111,O_element104]
  conduct = 2
  density = 1
  expand = 3
  formula = G4_WATER_VAPOR
  name = G4_WATER_VAPOR
  specific = 4
FEATURE [App::DocumentObjectGroupPython] C_element122  label="C_element : 068"  # scripted group (container) (typed FeaturePython)
  n = 8
  ref = C_element
FEATURE [App::DocumentObjectGroupPython] H_element112  label="H_element : 061"  # scripted group (container) (typed FeaturePython)
  n = 10
  ref = H_element
FEATURE [App::DocumentObjectGroupPython] G4_XYLENE  # scripted group (container) (typed FeaturePython)
  Dunit = g/cm3
  Dvalue = 0.87
  Group = -> [C_element122,H_element112]
  conduct = 2
  density = 1
  expand = 3
  formula = G4_XYLENE
  name = G4_XYLENE
  specific = 4
FEATURE [App::DocumentObjectGroupPython] C_element123  label="C_element : 069"  # scripted group (container) (typed FeaturePython)
  n = 1
  ref = C_element
FEATURE [App::DocumentObjectGroupPython] G4_GRAPHITE  # scripted group (container) (typed FeaturePython)
  Dunit = g/cm3
  Dvalue = 2.21
  Group = -> [C_element123]
  conduct = 2
  density = 1
  expand = 3
  formula = G4_GRAPHITE
  name = G4_GRAPHITE
  specific = 4
FEATURE [App::DocumentObjectGroupPython] NIST  # scripted group (container) (typed FeaturePython)
  Group = -> [G4_A_150_TISSUE,G4_ACETONE,G4_ACETYLENE,G4_ADENINE,G4_ADIPOSE_TISSUE_ICRP,G4_AIR,G4_ALANINE,G4_ALUMINUM_OXIDE,G4_AMBER,G4_AMMONIA,G4_ANILINE,G4_ANTHRACENE,G4_B_100_BONE,G4_BAKELITE,G4_BARIUM_FLUORIDE,G4_BARIUM_SULFATE,G4_BENZENE,G4_BERYLLIUM_OXIDE,G4_BGO,G4_BLOOD_ICRP,G4_BONE_COMPACT_ICRU,G4_BONE_CORTICAL_ICRP,G4_BORON_CARBIDE,G4_BORON_OXIDE,G4_BRAIN_ICRP,G4_BUTANE,G4_N_BUTYL_ALCOHOL,G4_C_552,+152 more]
FEATURE [App::DocumentObjectGroupPython] H_element113  label="H_element : 062"  # scripted group (container) (typed FeaturePython)
  n = 1
  ref = H_element
FEATURE [App::DocumentObjectGroupPython] G4_H  # scripted group (container) (typed FeaturePython)
  Dunit = g/cm3
  Dvalue = 8.3748e-05
  Group = -> [H_element113]
  conduct = 2
  density = 1
  expand = 3
  formula = H
  name = G4_H
  specific = 4
FEATURE [App::DocumentObjectGroupPython] He_element001  label="He_element : 1"  # scripted group (container) (typed FeaturePython)
  n = 1
  ref = He_element
FEATURE [App::DocumentObjectGroupPython] G4_He  # scripted group (container) (typed FeaturePython)
  Dunit = g/cm3
  Dvalue = 0.000166322
  Group = -> [He_element001]
  conduct = 2
  density = 1
  expand = 3
  formula = He
  name = G4_He
  specific = 4
FEATURE [App::DocumentObjectGroupPython] Li_element008  label="Li_element : 008"  # scripted group (container) (typed FeaturePython)
  n = 1
  ref = Li_element
FEATURE [App::DocumentObjectGroupPython] G4_Li  # scripted group (container) (typed FeaturePython)
  Dunit = g/cm3
  Dvalue = 0.534
  Group = -> [Li_element008]
  conduct = 2
  density = 1
  expand = 3
  formula = Li
  name = G4_Li
  specific = 4
FEATURE [App::DocumentObjectGroupPython] Be_element002  label="Be_element : 002"  # scripted group (container) (typed FeaturePython)
  n = 1
  ref = Be_element
FEATURE [App::DocumentObjectGroupPython] G4_Be  # scripted group (container) (typed FeaturePython)
  Dunit = g/cm3
  Dvalue = 1.848
  Group = -> [Be_element002]
  conduct = 2
  density = 1
  expand = 3
  formula = Be
  name = G4_Be
  specific = 4
FEATURE [App::DocumentObjectGroupPython] B_element007  label="B_element : 007"  # scripted group (container) (typed FeaturePython)
  n = 1
  ref = B_element
FEATURE [App::DocumentObjectGroupPython] G4_B  # scripted group (container) (typed FeaturePython)
  Dunit = g/cm3
  Dvalue = 2.37
  Group = -> [B_element007]
  conduct = 2
  density = 1
  expand = 3
  formula = B
  name = G4_B
  specific = 4
FEATURE [App::DocumentObjectGroupPython] C_element124  label="C_element : 070"  # scripted group (container) (typed FeaturePython)
  n = 1
  ref = C_element
FEATURE [App::DocumentObjectGroupPython] G4_C  # scripted group (container) (typed FeaturePython)
  Dunit = g/cm3
  Dvalue = 2
  Group = -> [C_element124]
  conduct = 2
  density = 1
  expand = 3
  formula = C
  name = G4_C
  specific = 4
FEATURE [App::DocumentObjectGroupPython] N_element048  label="N_element : 021"  # scripted group (container) (typed FeaturePython)
  n = 1
  ref = N_element
FEATURE [App::DocumentObjectGroupPython] G4_N  # scripted group (container) (typed FeaturePython)
  Dunit = g/cm3
  Dvalue = 0.0011652
  Group = -> [N_element048]
  conduct = 2
  density = 1
  expand = 3
  formula = N
  name = G4_N
  specific = 4
FEATURE [App::DocumentObjectGroupPython] O_element105  label="O_element : 059"  # scripted group (container) (typed FeaturePython)
  n = 1
  ref = O_element
FEATURE [App::DocumentObjectGroupPython] G4_O  # scripted group (container) (typed FeaturePython)
  Dunit = g/cm3
  Dvalue = 0.00133151
  Group = -> [O_element105]
  conduct = 2
  density = 1
  expand = 3
  formula = O
  name = G4_O
  specific = 4
FEATURE [App::DocumentObjectGroupPython] F_element019  label="F_element : 008"  # scripted group (container) (typed FeaturePython)
  n = 1
  ref = F_element
FEATURE [App::DocumentObjectGroupPython] G4_F  # scripted group (container) (typed FeaturePython)
  Dunit = g/cm3
  Dvalue = 0.00158029
  Group = -> [F_element019]
  conduct = 2
  density = 1
  expand = 3
  formula = F
  name = G4_F
  specific = 4
FEATURE [App::DocumentObjectGroupPython] Ne_element001  label="Ne_element : 1"  # scripted group (container) (typed FeaturePython)
  n = 1
  ref = Ne_element
FEATURE [App::DocumentObjectGroupPython] G4_Ne  # scripted group (container) (typed FeaturePython)
  Dunit = g/cm3
  Dvalue = 0.000838505
  Group = -> [Ne_element001]
  conduct = 2
  density = 1
  expand = 3
  formula = Ne
  name = G4_Ne
  specific = 4
FEATURE [App::DocumentObjectGroupPython] Na_element020  label="Na_element : 005"  # scripted group (container) (typed FeaturePython)
  n = 1
  ref = Na_element
FEATURE [App::DocumentObjectGroupPython] G4_Na  # scripted group (container) (typed FeaturePython)
  Dunit = g/cm3
  Dvalue = 0.971
  Group = -> [Na_element020]
  conduct = 2
  density = 1
  expand = 3
  formula = Na
  name = G4_Na
  specific = 4
FEATURE [App::DocumentObjectGroupPython] Mg_element011  label="Mg_element : 005"  # scripted group (container) (typed FeaturePython)
  n = 1
  ref = Mg_element
FEATURE [App::DocumentObjectGroupPython] G4_Mg  # scripted group (container) (typed FeaturePython)
  Dunit = g/cm3
  Dvalue = 1.74
  Group = -> [Mg_element011]
  conduct = 2
  density = 1
  expand = 3
  formula = Mg
  name = G4_Mg
  specific = 4
FEATURE [App::DocumentObjectGroupPython] Al_element004  label="Al_element : 1"  # scripted group (container) (typed FeaturePython)
  n = 1
  ref = Al_element
FEATURE [App::DocumentObjectGroupPython] G4_Al  # scripted group (container) (typed FeaturePython)
  Dunit = g/cm3
  Dvalue = 2.699
  Group = -> [Al_element004]
  conduct = 2
  density = 1
  expand = 3
  formula = Al
  name = G4_Al
  specific = 4
FEATURE [App::DocumentObjectGroupPython] Si_element007  label="Si_element : 002"  # scripted group (container) (typed FeaturePython)
  n = 1
  ref = Si_element
FEATURE [App::DocumentObjectGroupPython] G4_Si  # scripted group (container) (typed FeaturePython)
  Dunit = g/cm3
  Dvalue = 2.33
  Group = -> [Si_element007]
  conduct = 2
  density = 1
  expand = 3
  formula = Si
  name = G4_Si
  specific = 4
FEATURE [App::DocumentObjectGroupPython] P_element013  label="P_element : 002"  # scripted group (container) (typed FeaturePython)
  n = 1
  ref = P_element
FEATURE [App::DocumentObjectGroupPython] G4_P  # scripted group (container) (typed FeaturePython)
  Dunit = g/cm3
  Dvalue = 2.2
  Group = -> [P_element013]
  conduct = 2
  density = 1
  expand = 3
  formula = P
  name = G4_P
  specific = 4
FEATURE [App::DocumentObjectGroupPython] S_element023  label="S_element : 007"  # scripted group (container) (typed FeaturePython)
  n = 1
  ref = S_element
FEATURE [App::DocumentObjectGroupPython] G4_S  # scripted group (container) (typed FeaturePython)
  Dunit = g/cm3
  Dvalue = 2
  Group = -> [S_element023]
  conduct = 2
  density = 1
  expand = 3
  formula = S
  name = G4_S
  specific = 4
FEATURE [App::DocumentObjectGroupPython] Cl_element029  label="Cl_element : 015"  # scripted group (container) (typed FeaturePython)
  n = 1
  ref = Cl_element
FEATURE [App::DocumentObjectGroupPython] G4_Cl  # scripted group (container) (typed FeaturePython)
  Dunit = g/cm3
  Dvalue = 0.00299473
  Group = -> [Cl_element029]
  conduct = 2
  density = 1
  expand = 3
  formula = Cl
  name = G4_Cl
  specific = 4
FEATURE [App::DocumentObjectGroupPython] Ar_element002  label="Ar_element : 1"  # scripted group (container) (typed FeaturePython)
  n = 1
  ref = Ar_element
FEATURE [App::DocumentObjectGroupPython] G4_Ar  # scripted group (container) (typed FeaturePython)
  Dunit = g/cm3
  Dvalue = 0.00166201
  Group = -> [Ar_element002]
  conduct = 2
  density = 1
  expand = 3
  formula = Ar
  name = G4_Ar
  specific = 4
FEATURE [App::DocumentObjectGroupPython] K_element013  label="K_element : 003"  # scripted group (container) (typed FeaturePython)
  n = 1
  ref = K_element
FEATURE [App::DocumentObjectGroupPython] G4_K  # scripted group (container) (typed FeaturePython)
  Dunit = g/cm3
  Dvalue = 0.862
  Group = -> [K_element013]
  conduct = 2
  density = 1
  expand = 3
  formula = K
  name = G4_K
  specific = 4
FEATURE [App::DocumentObjectGroupPython] Ca_element014  label="Ca_element : 007"  # scripted group (container) (typed FeaturePython)
  n = 1
  ref = Ca_element
FEATURE [App::DocumentObjectGroupPython] G4_Ca  # scripted group (container) (typed FeaturePython)
  Dunit = g/cm3
  Dvalue = 1.55
  Group = -> [Ca_element014]
  conduct = 2
  density = 1
  expand = 3
  formula = Ca
  name = G4_Ca
  specific = 4
FEATURE [App::DocumentObjectGroupPython] Sc_element001  label="Sc_element : 1"  # scripted group (container) (typed FeaturePython)
  n = 1
  ref = Sc_element
FEATURE [App::DocumentObjectGroupPython] G4_Sc  # scripted group (container) (typed FeaturePython)
  Dunit = g/cm3
  Dvalue = 2.989
  Group = -> [Sc_element001]
  conduct = 2
  density = 1
  expand = 3
  formula = Sc
  name = G4_Sc
  specific = 4
FEATURE [App::DocumentObjectGroupPython] Ti_element004  label="Ti_element : 002"  # scripted group (container) (typed FeaturePython)
  n = 1
  ref = Ti_element
FEATURE [App::DocumentObjectGroupPython] G4_Ti  # scripted group (container) (typed FeaturePython)
  Dunit = g/cm3
  Dvalue = 4.54
  Group = -> [Ti_element004]
  conduct = 2
  density = 1
  expand = 3
  formula = Ti
  name = G4_Ti
  specific = 4
FEATURE [App::DocumentObjectGroupPython] V_element001  label="V_element : 1"  # scripted group (container) (typed FeaturePython)
  n = 1
  ref = V_element
FEATURE [App::DocumentObjectGroupPython] G4_V  # scripted group (container) (typed FeaturePython)
  Dunit = g/cm3
  Dvalue = 6.11
  Group = -> [V_element001]
  conduct = 2
  density = 1
  expand = 3
  formula = V
  name = G4_V
  specific = 4
FEATURE [App::DocumentObjectGroupPython] Cr_element001  label="Cr_element : 1"  # scripted group (container) (typed FeaturePython)
  n = 1
  ref = Cr_element
FEATURE [App::DocumentObjectGroupPython] G4_Cr  # scripted group (container) (typed FeaturePython)
  Dunit = g/cm3
  Dvalue = 7.18
  Group = -> [Cr_element001]
  conduct = 2
  density = 1
  expand = 3
  formula = Cr
  name = G4_Cr
  specific = 4
FEATURE [App::DocumentObjectGroupPython] Mn_element001  label="Mn_element : 1"  # scripted group (container) (typed FeaturePython)
  n = 1
  ref = Mn_element
FEATURE [App::DocumentObjectGroupPython] G4_Mn  # scripted group (container) (typed FeaturePython)
  Dunit = g/cm3
  Dvalue = 7.44
  Group = -> [Mn_element001]
  conduct = 2
  density = 1
  expand = 3
  formula = Mn
  name = G4_Mn
  specific = 4
FEATURE [App::DocumentObjectGroupPython] Fe_element007  label="Fe_element : 004"  # scripted group (container) (typed FeaturePython)
  n = 1
  ref = Fe_element
FEATURE [App::DocumentObjectGroupPython] G4_Fe  # scripted group (container) (typed FeaturePython)
  Dunit = g/cm3
  Dvalue = 7.874
  Group = -> [Fe_element007]
  conduct = 2
  density = 1
  expand = 3
  formula = Fe
  name = G4_Fe
  specific = 4
FEATURE [App::DocumentObjectGroupPython] Co_element001  label="Co_element : 1"  # scripted group (container) (typed FeaturePython)
  n = 1
  ref = Co_element
FEATURE [App::DocumentObjectGroupPython] G4_Co  # scripted group (container) (typed FeaturePython)
  Dunit = g/cm3
  Dvalue = 8.9
  Group = -> [Co_element001]
  conduct = 2
  density = 1
  expand = 3
  formula = Co
  name = G4_Co
  specific = 4
FEATURE [App::DocumentObjectGroupPython] Ni_element001  label="Ni_element : 1"  # scripted group (container) (typed FeaturePython)
  n = 1
  ref = Ni_element
FEATURE [App::DocumentObjectGroupPython] G4_Ni  # scripted group (container) (typed FeaturePython)
  Dunit = g/cm3
  Dvalue = 8.902
  Group = -> [Ni_element001]
  conduct = 2
  density = 1
  expand = 3
  formula = Ni
  name = G4_Ni
  specific = 4
FEATURE [App::DocumentObjectGroupPython] Cu_element001  label="Cu_element : 1"  # scripted group (container) (typed FeaturePython)
  n = 1
  ref = Cu_element
FEATURE [App::DocumentObjectGroupPython] G4_Cu  # scripted group (container) (typed FeaturePython)
  Dunit = g/cm3
  Dvalue = 8.96
  Group = -> [Cu_element001]
  conduct = 2
  density = 1
  expand = 3
  formula = Cu
  name = G4_Cu
  specific = 4
FEATURE [App::DocumentObjectGroupPython] Zn_element001  label="Zn_element : 1"  # scripted group (container) (typed FeaturePython)
  n = 1
  ref = Zn_element
FEATURE [App::DocumentObjectGroupPython] G4_Zn  # scripted group (container) (typed FeaturePython)
  Dunit = g/cm3
  Dvalue = 7.133
  Group = -> [Zn_element001]
  conduct = 2
  density = 1
  expand = 3
  formula = Zn
  name = G4_Zn
  specific = 4
FEATURE [App::DocumentObjectGroupPython] Ga_element002  label="Ga_element : 002"  # scripted group (container) (typed FeaturePython)
  n = 1
  ref = Ga_element
FEATURE [App::DocumentObjectGroupPython] G4_Ga  # scripted group (container) (typed FeaturePython)
  Dunit = g/cm3
  Dvalue = 5.904
  Group = -> [Ga_element002]
  conduct = 2
  density = 1
  expand = 3
  formula = Ga
  name = G4_Ga
  specific = 4
FEATURE [App::DocumentObjectGroupPython] Ge_element002  label="Ge_element : 1"  # scripted group (container) (typed FeaturePython)
  n = 1
  ref = Ge_element
FEATURE [App::DocumentObjectGroupPython] G4_Ge  # scripted group (container) (typed FeaturePython)
  Dunit = g/cm3
  Dvalue = 5.323
  Group = -> [Ge_element002]
  conduct = 2
  density = 1
  expand = 3
  formula = Ge
  name = G4_Ge
  specific = 4
FEATURE [App::DocumentObjectGroupPython] As_element003  label="As_element : 002"  # scripted group (container) (typed FeaturePython)
  n = 1
  ref = As_element
FEATURE [App::DocumentObjectGroupPython] G4_As  # scripted group (container) (typed FeaturePython)
  Dunit = g/cm3
  Dvalue = 5.73
  Group = -> [As_element003]
  conduct = 2
  density = 1
  expand = 3
  formula = As
  name = G4_As
  specific = 4
FEATURE [App::DocumentObjectGroupPython] Se_element001  label="Se_element : 1"  # scripted group (container) (typed FeaturePython)
  n = 1
  ref = Se_element
FEATURE [App::DocumentObjectGroupPython] G4_Se  # scripted group (container) (typed FeaturePython)
  Dunit = g/cm3
  Dvalue = 4.5
  Group = -> [Se_element001]
  conduct = 2
  density = 1
  expand = 3
  formula = Se
  name = G4_Se
  specific = 4
FEATURE [App::DocumentObjectGroupPython] Br_element007  label="Br_element : 004"  # scripted group (container) (typed FeaturePython)
  n = 1
  ref = Br_element
FEATURE [App::DocumentObjectGroupPython] G4_Br  # scripted group (container) (typed FeaturePython)
  Dunit = g/cm3
  Dvalue = 0.0070721
  Group = -> [Br_element007]
  conduct = 2
  density = 1
  expand = 3
  formula = Br
  name = G4_Br
  specific = 4
FEATURE [App::DocumentObjectGroupPython] Kr_element001  label="Kr_element : 1"  # scripted group (container) (typed FeaturePython)
  n = 1
  ref = Kr_element
FEATURE [App::DocumentObjectGroupPython] G4_Kr  # scripted group (container) (typed FeaturePython)
  Dunit = g/cm3
  Dvalue = 0.00347832
  Group = -> [Kr_element001]
  conduct = 2
  density = 1
  expand = 3
  formula = Kr
  name = G4_Kr
  specific = 4
FEATURE [App::DocumentObjectGroupPython] Rb_element001  label="Rb_element : 1"  # scripted group (container) (typed FeaturePython)
  n = 1
  ref = Rb_element
FEATURE [App::DocumentObjectGroupPython] G4_Rb  # scripted group (container) (typed FeaturePython)
  Dunit = g/cm3
  Dvalue = 1.532
  Group = -> [Rb_element001]
  conduct = 2
  density = 1
  expand = 3
  formula = Rb
  name = G4_Rb
  specific = 4
FEATURE [App::DocumentObjectGroupPython] Sr_element001  label="Sr_element : 1"  # scripted group (container) (typed FeaturePython)
  n = 1
  ref = Sr_element
FEATURE [App::DocumentObjectGroupPython] G4_Sr  # scripted group (container) (typed FeaturePython)
  Dunit = g/cm3
  Dvalue = 2.54
  Group = -> [Sr_element001]
  conduct = 2
  density = 1
  expand = 3
  formula = Sr
  name = G4_Sr
  specific = 4
FEATURE [App::DocumentObjectGroupPython] Y_element001  label="Y_element : 1"  # scripted group (container) (typed FeaturePython)
  n = 1
  ref = Y_element
FEATURE [App::DocumentObjectGroupPython] G4_Y  # scripted group (container) (typed FeaturePython)
  Dunit = g/cm3
  Dvalue = 4.469
  Group = -> [Y_element001]
  conduct = 2
  density = 1
  expand = 3
  formula = Y
  name = G4_Y
  specific = 4
FEATURE [App::DocumentObjectGroupPython] Zr_element001  label="Zr_element : 1"  # scripted group (container) (typed FeaturePython)
  n = 1
  ref = Zr_element
FEATURE [App::DocumentObjectGroupPython] G4_Zr  # scripted group (container) (typed FeaturePython)
  Dunit = g/cm3
  Dvalue = 6.506
  Group = -> [Zr_element001]
  conduct = 2
  density = 1
  expand = 3
  formula = Zr
  name = G4_Zr
  specific = 4
FEATURE [App::DocumentObjectGroupPython] Nb_element001  label="Nb_element : 1"  # scripted group (container) (typed FeaturePython)
  n = 1
  ref = Nb_element
FEATURE [App::DocumentObjectGroupPython] G4_Nb  # scripted group (container) (typed FeaturePython)
  Dunit = g/cm3
  Dvalue = 8.57
  Group = -> [Nb_element001]
  conduct = 2
  density = 1
  expand = 3
  formula = Nb
  name = G4_Nb
  specific = 4
FEATURE [App::DocumentObjectGroupPython] Mo_element001  label="Mo_element : 1"  # scripted group (container) (typed FeaturePython)
  n = 1
  ref = Mo_element
FEATURE [App::DocumentObjectGroupPython] G4_Mo  # scripted group (container) (typed FeaturePython)
  Dunit = g/cm3
  Dvalue = 10.22
  Group = -> [Mo_element001]
  conduct = 2
  density = 1
  expand = 3
  formula = Mo
  name = G4_Mo
  specific = 4
FEATURE [App::DocumentObjectGroupPython] Tc_element001  label="Tc_element : 1"  # scripted group (container) (typed FeaturePython)
  n = 1
  ref = Tc_element
FEATURE [App::DocumentObjectGroupPython] G4_Tc  # scripted group (container) (typed FeaturePython)
  Dunit = g/cm3
  Dvalue = 11.5
  Group = -> [Tc_element001]
  conduct = 2
  density = 1
  expand = 3
  formula = Tc
  name = G4_Tc
  specific = 4
FEATURE [App::DocumentObjectGroupPython] Ru_element001  label="Ru_element : 1"  # scripted group (container) (typed FeaturePython)
  n = 1
  ref = Ru_element
FEATURE [App::DocumentObjectGroupPython] G4_Ru  # scripted group (container) (typed FeaturePython)
  Dunit = g/cm3
  Dvalue = 12.41
  Group = -> [Ru_element001]
  conduct = 2
  density = 1
  expand = 3
  formula = Ru
  name = G4_Ru
  specific = 4
FEATURE [App::DocumentObjectGroupPython] Rh_element001  label="Rh_element : 1"  # scripted group (container) (typed FeaturePython)
  n = 1
  ref = Rh_element
FEATURE [App::DocumentObjectGroupPython] G4_Rh  # scripted group (container) (typed FeaturePython)
  Dunit = g/cm3
  Dvalue = 12.41
  Group = -> [Rh_element001]
  conduct = 2
  density = 1
  expand = 3
  formula = Rh
  name = G4_Rh
  specific = 4
FEATURE [App::DocumentObjectGroupPython] Pd_element001  label="Pd_element : 1"  # scripted group (container) (typed FeaturePython)
  n = 1
  ref = Pd_element
FEATURE [App::DocumentObjectGroupPython] G4_Pd  # scripted group (container) (typed FeaturePython)
  Dunit = g/cm3
  Dvalue = 12.02
  Group = -> [Pd_element001]
  conduct = 2
  density = 1
  expand = 3
  formula = Pd
  name = G4_Pd
  specific = 4
FEATURE [App::DocumentObjectGroupPython] Ag_element006  label="Ag_element : 004"  # scripted group (container) (typed FeaturePython)
  n = 1
  ref = Ag_element
FEATURE [App::DocumentObjectGroupPython] G4_Ag  # scripted group (container) (typed FeaturePython)
  Dunit = g/cm3
  Dvalue = 10.5
  Group = -> [Ag_element006]
  conduct = 2
  density = 1
  expand = 3
  formula = Ag
  name = G4_Ag
  specific = 4
FEATURE [App::DocumentObjectGroupPython] Cd_element003  label="Cd_element : 003"  # scripted group (container) (typed FeaturePython)
  n = 1
  ref = Cd_element
FEATURE [App::DocumentObjectGroupPython] G4_Cd  # scripted group (container) (typed FeaturePython)
  Dunit = g/cm3
  Dvalue = 8.65
  Group = -> [Cd_element003]
  conduct = 2
  density = 1
  expand = 3
  formula = Cd
  name = G4_Cd
  specific = 4
FEATURE [App::DocumentObjectGroupPython] In_element001  label="In_element : 1"  # scripted group (container) (typed FeaturePython)
  n = 1
  ref = In_element
FEATURE [App::DocumentObjectGroupPython] G4_In  # scripted group (container) (typed FeaturePython)
  Dunit = g/cm3
  Dvalue = 7.31
  Group = -> [In_element001]
  conduct = 2
  density = 1
  expand = 3
  formula = In
  name = G4_In
  specific = 4
FEATURE [App::DocumentObjectGroupPython] Sn_element001  label="Sn_element : 1"  # scripted group (container) (typed FeaturePython)
  n = 1
  ref = Sn_element
FEATURE [App::DocumentObjectGroupPython] G4_Sn  # scripted group (container) (typed FeaturePython)
  Dunit = g/cm3
  Dvalue = 7.31
  Group = -> [Sn_element001]
  conduct = 2
  density = 1
  expand = 3
  formula = Sn
  name = G4_Sn
  specific = 4
FEATURE [App::DocumentObjectGroupPython] Sb_element001  label="Sb_element : 1"  # scripted group (container) (typed FeaturePython)
  n = 1
  ref = Sb_element
FEATURE [App::DocumentObjectGroupPython] G4_Sb  # scripted group (container) (typed FeaturePython)
  Dunit = g/cm3
  Dvalue = 6.691
  Group = -> [Sb_element001]
  conduct = 2
  density = 1
  expand = 3
  formula = Sb
  name = G4_Sb
  specific = 4
FEATURE [App::DocumentObjectGroupPython] Te_element002  label="Te_element : 002"  # scripted group (container) (typed FeaturePython)
  n = 1
  ref = Te_element
FEATURE [App::DocumentObjectGroupPython] G4_Te  # scripted group (container) (typed FeaturePython)
  Dunit = g/cm3
  Dvalue = 6.24
  Group = -> [Te_element002]
  conduct = 2
  density = 1
  expand = 3
  formula = Te
  name = G4_Te
  specific = 4
FEATURE [App::DocumentObjectGroupPython] I_element010  label="I_element : 006"  # scripted group (container) (typed FeaturePython)
  n = 1
  ref = I_element
FEATURE [App::DocumentObjectGroupPython] G4_I  # scripted group (container) (typed FeaturePython)
  Dunit = g/cm3
  Dvalue = 4.93
  Group = -> [I_element010]
  conduct = 2
  density = 1
  expand = 3
  formula = I
  name = G4_I
  specific = 4
FEATURE [App::DocumentObjectGroupPython] Xe_element001  label="Xe_element : 1"  # scripted group (container) (typed FeaturePython)
  n = 1
  ref = Xe_element
FEATURE [App::DocumentObjectGroupPython] G4_Xe  # scripted group (container) (typed FeaturePython)
  Dunit = g/cm3
  Dvalue = 0.00548536
  Group = -> [Xe_element001]
  conduct = 2
  density = 1
  expand = 3
  formula = Xe
  name = G4_Xe
  specific = 4
FEATURE [App::DocumentObjectGroupPython] Cs_element003  label="Cs_element : 003"  # scripted group (container) (typed FeaturePython)
  n = 1
  ref = Cs_element
FEATURE [App::DocumentObjectGroupPython] G4_Cs  # scripted group (container) (typed FeaturePython)
  Dunit = g/cm3
  Dvalue = 1.873
  Group = -> [Cs_element003]
  conduct = 2
  density = 1
  expand = 3
  formula = Cs
  name = G4_Cs
  specific = 4
FEATURE [App::DocumentObjectGroupPython] Ba_element003  label="Ba_element : 003"  # scripted group (container) (typed FeaturePython)
  n = 1
  ref = Ba_element
FEATURE [App::DocumentObjectGroupPython] G4_Ba  # scripted group (container) (typed FeaturePython)
  Dunit = g/cm3
  Dvalue = 3.5
  Group = -> [Ba_element003]
  conduct = 2
  density = 1
  expand = 3
  formula = Ba
  name = G4_Ba
  specific = 4
FEATURE [App::DocumentObjectGroupPython] La_element003  label="La_element : 003"  # scripted group (container) (typed FeaturePython)
  n = 1
  ref = La_element
FEATURE [App::DocumentObjectGroupPython] G4_La  # scripted group (container) (typed FeaturePython)
  Dunit = g/cm3
  Dvalue = 6.154
  Group = -> [La_element003]
  conduct = 2
  density = 1
  expand = 3
  formula = La
  name = G4_La
  specific = 4
FEATURE [App::DocumentObjectGroupPython] Ce_element002  label="Ce_element : 1"  # scripted group (container) (typed FeaturePython)
  n = 1
  ref = Ce_element
FEATURE [App::DocumentObjectGroupPython] G4_Ce  # scripted group (container) (typed FeaturePython)
  Dunit = g/cm3
  Dvalue = 6.657
  Group = -> [Ce_element002]
  conduct = 2
  density = 1
  expand = 3
  formula = Ce
  name = G4_Ce
  specific = 4
FEATURE [App::DocumentObjectGroupPython] Pr_element001  label="Pr_element : 1"  # scripted group (container) (typed FeaturePython)
  n = 1
  ref = Pr_element
FEATURE [App::DocumentObjectGroupPython] G4_Pr  # scripted group (container) (typed FeaturePython)
  Dunit = g/cm3
  Dvalue = 6.71
  Group = -> [Pr_element001]
  conduct = 2
  density = 1
  expand = 3
  formula = Pr
  name = G4_Pr
  specific = 4
FEATURE [App::DocumentObjectGroupPython] Nd_element001  label="Nd_element : 1"  # scripted group (container) (typed FeaturePython)
  n = 1
  ref = Nd_element
FEATURE [App::DocumentObjectGroupPython] G4_Nd  # scripted group (container) (typed FeaturePython)
  Dunit = g/cm3
  Dvalue = 6.9
  Group = -> [Nd_element001]
  conduct = 2
  density = 1
  expand = 3
  formula = Nd
  name = G4_Nd
  specific = 4
FEATURE [App::DocumentObjectGroupPython] Pm_element001  label="Pm_element : 1"  # scripted group (container) (typed FeaturePython)
  n = 1
  ref = Pm_element
FEATURE [App::DocumentObjectGroupPython] G4_Pm  # scripted group (container) (typed FeaturePython)
  Dunit = g/cm3
  Dvalue = 7.22
  Group = -> [Pm_element001]
  conduct = 2
  density = 1
  expand = 3
  formula = Pm
  name = G4_Pm
  specific = 4
FEATURE [App::DocumentObjectGroupPython] Sm_element001  label="Sm_element : 1"  # scripted group (container) (typed FeaturePython)
  n = 1
  ref = Sm_element
FEATURE [App::DocumentObjectGroupPython] G4_Sm  # scripted group (container) (typed FeaturePython)
  Dunit = g/cm3
  Dvalue = 7.46
  Group = -> [Sm_element001]
  conduct = 2
  density = 1
  expand = 3
  formula = Sm
  name = G4_Sm
  specific = 4
FEATURE [App::DocumentObjectGroupPython] Eu_element001  label="Eu_element : 1"  # scripted group (container) (typed FeaturePython)
  n = 1
  ref = Eu_element
FEATURE [App::DocumentObjectGroupPython] G4_Eu  # scripted group (container) (typed FeaturePython)
  Dunit = g/cm3
  Dvalue = 5.243
  Group = -> [Eu_element001]
  conduct = 2
  density = 1
  expand = 3
  formula = Eu
  name = G4_Eu
  specific = 4
FEATURE [App::DocumentObjectGroupPython] Gd_element002  label="Gd_element : 1"  # scripted group (container) (typed FeaturePython)
  n = 1
  ref = Gd_element
FEATURE [App::DocumentObjectGroupPython] G4_Gd  # scripted group (container) (typed FeaturePython)
  Dunit = g/cm3
  Dvalue = 7.9004
  Group = -> [Gd_element002]
  conduct = 2
  density = 1
  expand = 3
  formula = Gd
  name = G4_Gd
  specific = 4
FEATURE [App::DocumentObjectGroupPython] Tb_element001  label="Tb_element : 1"  # scripted group (container) (typed FeaturePython)
  n = 1
  ref = Tb_element
FEATURE [App::DocumentObjectGroupPython] G4_Tb  # scripted group (container) (typed FeaturePython)
  Dunit = g/cm3
  Dvalue = 8.229
  Group = -> [Tb_element001]
  conduct = 2
  density = 1
  expand = 3
  formula = Tb
  name = G4_Tb
  specific = 4
FEATURE [App::DocumentObjectGroupPython] Dy_element001  label="Dy_element : 1"  # scripted group (container) (typed FeaturePython)
  n = 1
  ref = Dy_element
FEATURE [App::DocumentObjectGroupPython] G4_Dy  # scripted group (container) (typed FeaturePython)
  Dunit = g/cm3
  Dvalue = 8.55
  Group = -> [Dy_element001]
  conduct = 2
  density = 1
  expand = 3
  formula = Dy
  name = G4_Dy
  specific = 4
FEATURE [App::DocumentObjectGroupPython] Ho_element001  label="Ho_element : 1"  # scripted group (container) (typed FeaturePython)
  n = 1
  ref = Ho_element
FEATURE [App::DocumentObjectGroupPython] G4_Ho  # scripted group (container) (typed FeaturePython)
  Dunit = g/cm3
  Dvalue = 8.795
  Group = -> [Ho_element001]
  conduct = 2
  density = 1
  expand = 3
  formula = Ho
  name = G4_Ho
  specific = 4
FEATURE [App::DocumentObjectGroupPython] Er_element001  label="Er_element : 1"  # scripted group (container) (typed FeaturePython)
  n = 1
  ref = Er_element
FEATURE [App::DocumentObjectGroupPython] G4_Er  # scripted group (container) (typed FeaturePython)
  Dunit = g/cm3
  Dvalue = 9.066
  Group = -> [Er_element001]
  conduct = 2
  density = 1
  expand = 3
  formula = Er
  name = G4_Er
  specific = 4
FEATURE [App::DocumentObjectGroupPython] Tm_element001  label="Tm_element : 1"  # scripted group (container) (typed FeaturePython)
  n = 1
  ref = Tm_element
FEATURE [App::DocumentObjectGroupPython] G4_Tm  # scripted group (container) (typed FeaturePython)
  Dunit = g/cm3
  Dvalue = 9.321
  Group = -> [Tm_element001]
  conduct = 2
  density = 1
  expand = 3
  formula = Tm
  name = G4_Tm
  specific = 4
FEATURE [App::DocumentObjectGroupPython] Yb_element001  label="Yb_element : 1"  # scripted group (container) (typed FeaturePython)
  n = 1
  ref = Yb_element
FEATURE [App::DocumentObjectGroupPython] G4_Yb  # scripted group (container) (typed FeaturePython)
  Dunit = g/cm3
  Dvalue = 6.73
  Group = -> [Yb_element001]
  conduct = 2
  density = 1
  expand = 3
  formula = Yb
  name = G4_Yb
  specific = 4
FEATURE [App::DocumentObjectGroupPython] Lu_element001  label="Lu_element : 1"  # scripted group (container) (typed FeaturePython)
  n = 1
  ref = Lu_element
FEATURE [App::DocumentObjectGroupPython] G4_Lu  # scripted group (container) (typed FeaturePython)
  Dunit = g/cm3
  Dvalue = 9.84
  Group = -> [Lu_element001]
  conduct = 2
  density = 1
  expand = 3
  formula = Lu
  name = G4_Lu
  specific = 4
FEATURE [App::DocumentObjectGroupPython] Hf_element001  label="Hf_element : 1"  # scripted group (container) (typed FeaturePython)
  n = 1
  ref = Hf_element
FEATURE [App::DocumentObjectGroupPython] G4_Hf  # scripted group (container) (typed FeaturePython)
  Dunit = g/cm3
  Dvalue = 13.31
  Group = -> [Hf_element001]
  conduct = 2
  density = 1
  expand = 3
  formula = Hf
  name = G4_Hf
  specific = 4
FEATURE [App::DocumentObjectGroupPython] Ta_element001  label="Ta_element : 1"  # scripted group (container) (typed FeaturePython)
  n = 1
  ref = Ta_element
FEATURE [App::DocumentObjectGroupPython] G4_Ta  # scripted group (container) (typed FeaturePython)
  Dunit = g/cm3
  Dvalue = 16.654
  Group = -> [Ta_element001]
  conduct = 2
  density = 1
  expand = 3
  formula = Ta
  name = G4_Ta
  specific = 4
FEATURE [App::DocumentObjectGroupPython] W_element004  label="W_element : 004"  # scripted group (container) (typed FeaturePython)
  n = 1
  ref = W_element
FEATURE [App::DocumentObjectGroupPython] G4_W  # scripted group (container) (typed FeaturePython)
  Dunit = g/cm3
  Dvalue = 19.3
  Group = -> [W_element004]
  conduct = 2
  density = 1
  expand = 3
  formula = W
  name = G4_W
  specific = 4
FEATURE [App::DocumentObjectGroupPython] Re_element001  label="Re_element : 1"  # scripted group (container) (typed FeaturePython)
  n = 1
  ref = Re_element
FEATURE [App::DocumentObjectGroupPython] G4_Re  # scripted group (container) (typed FeaturePython)
  Dunit = g/cm3
  Dvalue = 21.02
  Group = -> [Re_element001]
  conduct = 2
  density = 1
  expand = 3
  formula = Re
  name = G4_Re
  specific = 4
FEATURE [App::DocumentObjectGroupPython] Os_element001  label="Os_element : 1"  # scripted group (container) (typed FeaturePython)
  n = 1
  ref = Os_element
FEATURE [App::DocumentObjectGroupPython] G4_Os  # scripted group (container) (typed FeaturePython)
  Dunit = g/cm3
  Dvalue = 22.57
  Group = -> [Os_element001]
  conduct = 2
  density = 1
  expand = 3
  formula = Os
  name = G4_Os
  specific = 4
FEATURE [App::DocumentObjectGroupPython] Ir_element001  label="Ir_element : 1"  # scripted group (container) (typed FeaturePython)
  n = 1
  ref = Ir_element
FEATURE [App::DocumentObjectGroupPython] G4_Ir  # scripted group (container) (typed FeaturePython)
  Dunit = g/cm3
  Dvalue = 22.42
  Group = -> [Ir_element001]
  conduct = 2
  density = 1
  expand = 3
  formula = Ir
  name = G4_Ir
  specific = 4
FEATURE [App::DocumentObjectGroupPython] Pt_element001  label="Pt_element : 1"  # scripted group (container) (typed FeaturePython)
  n = 1
  ref = Pt_element
FEATURE [App::DocumentObjectGroupPython] G4_Pt  # scripted group (container) (typed FeaturePython)
  Dunit = g/cm3
  Dvalue = 21.45
  Group = -> [Pt_element001]
  conduct = 2
  density = 1
  expand = 3
  formula = Pt
  name = G4_Pt
  specific = 4
FEATURE [App::DocumentObjectGroupPython] Au_element001  label="Au_element : 1"  # scripted group (container) (typed FeaturePython)
  n = 1
  ref = Au_element
FEATURE [App::DocumentObjectGroupPython] G4_Au  # scripted group (container) (typed FeaturePython)
  Dunit = g/cm3
  Dvalue = 19.32
  Group = -> [Au_element001]
  conduct = 2
  density = 1
  expand = 3
  formula = Au
  name = G4_Au
  specific = 4
FEATURE [App::DocumentObjectGroupPython] Hg_element002  label="Hg_element : 002"  # scripted group (container) (typed FeaturePython)
  n = 1
  ref = Hg_element
FEATURE [App::DocumentObjectGroupPython] G4_Hg  # scripted group (container) (typed FeaturePython)
  Dunit = g/cm3
  Dvalue = 13.546
  Group = -> [Hg_element002]
  conduct = 2
  density = 1
  expand = 3
  formula = Hg
  name = G4_Hg
  specific = 4
FEATURE [App::DocumentObjectGroupPython] Tl_element002  label="Tl_element : 002"  # scripted group (container) (typed FeaturePython)
  n = 1
  ref = Tl_element
FEATURE [App::DocumentObjectGroupPython] G4_Tl  # scripted group (container) (typed FeaturePython)
  Dunit = g/cm3
  Dvalue = 11.72
  Group = -> [Tl_element002]
  conduct = 2
  density = 1
  expand = 3
  formula = Tl
  name = G4_Tl
  specific = 4
FEATURE [App::DocumentObjectGroupPython] Pb_element003  label="Pb_element : 1"  # scripted group (container) (typed FeaturePython)
  n = 1
  ref = Pb_element
FEATURE [App::DocumentObjectGroupPython] G4_Pb  # scripted group (container) (typed FeaturePython)
  Dunit = g/cm3
  Dvalue = 11.35
  Group = -> [Pb_element003]
  conduct = 2
  density = 1
  expand = 3
  formula = Pb
  name = G4_Pb
  specific = 4
FEATURE [App::DocumentObjectGroupPython] Bi_element002  label="Bi_element : 1"  # scripted group (container) (typed FeaturePython)
  n = 1
  ref = Bi_element
FEATURE [App::DocumentObjectGroupPython] G4_Bi  # scripted group (container) (typed FeaturePython)
  Dunit = g/cm3
  Dvalue = 9.747
  Group = -> [Bi_element002]
  conduct = 2
  density = 1
  expand = 3
  formula = Bi
  name = G4_Bi
  specific = 4
FEATURE [App::DocumentObjectGroupPython] Po_element001  label="Po_element : 1"  # scripted group (container) (typed FeaturePython)
  n = 1
  ref = Po_element
FEATURE [App::DocumentObjectGroupPython] G4_Po  # scripted group (container) (typed FeaturePython)
  Dunit = g/cm3
  Dvalue = 9.32
  Group = -> [Po_element001]
  conduct = 2
  density = 1
  expand = 3
  formula = Po
  name = G4_Po
  specific = 4
FEATURE [App::DocumentObjectGroupPython] At_element001  label="At_element : 1"  # scripted group (container) (typed FeaturePython)
  n = 1
  ref = At_element
FEATURE [App::DocumentObjectGroupPython] G4_At  # scripted group (container) (typed FeaturePython)
  Dunit = g/cm3
  Dvalue = 9.32
  Group = -> [At_element001]
  conduct = 2
  density = 1
  expand = 3
  formula = At
  name = G4_At
  specific = 4
FEATURE [App::DocumentObjectGroupPython] Rn_element001  label="Rn_element : 1"  # scripted group (container) (typed FeaturePython)
  n = 1
  ref = Rn_element
FEATURE [App::DocumentObjectGroupPython] G4_Rn  # scripted group (container) (typed FeaturePython)
  Dunit = g/cm3
  Dvalue = 0.00900662
  Group = -> [Rn_element001]
  conduct = 2
  density = 1
  expand = 3
  formula = Rn
  name = G4_Rn
  specific = 4
FEATURE [App::DocumentObjectGroupPython] Fr_element001  label="Fr_element : 1"  # scripted group (container) (typed FeaturePython)
  n = 1
  ref = Fr_element
FEATURE [App::DocumentObjectGroupPython] G4_Fr  # scripted group (container) (typed FeaturePython)
  Dunit = g/cm3
  Dvalue = 1
  Group = -> [Fr_element001]
  conduct = 2
  density = 1
  expand = 3
  formula = Fr
  name = G4_Fr
  specific = 4
FEATURE [App::DocumentObjectGroupPython] Ra_element001  label="Ra_element : 1"  # scripted group (container) (typed FeaturePython)
  n = 1
  ref = Ra_element
FEATURE [App::DocumentObjectGroupPython] G4_Ra  # scripted group (container) (typed FeaturePython)
  Dunit = g/cm3
  Dvalue = 5
  Group = -> [Ra_element001]
  conduct = 2
  density = 1
  expand = 3
  formula = Ra
  name = G4_Ra
  specific = 4
FEATURE [App::DocumentObjectGroupPython] Ac_element001  label="Ac_element : 1"  # scripted group (container) (typed FeaturePython)
  n = 1
  ref = Ac_element
FEATURE [App::DocumentObjectGroupPython] G4_Ac  # scripted group (container) (typed FeaturePython)
  Dunit = g/cm3
  Dvalue = 10.07
  Group = -> [Ac_element001]
  conduct = 2
  density = 1
  expand = 3
  formula = Ac
  name = G4_Ac
  specific = 4
FEATURE [App::DocumentObjectGroupPython] Th_element001  label="Th_element : 1"  # scripted group (container) (typed FeaturePython)
  n = 1
  ref = Th_element
FEATURE [App::DocumentObjectGroupPython] G4_Th  # scripted group (container) (typed FeaturePython)
  Dunit = g/cm3
  Dvalue = 11.72
  Group = -> [Th_element001]
  conduct = 2
  density = 1
  expand = 3
  formula = Th
  name = G4_Th
  specific = 4
FEATURE [App::DocumentObjectGroupPython] Pa_element001  label="Pa_element : 1"  # scripted group (container) (typed FeaturePython)
  n = 1
  ref = Pa_element
FEATURE [App::DocumentObjectGroupPython] G4_Pa  # scripted group (container) (typed FeaturePython)
  Dunit = g/cm3
  Dvalue = 15.37
  Group = -> [Pa_element001]
  conduct = 2
  density = 1
  expand = 3
  formula = Pa
  name = G4_Pa
  specific = 4
FEATURE [App::DocumentObjectGroupPython] U_element004  label="U_element : 004"  # scripted group (container) (typed FeaturePython)
  n = 1
  ref = U_element
FEATURE [App::DocumentObjectGroupPython] G4_U  # scripted group (container) (typed FeaturePython)
  Dunit = g/cm3
  Dvalue = 18.95
  Group = -> [U_element004]
  conduct = 2
  density = 1
  expand = 3
  formula = U
  name = G4_U
  specific = 4
FEATURE [App::DocumentObjectGroupPython] Np_element001  label="Np_element : 1"  # scripted group (container) (typed FeaturePython)
  n = 1
  ref = Np_element
FEATURE [App::DocumentObjectGroupPython] G4_Np  # scripted group (container) (typed FeaturePython)
  Dunit = g/cm3
  Dvalue = 20.25
  Group = -> [Np_element001]
  conduct = 2
  density = 1
  expand = 3
  formula = Np
  name = G4_Np
  specific = 4
FEATURE [App::DocumentObjectGroupPython] Pu_element002  label="Pu_element : 002"  # scripted group (container) (typed FeaturePython)
  n = 1
  ref = Pu_element
FEATURE [App::DocumentObjectGroupPython] G4_Pu  # scripted group (container) (typed FeaturePython)
  Dunit = g/cm3
  Dvalue = 19.84
  Group = -> [Pu_element002]
  conduct = 2
  density = 1
  expand = 3
  formula = Pu
  name = G4_Pu
  specific = 4
FEATURE [App::DocumentObjectGroupPython] Am_element001  label="Am_element : 1"  # scripted group (container) (typed FeaturePython)
  n = 1
  ref = Am_element
FEATURE [App::DocumentObjectGroupPython] G4_Am  # scripted group (container) (typed FeaturePython)
  Dunit = g/cm3
  Dvalue = 13.67
  Group = -> [Am_element001]
  conduct = 2
  density = 1
  expand = 3
  formula = Am
  name = G4_Am
  specific = 4
FEATURE [App::DocumentObjectGroupPython] Cm_element001  label="Cm_element : 1"  # scripted group (container) (typed FeaturePython)
  n = 1
  ref = Cm_element
FEATURE [App::DocumentObjectGroupPython] G4_Cm  # scripted group (container) (typed FeaturePython)
  Dunit = g/cm3
  Dvalue = 13.51
  Group = -> [Cm_element001]
  conduct = 2
  density = 1
  expand = 3
  formula = Cm
  name = G4_Cm
  specific = 4
FEATURE [App::DocumentObjectGroupPython] Bk_element001  label="Bk_element : 1"  # scripted group (container) (typed FeaturePython)
  n = 1
  ref = Bk_element
FEATURE [App::DocumentObjectGroupPython] G4_Bk  # scripted group (container) (typed FeaturePython)
  Dunit = g/cm3
  Dvalue = 14
  Group = -> [Bk_element001]
  conduct = 2
  density = 1
  expand = 3
  formula = Bk
  name = G4_Bk
  specific = 4
FEATURE [App::DocumentObjectGroupPython] Cf_element001  label="Cf_element : 1"  # scripted group (container) (typed FeaturePython)
  n = 1
  ref = Cf_element
FEATURE [App::DocumentObjectGroupPython] G4_Cf  # scripted group (container) (typed FeaturePython)
  Dunit = g/cm3
  Dvalue = 10
  Group = -> [Cf_element001]
  conduct = 2
  density = 1
  expand = 3
  formula = Cf
  name = G4_Cf
  specific = 4
FEATURE [App::DocumentObjectGroupPython] Element  # scripted group (container) (typed FeaturePython)
  Group = -> [G4_H,G4_He,G4_Li,G4_Be,G4_B,G4_C,G4_N,G4_O,G4_F,G4_Ne,G4_Na,G4_Mg,G4_Al,G4_Si,G4_P,G4_S,G4_Cl,G4_Ar,G4_K,G4_Ca,G4_Sc,G4_Ti,G4_V,G4_Cr,G4_Mn,G4_Fe,G4_Co,G4_Ni,G4_Cu,G4_Zn,G4_Ga,G4_Ge,G4_As,G4_Se,G4_Br,G4_Kr,G4_Rb,G4_Sr,G4_Y,G4_Zr,G4_Nb,G4_Mo,G4_Tc,G4_Ru,G4_Rh,G4_Pd,G4_Ag,G4_Cd,G4_In,G4_Sn,G4_Sb,G4_Te,G4_I,G4_Xe,G4_Cs,G4_Ba,G4_La,G4_Ce,G4_Pr,G4_Nd,G4_Pm,G4_Sm,G4_Eu,G4_Gd,G4_Tb,G4_Dy,G4_Ho,G4_Er,+30 more]
FEATURE [App::DocumentObjectGroupPython] H_element114  label="H_element : 063"  # scripted group (container) (typed FeaturePython)
  n = 2
  ref = H_element
FEATURE [App::DocumentObjectGroupPython] G4_lH2  # scripted group (container) (typed FeaturePython)
  Dunit = g/cm3
  Dvalue = 0.0708
  Group = -> [H_element114]
  conduct = 2
  density = 1
  expand = 3
  formula = G4_lH2
  name = G4_lH2
  specific = 4
FEATURE [App::DocumentObjectGroupPython] N_element049  label="N_element : 022"  # scripted group (container) (typed FeaturePython)
  n = 2
  ref = N_element
FEATURE [App::DocumentObjectGroupPython] G4_lN2  # scripted group (container) (typed FeaturePython)
  Dunit = g/cm3
  Dvalue = 0.807
  Group = -> [N_element049]
  conduct = 2
  density = 1
  expand = 3
  formula = G4_lN2
  name = G4_lN2
  specific = 4
FEATURE [App::DocumentObjectGroupPython] O_element106  label="O_element : 060"  # scripted group (container) (typed FeaturePython)
  n = 2
  ref = O_element
FEATURE [App::DocumentObjectGroupPython] G4_lO2  # scripted group (container) (typed FeaturePython)
  Dunit = g/cm3
  Dvalue = 1.141
  Group = -> [O_element106]
  conduct = 2
  density = 1
  expand = 3
  formula = G4_lO2
  name = G4_lO2
  specific = 4
FEATURE [App::DocumentObjectGroupPython] Ar_element003  label="Ar_element : 002"  # scripted group (container) (typed FeaturePython)
  n = 1
  ref = Ar_element
FEATURE [App::DocumentObjectGroupPython] G4_lAr  # scripted group (container) (typed FeaturePython)
  Dunit = g/cm3
  Dvalue = 1.396
  Group = -> [Ar_element003]
  conduct = 2
  density = 1
  expand = 3
  formula = G4_lAr
  name = G4_lAr
  specific = 4
FEATURE [App::DocumentObjectGroupPython] Br_element008  label="Br_element : 005"  # scripted group (container) (typed FeaturePython)
  n = 1
  ref = Br_element
FEATURE [App::DocumentObjectGroupPython] G4_lBr  # scripted group (container) (typed FeaturePython)
  Dunit = g/cm3
  Dvalue = 3.1028
  Group = -> [Br_element008]
  conduct = 2
  density = 1
  expand = 3
  formula = G4_lBr
  name = G4_lBr
  specific = 4
FEATURE [App::DocumentObjectGroupPython] Kr_element002  label="Kr_element : 002"  # scripted group (container) (typed FeaturePython)
  n = 1
  ref = Kr_element
FEATURE [App::DocumentObjectGroupPython] G4_lKr  # scripted group (container) (typed FeaturePython)
  Dunit = g/cm3
  Dvalue = 2.418
  Group = -> [Kr_element002]
  conduct = 2
  density = 1
  expand = 3
  formula = G4_lKr
  name = G4_lKr
  specific = 4
FEATURE [App::DocumentObjectGroupPython] Xe_element002  label="Xe_element : 002"  # scripted group (container) (typed FeaturePython)
  n = 1
  ref = Xe_element
FEATURE [App::DocumentObjectGroupPython] G4_lXe  # scripted group (container) (typed FeaturePython)
  Dunit = g/cm3
  Dvalue = 2.953
  Group = -> [Xe_element002]
  conduct = 2
  density = 1
  expand = 3
  formula = G4_lXe
  name = G4_lXe
  specific = 4
FEATURE [App::DocumentObjectGroupPython] O_element107  label="O_element : 061"  # scripted group (container) (typed FeaturePython)
  n = 4
  ref = O_element
FEATURE [App::DocumentObjectGroupPython] Pb_element004  label="Pb_element : 002"  # scripted group (container) (typed FeaturePython)
  n = 1
  ref = Pb_element
FEATURE [App::DocumentObjectGroupPython] W_element005  label="W_element : 005"  # scripted group (container) (typed FeaturePython)
  n = 1
  ref = W_element
FEATURE [App::DocumentObjectGroupPython] G4_PbWO4  # scripted group (container) (typed FeaturePython)
  Dunit = g/cm3
  Dvalue = 8.28
  Group = -> [O_element107,Pb_element004,W_element005]
  conduct = 2
  density = 1
  expand = 3
  formula = G4_PbWO4
  name = G4_PbWO4
  specific = 4
FEATURE [App::DocumentObjectGroupPython] H_element115  label="H_element : 064"  # scripted group (container) (typed FeaturePython)
  n = 1
  ref = H_element
FEATURE [App::DocumentObjectGroupPython] G4_Galactic  # scripted group (container) (typed FeaturePython)
  Dunit = g/cm3
  Dvalue = 0
  Group = -> [H_element115]
  conduct = 2
  density = 1
  expand = 3
  formula = G4_Galactic
  name = G4_Galactic
  specific = 4
FEATURE [App::DocumentObjectGroupPython] C_element125  label="C_element : 071"  # scripted group (container) (typed FeaturePython)
  n = 1
  ref = C_element
FEATURE [App::DocumentObjectGroupPython] G4_GRAPHITE_POROUS  # scripted group (container) (typed FeaturePython)
  Dunit = g/cm3
  Dvalue = 1.7
  Group = -> [C_element125]
  conduct = 2
  density = 1
  expand = 3
  formula = G4_GRAPHITE_POROUS
  name = G4_GRAPHITE_POROUS
  specific = 4
FEATURE [App::DocumentObjectGroupPython] H_element116  label="H_element : 0.150"  # scripted group (container) (typed FeaturePython)
  n = 0.080538
FEATURE [App::DocumentObjectGroupPython] C_element126  label="C_element : 0.600"  # scripted group (container) (typed FeaturePython)
  n = 0.599848
FEATURE [App::DocumentObjectGroupPython] O_element108  label="O_element : 0.320"  # scripted group (container) (typed FeaturePython)
  n = 0.319614
FEATURE [App::DocumentObjectGroupPython] G4_LUCITE  # scripted group (container) (typed FeaturePython)
  Dunit = g/cm3
  Dvalue = 1.19
  Group = -> [H_element116,C_element126,O_element108]
  conduct = 2
  density = 1
  expand = 3
  formula = G4_LUCITE
  name = G4_LUCITE
  specific = 4
FEATURE [App::DocumentObjectGroupPython] Cu_element002  label="Cu_element : 62"  # scripted group (container) (typed FeaturePython)
  n = 62
  ref = Cu_element
FEATURE [App::DocumentObjectGroupPython] Zn_element002  label="Zn_element : 35"  # scripted group (container) (typed FeaturePython)
  n = 35
  ref = Zn_element
FEATURE [App::DocumentObjectGroupPython] Pb_element005  label="Pb_element : 3"  # scripted group (container) (typed FeaturePython)
  n = 3
  ref = Pb_element
FEATURE [App::DocumentObjectGroupPython] G4_BRASS  # scripted group (container) (typed FeaturePython)
  Dunit = g/cm3
  Dvalue = 8.52
  Group = -> [Cu_element002,Zn_element002,Pb_element005]
  conduct = 2
  density = 1
  expand = 3
  formula = G4_BRASS
  name = G4_BRASS
  specific = 4
FEATURE [App::DocumentObjectGroupPython] Cu_element003  label="Cu_element : 89"  # scripted group (container) (typed FeaturePython)
  n = 89
  ref = Cu_element
FEATURE [App::DocumentObjectGroupPython] Zn_element003  label="Zn_element : 9"  # scripted group (container) (typed FeaturePython)
  n = 9
  ref = Zn_element
FEATURE [App::DocumentObjectGroupPython] Pb_element006  label="Pb_element : 2"  # scripted group (container) (typed FeaturePython)
  n = 2
  ref = Pb_element
FEATURE [App::DocumentObjectGroupPython] G4_BRONZE  # scripted group (container) (typed FeaturePython)
  Dunit = g/cm3
  Dvalue = 8.82
  Group = -> [Cu_element003,Zn_element003,Pb_element006]
  conduct = 2
  density = 1
  expand = 3
  formula = G4_BRONZE
  name = G4_BRONZE
  specific = 4
FEATURE [App::DocumentObjectGroupPython] Fe_element008  label="Fe_element : 74"  # scripted group (container) (typed FeaturePython)
  n = 74
  ref = Fe_element
FEATURE [App::DocumentObjectGroupPython] Cr_element002  label="Cr_element : 18"  # scripted group (container) (typed FeaturePython)
  n = 18
  ref = Cr_element
FEATURE [App::DocumentObjectGroupPython] Ni_element002  label="Ni_element : 8"  # scripted group (container) (typed FeaturePython)
  n = 8
  ref = Ni_element
FEATURE [App::DocumentObjectGroupPython] G4_STAINLESS_STEEL  label="G4_STAINLESS-STEEL"  # scripted group (container) (typed FeaturePython)
  Dunit = g/cm3
  Dvalue = 8
  Group = -> [Fe_element008,Cr_element002,Ni_element002]
  conduct = 2
  density = 1
  expand = 3
  formula = G4_STAINLESS-STEEL
  name = G4_STAINLESS-STEEL
  specific = 4
FEATURE [App::DocumentObjectGroupPython] H_element117  label="H_element : 065"  # scripted group (container) (typed FeaturePython)
  n = 18
  ref = H_element
FEATURE [App::DocumentObjectGroupPython] C_element127  label="C_element : 072"  # scripted group (container) (typed FeaturePython)
  n = 12
  ref = C_element
FEATURE [App::DocumentObjectGroupPython] O_element109  label="O_element : 062"  # scripted group (container) (typed FeaturePython)
  n = 7
  ref = O_element
FEATURE [App::DocumentObjectGroupPython] G4_CR39  # scripted group (container) (typed FeaturePython)
  Dunit = g/cm3
  Dvalue = 1.32
  Group = -> [H_element117,C_element127,O_element109]
  conduct = 2
  density = 1
  expand = 3
  formula = G4_CR39
  name = G4_CR39
  specific = 4
FEATURE [App::DocumentObjectGroupPython] H_element118  label="H_element : 38"  # scripted group (container) (typed FeaturePython)
  n = 38
  ref = H_element
FEATURE [App::DocumentObjectGroupPython] C_element128  label="C_element : 073"  # scripted group (container) (typed FeaturePython)
  n = 18
  ref = C_element
FEATURE [App::DocumentObjectGroupPython] O_element110  label="O_element : 063"  # scripted group (container) (typed FeaturePython)
  n = 1
  ref = O_element
FEATURE [App::DocumentObjectGroupPython] G4_OCTADECANOL  # scripted group (container) (typed FeaturePython)
  Dunit = g/cm3
  Dvalue = 0.812
  Group = -> [H_element118,C_element128,O_element110]
  conduct = 2
  density = 1
  expand = 3
  formula = G4_OCTADECANOL
  name = G4_OCTADECANOL
  specific = 4
FEATURE [App::DocumentObjectGroupPython] HEP  # scripted group (container) (typed FeaturePython)
  Group = -> [G4_lH2,G4_lN2,G4_lO2,G4_lAr,G4_lBr,G4_lKr,G4_lXe,G4_PbWO4,G4_Galactic,G4_GRAPHITE_POROUS,G4_LUCITE,G4_BRASS,G4_BRONZE,G4_STAINLESS_STEEL,G4_CR39,G4_OCTADECANOL]
FEATURE [App::DocumentObjectGroupPython] C_element129  label="C_element : 074"  # scripted group (container) (typed FeaturePython)
  n = 14
  ref = C_element
FEATURE [App::DocumentObjectGroupPython] H_element119  label="H_element : 066"  # scripted group (container) (typed FeaturePython)
  n = 10
  ref = H_element
FEATURE [App::DocumentObjectGroupPython] O_element111  label="O_element : 064"  # scripted group (container) (typed FeaturePython)
  n = 2
  ref = O_element
FEATURE [App::DocumentObjectGroupPython] N_element050  label="N_element : 023"  # scripted group (container) (typed FeaturePython)
  n = 2
  ref = N_element
FEATURE [App::DocumentObjectGroupPython] G4_KEVLAR  # scripted group (container) (typed FeaturePython)
  Dunit = g/cm3
  Dvalue = 1.44
  Group = -> [C_element129,H_element119,O_element111,N_element050]
  conduct = 2
  density = 1
  expand = 3
  formula = G4_KEVLAR
  name = G4_KEVLAR
  specific = 4
FEATURE [App::DocumentObjectGroupPython] C_element130  label="C_element : 075"  # scripted group (container) (typed FeaturePython)
  n = 10
  ref = C_element
FEATURE [App::DocumentObjectGroupPython] H_element120  label="H_element : 067"  # scripted group (container) (typed FeaturePython)
  n = 8
  ref = H_element
FEATURE [App::DocumentObjectGroupPython] O_element112  label="O_element : 065"  # scripted group (container) (typed FeaturePython)
  n = 4
  ref = O_element
FEATURE [App::DocumentObjectGroupPython] G4_DACRON  # scripted group (container) (typed FeaturePython)
  Dunit = g/cm3
  Dvalue = 1.4
  Group = -> [C_element130,H_element120,O_element112]
  conduct = 2
  density = 1
  expand = 3
  formula = G4_DACRON
  name = G4_DACRON
  specific = 4
FEATURE [App::DocumentObjectGroupPython] C_element131  label="C_element : 076"  # scripted group (container) (typed FeaturePython)
  n = 4
  ref = C_element
FEATURE [App::DocumentObjectGroupPython] H_element121  label="H_element : 068"  # scripted group (container) (typed FeaturePython)
  n = 5
  ref = H_element
FEATURE [App::DocumentObjectGroupPython] Cl_element030  label="Cl_element : 016"  # scripted group (container) (typed FeaturePython)
  n = 1
  ref = Cl_element
FEATURE [App::DocumentObjectGroupPython] G4_NEOPRENE  # scripted group (container) (typed FeaturePython)
  Dunit = g/cm3
  Dvalue = 1.23
  Group = -> [C_element131,H_element121,Cl_element030]
  conduct = 2
  density = 1
  expand = 3
  formula = G4_NEOPRENE
  name = G4_NEOPRENE
  specific = 4
FEATURE [App::DocumentObjectGroupPython] Space  # scripted group (container) (typed FeaturePython)
  Group = -> [G4_KEVLAR,G4_DACRON,G4_NEOPRENE]
FEATURE [App::DocumentObjectGroupPython] H_element122  label="H_element : 069"  # scripted group (container) (typed FeaturePython)
  n = 5
  ref = H_element
FEATURE [App::DocumentObjectGroupPython] C_element132  label="C_element : 077"  # scripted group (container) (typed FeaturePython)
  n = 4
  ref = C_element
FEATURE [App::DocumentObjectGroupPython] N_element051  label="N_element : 3"  # scripted group (container) (typed FeaturePython)
  n = 3
  ref = N_element
FEATURE [App::DocumentObjectGroupPython] O_element113  label="O_element : 066"  # scripted group (container) (typed FeaturePython)
  n = 1
  ref = O_element
FEATURE [App::DocumentObjectGroupPython] G4_CYTOSINE  # scripted group (container) (typed FeaturePython)
  Dunit = g/cm3
  Dvalue = 1.55
  Group = -> [H_element122,C_element132,N_element051,O_element113]
  conduct = 2
  density = 1
  expand = 3
  formula = G4_CYTOSINE
  name = G4_CYTOSINE
  specific = 4
FEATURE [App::DocumentObjectGroupPython] H_element123  label="H_element : 070"  # scripted group (container) (typed FeaturePython)
  n = 6
  ref = H_element
FEATURE [App::DocumentObjectGroupPython] C_element133  label="C_element : 078"  # scripted group (container) (typed FeaturePython)
  n = 5
  ref = C_element
FEATURE [App::DocumentObjectGroupPython] N_element052  label="N_element : 024"  # scripted group (container) (typed FeaturePython)
  n = 2
  ref = N_element
FEATURE [App::DocumentObjectGroupPython] O_element114  label="O_element : 067"  # scripted group (container) (typed FeaturePython)
  n = 2
  ref = O_element
FEATURE [App::DocumentObjectGroupPython] G4_THYMINE  # scripted group (container) (typed FeaturePython)
  Dunit = g/cm3
  Dvalue = 1.23
  Group = -> [H_element123,C_element133,N_element052,O_element114]
  conduct = 2
  density = 1
  expand = 3
  formula = G4_THYMINE
  name = G4_THYMINE
  specific = 4
FEATURE [App::DocumentObjectGroupPython] H_element124  label="H_element : 071"  # scripted group (container) (typed FeaturePython)
  n = 4
  ref = H_element
FEATURE [App::DocumentObjectGroupPython] C_element134  label="C_element : 079"  # scripted group (container) (typed FeaturePython)
  n = 4
  ref = C_element
FEATURE [App::DocumentObjectGroupPython] N_element053  label="N_element : 025"  # scripted group (container) (typed FeaturePython)
  n = 2
  ref = N_element
FEATURE [App::DocumentObjectGroupPython] O_element115  label="O_element : 068"  # scripted group (container) (typed FeaturePython)
  n = 2
  ref = O_element
FEATURE [App::DocumentObjectGroupPython] G4_URACIL  # scripted group (container) (typed FeaturePython)
  Dunit = g/cm3
  Dvalue = 1.32
  Group = -> [H_element124,C_element134,N_element053,O_element115]
  conduct = 2
  density = 1
  expand = 3
  formula = G4_URACIL
  name = G4_URACIL
  specific = 4
FEATURE [App::DocumentObjectGroupPython] H_element125  label="H_element : 072"  # scripted group (container) (typed FeaturePython)
  n = 4
  ref = H_element
FEATURE [App::DocumentObjectGroupPython] C_element135  label="C_element : 080"  # scripted group (container) (typed FeaturePython)
  n = 5
  ref = C_element
FEATURE [App::DocumentObjectGroupPython] N_element054  label="N_element : 026"  # scripted group (container) (typed FeaturePython)
  n = 5
  ref = N_element
FEATURE [App::DocumentObjectGroupPython] G4_DNA_ADENINE  # scripted group (container) (typed FeaturePython)
  Dunit = g/cm3
  Dvalue = 1
  Group = -> [H_element125,C_element135,N_element054]
  conduct = 2
  density = 1
  expand = 3
  formula = G4_DNA_ADENINE
  name = G4_DNA_ADENINE
  specific = 4
FEATURE [App::DocumentObjectGroupPython] H_element126  label="H_element : 073"  # scripted group (container) (typed FeaturePython)
  n = 4
  ref = H_element
FEATURE [App::DocumentObjectGroupPython] C_element136  label="C_element : 081"  # scripted group (container) (typed FeaturePython)
  n = 5
  ref = C_element
FEATURE [App::DocumentObjectGroupPython] N_element055  label="N_element : 027"  # scripted group (container) (typed FeaturePython)
  n = 5
  ref = N_element
FEATURE [App::DocumentObjectGroupPython] O_element116  label="O_element : 069"  # scripted group (container) (typed FeaturePython)
  n = 1
  ref = O_element
FEATURE [App::DocumentObjectGroupPython] G4_DNA_GUANINE  # scripted group (container) (typed FeaturePython)
  Dunit = g/cm3
  Dvalue = 1
  Group = -> [H_element126,C_element136,N_element055,O_element116]
  conduct = 2
  density = 1
  expand = 3
  formula = G4_DNA_GUANINE
  name = G4_DNA_GUANINE
  specific = 4
FEATURE [App::DocumentObjectGroupPython] H_element127  label="H_element : 074"  # scripted group (container) (typed FeaturePython)
  n = 4
  ref = H_element
FEATURE [App::DocumentObjectGroupPython] C_element137  label="C_element : 082"  # scripted group (container) (typed FeaturePython)
  n = 4
  ref = C_element
FEATURE [App::DocumentObjectGroupPython] N_element056  label="N_element : 028"  # scripted group (container) (typed FeaturePython)
  n = 3
  ref = N_element
FEATURE [App::DocumentObjectGroupPython] O_element117  label="O_element : 070"  # scripted group (container) (typed FeaturePython)
  n = 1
  ref = O_element
FEATURE [App::DocumentObjectGroupPython] G4_DNA_CYTOSINE  # scripted group (container) (typed FeaturePython)
  Dunit = g/cm3
  Dvalue = 1
  Group = -> [H_element127,C_element137,N_element056,O_element117]
  conduct = 2
  density = 1
  expand = 3
  formula = G4_DNA_CYTOSINE
  name = G4_DNA_CYTOSINE
  specific = 4
FEATURE [App::DocumentObjectGroupPython] H_element128  label="H_element : 075"  # scripted group (container) (typed FeaturePython)
  n = 5
  ref = H_element
FEATURE [App::DocumentObjectGroupPython] C_element138  label="C_element : 083"  # scripted group (container) (typed FeaturePython)
  n = 5
  ref = C_element
FEATURE [App::DocumentObjectGroupPython] N_element057  label="N_element : 029"  # scripted group (container) (typed FeaturePython)
  n = 2
  ref = N_element
FEATURE [App::DocumentObjectGroupPython] O_element118  label="O_element : 071"  # scripted group (container) (typed FeaturePython)
  n = 2
  ref = O_element
FEATURE [App::DocumentObjectGroupPython] G4_DNA_THYMINE  # scripted group (container) (typed FeaturePython)
  Dunit = g/cm3
  Dvalue = 1
  Group = -> [H_element128,C_element138,N_element057,O_element118]
  conduct = 2
  density = 1
  expand = 3
  formula = G4_DNA_THYMINE
  name = G4_DNA_THYMINE
  specific = 4
FEATURE [App::DocumentObjectGroupPython] H_element129  label="H_element : 076"  # scripted group (container) (typed FeaturePython)
  n = 3
  ref = H_element
FEATURE [App::DocumentObjectGroupPython] C_element139  label="C_element : 084"  # scripted group (container) (typed FeaturePython)
  n = 4
  ref = C_element
FEATURE [App::DocumentObjectGroupPython] N_element058  label="N_element : 030"  # scripted group (container) (typed FeaturePython)
  n = 2
  ref = N_element
FEATURE [App::DocumentObjectGroupPython] O_element119  label="O_element : 072"  # scripted group (container) (typed FeaturePython)
  n = 2
  ref = O_element
FEATURE [App::DocumentObjectGroupPython] G4_DNA_URACIL  # scripted group (container) (typed FeaturePython)
  Dunit = g/cm3
  Dvalue = 1
  Group = -> [H_element129,C_element139,N_element058,O_element119]
  conduct = 2
  density = 1
  expand = 3
  formula = G4_DNA_URACIL
  name = G4_DNA_URACIL
  specific = 4
FEATURE [App::DocumentObjectGroupPython] H_element130  label="H_element : 077"  # scripted group (container) (typed FeaturePython)
  n = 10
  ref = H_element
FEATURE [App::DocumentObjectGroupPython] C_element140  label="C_element : 085"  # scripted group (container) (typed FeaturePython)
  n = 10
  ref = C_element
FEATURE [App::DocumentObjectGroupPython] N_element059  label="N_element : 031"  # scripted group (container) (typed FeaturePython)
  n = 5
  ref = N_element
FEATURE [App::DocumentObjectGroupPython] O_element120  label="O_element : 073"  # scripted group (container) (typed FeaturePython)
  n = 4
  ref = O_element
FEATURE [App::DocumentObjectGroupPython] G4_DNA_ADENOSINE  # scripted group (container) (typed FeaturePython)
  Dunit = g/cm3
  Dvalue = 1
  Group = -> [H_element130,C_element140,N_element059,O_element120]
  conduct = 2
  density = 1
  expand = 3
  formula = G4_DNA_ADENOSINE
  name = G4_DNA_ADENOSINE
  specific = 4
FEATURE [App::DocumentObjectGroupPython] H_element131  label="H_element : 078"  # scripted group (container) (typed FeaturePython)
  n = 10
  ref = H_element
FEATURE [App::DocumentObjectGroupPython] C_element141  label="C_element : 086"  # scripted group (container) (typed FeaturePython)
  n = 10
  ref = C_element
FEATURE [App::DocumentObjectGroupPython] N_element060  label="N_element : 032"  # scripted group (container) (typed FeaturePython)
  n = 5
  ref = N_element
FEATURE [App::DocumentObjectGroupPython] O_element121  label="O_element : 074"  # scripted group (container) (typed FeaturePython)
  n = 5
  ref = O_element
FEATURE [App::DocumentObjectGroupPython] G4_DNA_GUANOSINE  # scripted group (container) (typed FeaturePython)
  Dunit = g/cm3
  Dvalue = 1
  Group = -> [H_element131,C_element141,N_element060,O_element121]
  conduct = 2
  density = 1
  expand = 3
  formula = G4_DNA_GUANOSINE
  name = G4_DNA_GUANOSINE
  specific = 4
FEATURE [App::DocumentObjectGroupPython] H_element132  label="H_element : 079"  # scripted group (container) (typed FeaturePython)
  n = 10
  ref = H_element
FEATURE [App::DocumentObjectGroupPython] C_element142  label="C_element : 087"  # scripted group (container) (typed FeaturePython)
  n = 9
  ref = C_element
FEATURE [App::DocumentObjectGroupPython] N_element061  label="N_element : 033"  # scripted group (container) (typed FeaturePython)
  n = 3
  ref = N_element
FEATURE [App::DocumentObjectGroupPython] O_element122  label="O_element : 075"  # scripted group (container) (typed FeaturePython)
  n = 5
  ref = O_element
FEATURE [App::DocumentObjectGroupPython] G4_DNA_CYTIDINE  # scripted group (container) (typed FeaturePython)
  Dunit = g/cm3
  Dvalue = 1
  Group = -> [H_element132,C_element142,N_element061,O_element122]
  conduct = 2
  density = 1
  expand = 3
  formula = G4_DNA_CYTIDINE
  name = G4_DNA_CYTIDINE
  specific = 4
FEATURE [App::DocumentObjectGroupPython] H_element133  label="H_element : 080"  # scripted group (container) (typed FeaturePython)
  n = 9
  ref = H_element
FEATURE [App::DocumentObjectGroupPython] C_element143  label="C_element : 088"  # scripted group (container) (typed FeaturePython)
  n = 9
  ref = C_element
FEATURE [App::DocumentObjectGroupPython] N_element062  label="N_element : 034"  # scripted group (container) (typed FeaturePython)
  n = 2
  ref = N_element
FEATURE [App::DocumentObjectGroupPython] O_element123  label="O_element : 076"  # scripted group (container) (typed FeaturePython)
  n = 6
  ref = O_element
FEATURE [App::DocumentObjectGroupPython] G4_DNA_URIDINE  # scripted group (container) (typed FeaturePython)
  Dunit = g/cm3
  Dvalue = 1
  Group = -> [H_element133,C_element143,N_element062,O_element123]
  conduct = 2
  density = 1
  expand = 3
  formula = G4_DNA_URIDINE
  name = G4_DNA_URIDINE
  specific = 4
FEATURE [App::DocumentObjectGroupPython] H_element134  label="H_element : 081"  # scripted group (container) (typed FeaturePython)
  n = 11
  ref = H_element
FEATURE [App::DocumentObjectGroupPython] C_element144  label="C_element : 089"  # scripted group (container) (typed FeaturePython)
  n = 10
  ref = C_element
FEATURE [App::DocumentObjectGroupPython] N_element063  label="N_element : 035"  # scripted group (container) (typed FeaturePython)
  n = 2
  ref = N_element
FEATURE [App::DocumentObjectGroupPython] O_element124  label="O_element : 077"  # scripted group (container) (typed FeaturePython)
  n = 6
  ref = O_element
FEATURE [App::DocumentObjectGroupPython] G4_DNA_METHYLURIDINE  # scripted group (container) (typed FeaturePython)
  Dunit = g/cm3
  Dvalue = 1
  Group = -> [H_element134,C_element144,N_element063,O_element124]
  conduct = 2
  density = 1
  expand = 3
  formula = G4_DNA_METHYLURIDINE
  name = G4_DNA_METHYLURIDINE
  specific = 4
FEATURE [App::DocumentObjectGroupPython] P_element014  label="P_element : 003"  # scripted group (container) (typed FeaturePython)
  n = 1
  ref = P_element
FEATURE [App::DocumentObjectGroupPython] O_element125  label="O_element : 078"  # scripted group (container) (typed FeaturePython)
  n = 3
  ref = O_element
FEATURE [App::DocumentObjectGroupPython] G4_DNA_MONOPHOSPHATE  # scripted group (container) (typed FeaturePython)
  Dunit = g/cm3
  Dvalue = 1
  Group = -> [P_element014,O_element125]
  conduct = 2
  density = 1
  expand = 3
  formula = G4_DNA_MONOPHOSPHATE
  name = G4_DNA_MONOPHOSPHATE
  specific = 4
FEATURE [App::DocumentObjectGroupPython] H_element135  label="H_element : 082"  # scripted group (container) (typed FeaturePython)
  n = 10
  ref = H_element
FEATURE [App::DocumentObjectGroupPython] C_element145  label="C_element : 090"  # scripted group (container) (typed FeaturePython)
  n = 10
  ref = C_element
FEATURE [App::DocumentObjectGroupPython] N_element064  label="N_element : 036"  # scripted group (container) (typed FeaturePython)
  n = 5
  ref = N_element
FEATURE [App::DocumentObjectGroupPython] O_element126  label="O_element : 079"  # scripted group (container) (typed FeaturePython)
  n = 7
  ref = O_element
FEATURE [App::DocumentObjectGroupPython] P_element015  label="P_element : 004"  # scripted group (container) (typed FeaturePython)
  n = 1
  ref = P_element
FEATURE [App::DocumentObjectGroupPython] G4_DNA_A  # scripted group (container) (typed FeaturePython)
  Dunit = g/cm3
  Dvalue = 1
  Group = -> [H_element135,C_element145,N_element064,O_element126,P_element015]
  conduct = 2
  density = 1
  expand = 3
  formula = G4_DNA_A
  name = G4_DNA_A
  specific = 4
FEATURE [App::DocumentObjectGroupPython] H_element136  label="H_element : 083"  # scripted group (container) (typed FeaturePython)
  n = 10
  ref = H_element
FEATURE [App::DocumentObjectGroupPython] C_element146  label="C_element : 091"  # scripted group (container) (typed FeaturePython)
  n = 10
  ref = C_element
FEATURE [App::DocumentObjectGroupPython] N_element065  label="N_element : 037"  # scripted group (container) (typed FeaturePython)
  n = 5
  ref = N_element
FEATURE [App::DocumentObjectGroupPython] O_element127  label="O_element : 8"  # scripted group (container) (typed FeaturePython)
  n = 8
  ref = O_element
FEATURE [App::DocumentObjectGroupPython] P_element016  label="P_element : 005"  # scripted group (container) (typed FeaturePython)
  n = 1
  ref = P_element
FEATURE [App::DocumentObjectGroupPython] G4_DNA_G  # scripted group (container) (typed FeaturePython)
  Dunit = g/cm3
  Dvalue = 1
  Group = -> [H_element136,C_element146,N_element065,O_element127,P_element016]
  conduct = 2
  density = 1
  expand = 3
  formula = G4_DNA_G
  name = G4_DNA_G
  specific = 4
FEATURE [App::DocumentObjectGroupPython] H_element137  label="H_element : 084"  # scripted group (container) (typed FeaturePython)
  n = 10
  ref = H_element
FEATURE [App::DocumentObjectGroupPython] C_element147  label="C_element : 092"  # scripted group (container) (typed FeaturePython)
  n = 9
  ref = C_element
FEATURE [App::DocumentObjectGroupPython] N_element066  label="N_element : 038"  # scripted group (container) (typed FeaturePython)
  n = 3
  ref = N_element
FEATURE [App::DocumentObjectGroupPython] O_element128  label="O_element : 080"  # scripted group (container) (typed FeaturePython)
  n = 8
  ref = O_element
FEATURE [App::DocumentObjectGroupPython] P_element017  label="P_element : 006"  # scripted group (container) (typed FeaturePython)
  n = 1
  ref = P_element
FEATURE [App::DocumentObjectGroupPython] G4_DNA_C  # scripted group (container) (typed FeaturePython)
  Dunit = g/cm3
  Dvalue = 1
  Group = -> [H_element137,C_element147,N_element066,O_element128,P_element017]
  conduct = 2
  density = 1
  expand = 3
  formula = G4_DNA_C
  name = G4_DNA_C
  specific = 4
FEATURE [App::DocumentObjectGroupPython] H_element138  label="H_element : 085"  # scripted group (container) (typed FeaturePython)
  n = 9
  ref = H_element
FEATURE [App::DocumentObjectGroupPython] C_element148  label="C_element : 093"  # scripted group (container) (typed FeaturePython)
  n = 9
  ref = C_element
FEATURE [App::DocumentObjectGroupPython] N_element067  label="N_element : 039"  # scripted group (container) (typed FeaturePython)
  n = 2
  ref = N_element
FEATURE [App::DocumentObjectGroupPython] O_element129  label="O_element : 9"  # scripted group (container) (typed FeaturePython)
  n = 9
  ref = O_element
FEATURE [App::DocumentObjectGroupPython] P_element018  label="P_element : 007"  # scripted group (container) (typed FeaturePython)
  n = 1
  ref = P_element
FEATURE [App::DocumentObjectGroupPython] G4_DNA_U  # scripted group (container) (typed FeaturePython)
  Dunit = g/cm3
  Dvalue = 1
  Group = -> [H_element138,C_element148,N_element067,O_element129,P_element018]
  conduct = 2
  density = 1
  expand = 3
  formula = G4_DNA_U
  name = G4_DNA_U
  specific = 4
FEATURE [App::DocumentObjectGroupPython] H_element139  label="H_element : 086"  # scripted group (container) (typed FeaturePython)
  n = 11
  ref = H_element
FEATURE [App::DocumentObjectGroupPython] C_element149  label="C_element : 094"  # scripted group (container) (typed FeaturePython)
  n = 10
  ref = C_element
FEATURE [App::DocumentObjectGroupPython] N_element068  label="N_element : 040"  # scripted group (container) (typed FeaturePython)
  n = 2
  ref = N_element
FEATURE [App::DocumentObjectGroupPython] O_element130  label="O_element : 081"  # scripted group (container) (typed FeaturePython)
  n = 9
  ref = O_element
FEATURE [App::DocumentObjectGroupPython] P_element019  label="P_element : 008"  # scripted group (container) (typed FeaturePython)
  n = 1
  ref = P_element
FEATURE [App::DocumentObjectGroupPython] G4_DNA_MU  # scripted group (container) (typed FeaturePython)
  Dunit = g/cm3
  Dvalue = 1
  Group = -> [H_element139,C_element149,N_element068,O_element130,P_element019]
  conduct = 2
  density = 1
  expand = 3
  formula = G4_DNA_MU
  name = G4_DNA_MU
  specific = 4
FEATURE [App::DocumentObjectGroupPython] BioChemical  # scripted group (container) (typed FeaturePython)
  Group = -> [G4_CYTOSINE,G4_THYMINE,G4_URACIL,G4_DNA_ADENINE,G4_DNA_GUANINE,G4_DNA_CYTOSINE,G4_DNA_THYMINE,G4_DNA_URACIL,G4_DNA_ADENOSINE,G4_DNA_GUANOSINE,G4_DNA_CYTIDINE,G4_DNA_URIDINE,G4_DNA_METHYLURIDINE,G4_DNA_MONOPHOSPHATE,G4_DNA_A,G4_DNA_G,G4_DNA_C,G4_DNA_U,G4_DNA_MU]
FEATURE [App::DocumentObjectGroupPython] G4Materials  # scripted group (container) (typed FeaturePython)
  Group = -> [NIST,Element,HEP,Space,BioChemical]
  version = 1
FEATURE [App::DocumentObjectGroupPython] Geant4  # scripted group (container) (typed FeaturePython)
  Group = -> [G4Isotopes,G4Elements,G4Materials]
FEATURE [App::DocumentObjectGroupPython] Materials  # scripted group (container) (typed FeaturePython)
  Group = -> [Geant4]
FEATURE [Part::FeaturePython] GDMLBox_WorldBox  # WARN: FeaturePython — macro-defined, semantics opaque (R4)
  lunit = 2
  material = 5
  x = 2350.01
  y = 2367.27
  z = 13016.7
FEATURE [Part::Cylinder] Cylinder
  Angle = 360
  AttacherType = Attacher::AttachEngine3D
  FirstAngle = 0
  Height = 200
  Placement = pos=(474,0,4850) rot=(0,0,1;0rad)
  Radius = 60
  SecondAngle = 0
FEATURE [Part::FeaturePython] Array  # Draft array (typed FeaturePython)
  Angle = 360
  ArrayType = 1
  Axis = (0,0,1)
  Base = -> Cylinder
  Center = (0,0,0)
  Count = 6
  Fuse = false
  IntervalAxis = (0,0,0)
  IntervalX = (50,0,0)
  IntervalY = (0,50,0)
  IntervalZ = (0,0,50)
  NumberCircles = 3
  NumberPolar = 6
  NumberX = 2
  NumberY = 2
  NumberZ = 1
  RadialDistance = 50
  Symmetry = 1
  TangentialDistance = 25
FEATURE [Sketcher::SketchObject] Sketch001
  ArcFitTolerance = 0
  AttachmentSupport = -> [YZ_Plane001]
  FullyConstrained = false
  MakeInternals = false
  MapMode = 5
  Placement = pos=(0,0,0) rot=(0.57735,0.57735,0.57735;2.0944rad)
  sketch-geometry (36):
    g0: LineSegment StartX=345.196 StartY=1207.39 StartZ=0 EndX=345.196 EndY=4779.1 EndZ=0
    g1: LineSegment StartX=910.487 StartY=4896.42 StartZ=0 EndX=910.487 EndY=5006.42 EndZ=0
    g2: LineSegment StartX=435.196 StartY=4869.1 StartZ=0 EndX=445.196 EndY=4869.1 EndZ=0
    g3: LineSegment StartX=445.196 StartY=4869.1 StartZ=0 EndX=445.196 EndY=4896.42 EndZ=0
    g4: LineSegment StartX=445.196 StartY=4896.42 StartZ=0 EndX=910.487 EndY=4896.42 EndZ=0
    g5: LineSegment StartX=318.538 StartY=5006.42 StartZ=0 EndX=910.487 EndY=5006.42 EndZ=0
    g6: LineSegment StartX=175.531 StartY=1234.96 StartZ=0 EndX=318.538 EndY=1234.96 EndZ=0
    g7: LineSegment StartX=318.538 StartY=5006.42 StartZ=0 EndX=318.538 EndY=1234.96 EndZ=0
    g8: LineSegment StartX=0 StartY=39.215 StartZ=0 EndX=0 EndY=0 EndZ=0
    g9-g16: Circle [constr] x8 (B-spline internal-alignment scaffolding for g17; pole/knot coordinates omitted)
    g17: BSplineCurve PolesCount=8 KnotsCount=6 Degree=3 IsPeriodic=0
    g18-g23: GeomPoint [constr] x6 (B-spline internal-alignment scaffolding for g17; pole/knot coordinates omitted)
    g24: LineSegment StartX=175.531 StartY=1234.96 StartZ=0 EndX=175.531 EndY=838.896 EndZ=0
    g25-g29: Circle [constr] x5 (B-spline internal-alignment scaffolding for g30; pole/knot coordinates omitted)
    g30: BSplineCurve PolesCount=5 KnotsCount=3 Degree=3 IsPeriodic=0
    g31: GeomPoint [constr] X=175.531 Y=838.896 Z=0
    g32: GeomPoint [constr] X=165.058 Y=242.363 Z=0
    g33: GeomPoint [constr] X=0 Y=39.215 Z=0
    g34: ArcOfCircle CenterX=435.196 CenterY=4779.1 CenterZ=0 NormalX=0 NormalY=0 NormalZ=1 AngleXU=0 Radius=90 StartAngle=1.5708 EndAngle=3.14159
    g35: GeomPoint [constr] X=345.196 Y=4869.1 Z=0
  constraints (38):
    c: Vertical(g1)
    c: Horizontal(g2)
    c: Coincident(g2,g3)
    c: Vertical(g3)
    c: Coincident(g3,g4)
    c: Coincident(g4,g1)
    c: Horizontal(g4)
    c: Coincident(g5,g1)
    c: Horizontal(g5)
    c: Horizontal(g6)
    c: Coincident(g7,g5)
    c: Coincident(g7,g6)
    c: Vertical(g7)
    c: DistanceX(g35,g2) = 100
    c: Vertical(g8)
    c: Vertical(g0)
    c: Coincident(g17,g0)
    c: Weight(g9) = 1
    c: Equal(g9, g10-g16) x7
    c: Coincident(g17,g8)
    c: InternalAlignment(g9-g16 -> g17) x8
    c: InternalAlignment(g18-g23 -> g17) x6
    c: Coincident(g24,g6)
    c: Vertical(g24)
    c: Coincident(g30,g24)
    c: Weight(g25) = 1
    c: Equal(g25, g26-g29) x4
    c: Coincident(g30,g8)
    c: InternalAlignment(g25-g29 -> g30) x5
    c: InternalAlignment(g31,g30)
    c: InternalAlignment(g32,g30)
    c: InternalAlignment(g33,g30)
    c: Coincident(g8,g-1)
    c: PointOnObject(g35,g2)
    c: PointOnObject(g35,g0)
    c: Tangent(g2,g34) = 1.5708
    c: Tangent(g0,g34) = 1.5708
    c: Radius(g34) = 90
FEATURE [Part::Revolution] Revolve
  Angle = 360
  Axis = (0,0,1)
  Base = (0,0,0)
  FaceMakerClass = Part::FaceMakerBullseye
  Solid = true
  Source = -> Sketch001
  Symmetric = false
  material = 176
FEATURE [Part::Cut] Cut
  Base = -> Revolve
  Tool = -> Array
FEATURE [App::Part] Bool_Cut
  Group = -> [Sketch001,Revolve,Cylinder,Cut]
  Origin = -> Origin004
FEATURE [App::Part] worldVOL
  Group = -> [GDMLBox_WorldBox,Bool_Cut]
  Origin = -> Origin
